FCSTD DOCUMENT  (FreeCAD 0.21R33668 +26 (Git))
Label: CaseV2_Assembly
License: All rights reserved
LicenseURL: https://en.wikipedia.org/wiki/All_rights_reserved
objects: App::Link×9, App::DocumentObjectGroup×3, PartDesign::CoordinateSystem×1, App::FeaturePython×1, App::Part×1
note: 1 computed .brp shape members not serialized (recipe doc carries the construction recipe); baked Part::Feature solids carry a one-line shape summary decoded from their .brp
EXTERNAL_REF file=Parts/Casing2.FCStd obj=LCS_Origin
EXTERNAL_REF file=Parts/Casing2.FCStd obj=Model
EXTERNAL_REF file=Parts/Casing2.FCStd obj=LCS_MLX
EXTERNAL_REF file=Parts/Support_MLX.FCStd obj=LCS_carrier
EXTERNAL_REF file=Parts/Support_MLX.FCStd obj=Model
EXTERNAL_REF file=Parts/MLX90640.FCStd obj=LCS_mlx
EXTERNAL_REF file=Parts/Support_MLX.FCStd obj=LCS_MLX
EXTERNAL_REF file=Parts/MLX90640.FCStd obj=Model
EXTERNAL_REF file=Parts/Casing2.FCStd obj=LCS_interface
EXTERNAL_REF file=Parts/Handgrip.FCStd obj=LCS_screw
EXTERNAL_REF file=Parts/Handgrip.FCStd obj=Model
EXTERNAL_REF file=Parts/Casing2.FCStd obj=LCS_beam
EXTERNAL_REF file=Parts/Casing_Lid_2.FCStd obj=LCS_screw
EXTERNAL_REF file=Parts/Casing_Lid_2.FCStd obj=Model
EXTERNAL_REF file=Parts/Casing2.FCStd obj=LCS_Display
EXTERNAL_REF file=Parts/Support_Display_new.FCStd obj=LCS_side
EXTERNAL_REF file=Parts/Support_Display_new.FCStd obj=Model
EXTERNAL_REF file=Parts/Display_Berrybase.FCStd obj=LCS_Connector
EXTERNAL_REF file=Parts/Support_Display_new.FCStd obj=LCS_display
EXTERNAL_REF file=Parts/Display_Berrybase.FCStd obj=Model
EXTERNAL_REF file=Parts/Casing2.FCStd obj=LCS_Raspi
EXTERNAL_REF file=Parts/Support_Raspi_new.FCStd obj=LCS_side
EXTERNAL_REF file=Parts/Support_Raspi_new.FCStd obj=Model
EXTERNAL_REF file=Parts/Raspberrypi4B.FCStd obj=LCS_Screw
EXTERNAL_REF file=Parts/Support_Raspi_new.FCStd obj=LCS_raspi
EXTERNAL_REF file=Parts/Raspberrypi4B.FCStd obj=Model

FEATURE [App::DocumentObjectGroup] Parts
FEATURE [PartDesign::CoordinateSystem] LCS_Origin
  AttacherType = Attacher::AttachEngine3D
  MapMode = 2
  Support = -> [X_Axis]
FEATURE [App::DocumentObjectGroup] Constraints
FEATURE [App::FeaturePython] Variables  # WARN: FeaturePython — macro-defined, semantics opaque (R4)
  Type = App::PropertyContainer
FEATURE [App::DocumentObjectGroup] Configurations
FEATURE [App::Link] Casing2
  AttachedBy = #LCS_Origin
  AttachedTo = Parent Assembly#LCS_Origin
  LinkedObject = -> <external Parts/Casing2.FCStd>#Model
  SolverId = Asm4EE
  expr: Placement = LCS_Origin.Placement * AttachmentOffset * Casing2#LCS_Origin.Placement ^ -1
FEATURE [App::Link] Support_MLX
  AttachedBy = #LCS_carrier
  AttachedTo = Casing2#LCS_MLX
  AttachmentOffset = pos=(0,0,0) rot=(0.707107,0.707107,0;3.14159rad)
  LinkPlacement = pos=(11.7198,36.5796,47.5) rot=(-0.519988,0.677661,-0.519988;4.33274rad)
  LinkedObject = -> <external Parts/Support_MLX.FCStd>#Model
  Placement = pos=(11.7198,36.5796,47.5) rot=(-0.519988,0.677661,-0.519988;4.33274rad)
  SolverId = Asm4EE
  expr: Placement = Casing2.Placement * Casing2#LCS_MLX.Placement * AttachmentOffset * Support_MLX#LCS_carrier.Placement ^ -1
FEATURE [App::Link] MLX90640
  AttachedBy = #LCS_mlx
  AttachedTo = Support_MLX#LCS_MLX
  AttachmentOffset = pos=(0,0,0) rot=(0,1,0;3.14159rad)
  LinkPlacement = pos=(13.0139,41.4093,47.5) rot=(0.621515,0.476905,0.621515;4.0316rad)
  LinkedObject = -> <external Parts/MLX90640.FCStd>#Model
  Placement = pos=(13.0139,41.4093,47.5) rot=(0.621515,0.476905,0.621515;4.0316rad)
  SolverId = Asm4EE
  expr: Placement = Support_MLX.Placement * Support_MLX#LCS_MLX.Placement * AttachmentOffset * MLX90640#LCS_mlx.Placement ^ -1
FEATURE [App::Link] Handgrip
  AttachedBy = #LCS_screw
  AttachedTo = Casing2#LCS_interface
  AttachmentOffset = pos=(0,0,0) rot=(1,0,0;3.14159rad)
  LinkPlacement = pos=(-46.3076,-21.9376,46.5) rot=(-0.704063,0.092692,0.704063;2.95674rad)
  LinkedObject = -> <external Parts/Handgrip.FCStd>#Model
  Placement = pos=(-46.3076,-21.9376,46.5) rot=(-0.704063,0.092692,0.704063;2.95674rad)
  SolverId = Asm4EE
  expr: Placement = Casing2.Placement * Casing2#LCS_interface.Placement * AttachmentOffset * Handgrip#LCS_screw.Placement ^ -1
FEATURE [App::Link] Casing_Lid_2
  AttachedBy = #LCS_screw
  AttachedTo = Casing2#LCS_beam
  AttachmentOffset = pos=(0,0,0) rot=(1,0,0;3.14159rad)
  LinkPlacement = pos=(-0.401924,-1.5,95) rot=(0,1,0;3.14159rad)
  LinkedObject = -> <external Parts/Casing_Lid_2.FCStd>#Model
  Placement = pos=(-0.401924,-1.5,95) rot=(0,1,0;3.14159rad)
  SolverId = Asm4EE
  expr: Placement = Casing2.Placement * Casing2#LCS_beam.Placement * AttachmentOffset * Casing_Lid_2#LCS_screw.Placement ^ -1
FEATURE [App::Link] Support_Display_new
  AttachedBy = #LCS_side
  AttachedTo = Casing2#LCS_Display
  AttachmentOffset = pos=(0,0,0) rot=(0.707107,-0.707107,0;3.14159rad)
  LinkPlacement = pos=(-12.8616,-41,47.5) rot=(0.57735,-0.57735,-0.57735;4.18879rad)
  LinkedObject = -> <external Parts/Support_Display_new.FCStd>#Model
  Placement = pos=(-12.8616,-41,47.5) rot=(0.57735,-0.57735,-0.57735;4.18879rad)
  SolverId = Asm4EE
  expr: Placement = Casing2.Placement * Casing2#LCS_Display.Placement * AttachmentOffset * Support_Display_new#LCS_side.Placement ^ -1
FEATURE [App::Link] Display_Berrybase
  AttachedBy = #LCS_Connector
  AttachedTo = Support_Display_new#LCS_display
  AttachmentOffset = pos=(0,0,0) rot=(0,0,1;3.14159rad)
  LinkPlacement = pos=(-11.8616,-41,48.5) rot=(-0.57735,-0.57735,-0.57735;2.0944rad)
  LinkedObject = -> <external Parts/Display_Berrybase.FCStd>#Model
  Placement = pos=(-11.8616,-41,48.5) rot=(-0.57735,-0.57735,-0.57735;2.0944rad)
  SolverId = Asm4EE
  expr: Placement = Support_Display_new.Placement * Support_Display_new#LCS_display.Placement * AttachmentOffset * Display_Berrybase#LCS_Connector.Placement ^ -1
FEATURE [App::Link] Support_Raspi_new
  AttachedBy = #LCS_side
  AttachedTo = Casing2#LCS_Raspi
  AttachmentOffset = pos=(0,0,0) rot=(0.707107,-0.707107,0;3.14159rad)
  LinkPlacement = pos=(-5.04252,6.75875,47.5) rot=(0.519988,-0.677661,-0.519988;4.33274rad)
  LinkedObject = -> <external Parts/Support_Raspi_new.FCStd>#Model
  Placement = pos=(-5.04252,6.75875,47.5) rot=(0.519988,-0.677661,-0.519988;4.33274rad)
  SolverId = Asm4EE
  expr: Placement = Casing2.Placement * Casing2#LCS_Raspi.Placement * AttachmentOffset * Support_Raspi_new#LCS_side.Placement ^ -1
FEATURE [App::Link] Raspberrypi4B
  AttachedBy = #LCS_Screw
  AttachedTo = Support_Raspi_new#LCS_raspi
  AttachmentOffset = pos=(0,0,0) rot=(0,0,1;3.14159rad)
  LinkPlacement = pos=(-6.0778,2.89505,45.5) rot=(-0.621515,-0.476905,0.621515;4.0316rad)
  LinkedObject = -> <external Parts/Raspberrypi4B.FCStd>#Model
  Placement = pos=(-6.0778,2.89505,45.5) rot=(-0.621515,-0.476905,0.621515;4.0316rad)
  SolverId = Asm4EE
  expr: Placement = Support_Raspi_new.Placement * Support_Raspi_new#LCS_raspi.Placement * AttachmentOffset * Raspberrypi4B#LCS_Screw.Placement ^ -1
FEATURE [App::Part] Model
  AssemblyType = Part::Link
  Group = -> [LCS_Origin,Constraints,Variables,Configurations,Casing2,Support_MLX,MLX90640,Handgrip,Casing_Lid_2,Support_Display_new,Display_Berrybase,Support_Raspi_new,Raspberrypi4B]
  Origin = -> Origin
  Type = Assembly

RESOLVED EXTERNAL PARTS (link-assembly join: the EXTERNAL_REF files above that resolve inside this repo's crawl, each included once):
---- part Parts/Casing2.FCStd = doc fcstd_00092494c22c ----
FCSTD DOCUMENT  (FreeCAD 0.21R33668 +26 (Git))
Label: Casing2
License: All rights reserved
LicenseURL: https://en.wikipedia.org/wiki/All_rights_reserved
objects: Sketcher::SketchObject×19, PartDesign::Pocket×14, PartDesign::CoordinateSystem×6, PartDesign::Hole×3, App::DocumentObjectGroup×3, PartDesign::Pad×2, Spreadsheet::Sheet×1, PartDesign::Fillet×1, App::FeaturePython×1, PartDesign::Body×1, App::Part×1, Mesh::Feature×1
note: 66 computed .brp shape members not serialized (recipe doc carries the construction recipe); baked Part::Feature solids carry a one-line shape summary decoded from their .brp
EXTERNAL_REF file=Display_Berrybase.FCStd obj=Spreadsheet
EXTERNAL_REF file=MLX90640.FCStd obj=Spreadsheet
EXTERNAL_REF file=Raspberrypi4B.FCStd obj=Spreadsheet
EXTERNAL_REF file=Support_Display_new.FCStd obj=Spreadsheet
EXTERNAL_REF file=Support_MLX.FCStd obj=Spreadsheet
EXTERNAL_REF file=Support_Raspi_new.FCStd obj=Spreadsheet

FEATURE [Spreadsheet::Sheet] Spreadsheet
  cells = B2='slant; C2(slant)==15 °; E2='main_case_width; F2(main_case_width)==95 mm; H2='display_width; I2(display_width)==<<Display_Berrybase>>#Spreadsheet.width; B3='walls_thickness; C3(walls_thickness)==2 mm; E3='main_case_height; F3(main_case_height)==85 mm; H3='display_height; I3(display_height)==<<Display_Berrybase>>#Spreadsheet.height; B4='screw_radius; C4(screw_radius)==1.5 mm; E4='main_case_length; F4(main_case_length)==100 mm; B5='front_thickness; C5(front_thickness)==5 mm; H5='mlx_cam_height; I5(mlx_cam_height)==<<MLX90640>>#Spreadsheet.cam_height; H6='mlx_extra_space; I6(mlx_extra_space)==2 mm; H7='mlx_radius; I7(mlx_radius)==<<MLX90640>>#Spreadsheet.cam_rad; B9='display_guard_depth; C9(display_guard_depth)==1 mm; E9='mlx_carrier_height; F9(mlx_carrier_height)==<<Support_MLX>>#Spreadsheet.carrier_height; H9='raspi_carrier_hole_dist; I9(raspi_carrier_hole_dist)==<<Support_Raspi_new>>#<<Spreadsheet>>.carrier_holes_space; B10='display_guard_size; C10(display_guard_size)==3 mm; E10='mlx_carrier_width; F10(mlx_carrier_width)==<<Support_MLX>>#Spreadsheet.carrier_width; H10='raspi_carrier_height; I10(raspi_carrier_height)==<<Support_Raspi_new>>#Spreadsheet.height; B11='display_clearance; C11(display_clearance)==1 mm; H11='raspi_carrier_depth; I11(raspi_carrier_depth)==<<Support_Raspi_new>>#Spreadsheet.depth; B12='display_hole_depth; C12(display_hole_depth)==display_width + display_clearance - display_guard_size - display_right_guard_extra; E12='beams_width; F12(beams_width)==10 mm; B13='display_right_guard_extra; C13(display_right_guard_extra)==5 mm; E13='beams_height; F13(beams_height)==10 mm; H13='raspi_height; I13(raspi_height)==<<Raspberrypi4B>>#Spreadsheet.height; H14='raspi_thickness; I14(raspi_thickness)==<<Raspberrypi4B>>#Spreadsheet.thickness; B15='display_thickness; C15(display_thickness)==<<Display_Berrybase>>#Spreadsheet.thickness; E15='beam_LB_offset; F15(beam_LB_offset)==80 mm; B16='display_carrier_height; C16(display_carrier_height)==<<Support_Display_new>>#Spreadsheet.height; E16='beam_LF_offset; F16(beam_LF_offset)==15 mm; H16='raspi_usb_width; I16(raspi_usb_width)==14 mm; E17='beam_UB_offset; F17(beam_UB_offset)==60 mm; H17='raspi_usb_height; I17(raspi_usb_height)==<<Raspberrypi4B>>#Spreadsheet.usb_height + 0 mm; B18='display_carrier_hole_dist; C18(display_carrier_hole_dist)==<<Support_Display_new>>#<<Spreadsheet>>.beams_seperation + <<Support_Display_new>>#<<Spreadsheet>>.beams_width; E18='beam_UF_offset; F18(beam_UF_offset)==15 mm; H18='raspi_eth_width; I18(raspi_eth_width)==<<Raspberrypi4B>>#Spreadsheet.ethernet_width; B19='display_carrier_offset; C19(display_carrier_offset)==display_thickness + display_carrier_height / 2 + 1 mm; H19='raspi_eth_height; I19(raspi_eth_height)==<<Raspberrypi4B>>#Spreadsheet.ethernet_height; E20='interface_width; F20(interface_width)==65 mm; H20='raspi_usb_lower_offset; I20(raspi_usb_lower_offset)==<<Raspberrypi4B>>#Spreadsheet.usb_lower_offset; B21='ports_clearance; C21(ports_clearance)==2 mm; E21='interface_height; F21(interface_height)==20 mm; H21='raspi_usb_middle_offset; I21(raspi_usb_middle_offset)==<<Raspberrypi4B>>#Spreadsheet.usb_middle_offset; E22='interface_screws_width; F22(interface_screws_width)==interface_width - beams_width; H22='raspi_eth_offset; I22(raspi_eth_offset)==<<Raspberrypi4B>>#Spreadsheet.ethernet_offset; B23='pen_radius; C23(pen_radius)==2.5 mm; E23='interface_screws_height; F23(interface_screws_height)==interface_height - beams_width; B24='pen_length; C24(pen_length)==90 mm; E24='interface_offset; F24(interface_offset)==2 mm; H24='sq_nut_width; I24(sq_nut_width)==5.8 mm; B25='pen_grip_width; C25(pen_grip_width)==7.5 mm; E25='interface_clearance; F25(interface_clearance)==0.5 mm; H25='sq_nut_height; I25(sq_nut_height)==2.1 mm; B26='pen_grip_height; C26(pen_grip_height)==11.5 mm; H26='sq_nut_hole_depth; I26(sq_nut_hole_depth)==(beams_height + sq_nut_width) / 2; B27='pen_radius_tolerance; C27(pen_radius_tolerance)==0.2 mm; H27='sq_nut_hole_offset; I27(sq_nut_hole_offset)==5 mm; B28='pen_hole_offset; C28(pen_hole_offset)==pen_grip_width - pen_radius - 1 mm
FEATURE [Sketcher::SketchObject] Sketch
  FullyConstrained = true
  MapMode = 5
  Support = -> [XY_Plane]
  expr: Constraints[7] = 90 ° + Spreadsheet.slant
  expr: Constraints[8] = Spreadsheet.main_case_height
  expr: Constraints[9] = Spreadsheet.main_case_length
  sketch-geometry (4):
    g0: LineSegment StartX=-29.1025 StartY=50 StartZ=0 EndX=55.8975 EndY=50 EndZ=0
    g1: LineSegment StartX=55.8975 StartY=50 StartZ=0 EndX=29.1025 EndY=-50 EndZ=0
    g2: LineSegment StartX=29.1025 StartY=-50 StartZ=0 EndX=-55.8975 EndY=-50 EndZ=0
    g3: LineSegment StartX=-55.8975 StartY=-50 StartZ=0 EndX=-29.1025 EndY=50 EndZ=0
  constraints (10):
    c: Coincident(g0,g1)
    c: Coincident(g1,g2)
    c: Coincident(g2,g3)
    c: Coincident(g3,g0)
    c: Horizontal(g0)
    c: Symmetric(g0,g2,g-1)
    c: Symmetric(g0,g1,g-1)
    c: Angle(g1,g2) = 1.8326
    c: DistanceX(g2,g2) = 85
    c: DistanceY(g1,g1) = 100
FEATURE [PartDesign::Pad] Pad
  Direction = (0,0,1)
  Length = 95
  Length2 = 10
  Profile = -> Sketch
  ReferenceAxis = -> Sketch [N_Axis]
  Type = 0
  expr: Length = Spreadsheet.main_case_width
FEATURE [Sketcher::SketchObject] Sketch001
  ExternalGeometry = -> [Pad]
  FullyConstrained = true
  MapMode = 5
  Placement = pos=(0,0,95) rot=(0,0,1;0rad)
  Support = -> [Pad]
  expr: Constraints[4] = Spreadsheet.walls_thickness
  expr: Constraints[5] = Spreadsheet.walls_thickness * (1 - tan(Spreadsheet.slant))
  expr: Constraints[7] = Spreadsheet.main_case_height - Spreadsheet.walls_thickness * 2
  expr: Constraints[8] = Spreadsheet.front_thickness
  sketch-geometry (4):
    g0: LineSegment StartX=-28.4423 StartY=45 StartZ=0 EndX=52.5577 EndY=45 EndZ=0
    g1: LineSegment StartX=52.5577 StartY=45 StartZ=0 EndX=27.6384 EndY=-48 EndZ=0
    g2: LineSegment StartX=27.6384 StartY=-48 StartZ=0 EndX=-53.3616 EndY=-48 EndZ=0
    g3: LineSegment StartX=-53.3616 StartY=-48 StartZ=0 EndX=-28.4423 EndY=45 EndZ=0
  constraints (12):
    c: Coincident(g0,g1)
    c: Coincident(g1,g2)
    c: Coincident(g2,g3)
    c: Coincident(g3,g0)
    c: DistanceY(g-5,g2) = 2
    c: DistanceX(g1,g-6) = 1.4641
    c: Horizontal(g2)
    c: DistanceX(g2,g2) = 81
    c: DistanceY(g0,g-4) = 5
    c: Horizontal(g0)
    c: Parallel(g3,g-4)
    c: Parallel(g1,g-6)
FEATURE [PartDesign::Pocket] Pocket
  BaseFeature = -> Pad
  Direction = (0,0,-1)
  Length = 93
  Length2 = 5
  Profile = -> Sketch001
  ReferenceAxis = -> Sketch001 [N_Axis]
  Type = 0
  expr: Length = Spreadsheet.main_case_width - Spreadsheet.walls_thickness
FEATURE [Sketcher::SketchObject] Sketch002
  ExternalGeometry = -> [Pocket]
  FullyConstrained = true
  MapMode = 5
  Placement = pos=(0,-48,0) rot=(0,0.707107,0.707107;3.14159rad)
  Support = -> [Pocket]
  expr: Constraints[11] = (Spreadsheet.main_case_width - Spreadsheet.walls_thickness * 2) / 2
  expr: Constraints[13] = Spreadsheet.display_width + Spreadsheet.display_clearance
  expr: Constraints[14] = Spreadsheet.display_height + Spreadsheet.display_clearance
  sketch-geometry (6):
    g0: LineSegment StartX=40.9916 StartY=4.74 StartZ=0 EndX=-15.2684 EndY=4.74 EndZ=0
    g1: LineSegment StartX=-15.2684 StartY=4.74 StartZ=0 EndX=-15.2684 EndY=90.26 EndZ=0
    g2: LineSegment StartX=-15.2684 StartY=90.26 StartZ=0 EndX=40.9916 EndY=90.26 EndZ=0
    g3: LineSegment StartX=40.9916 StartY=90.26 StartZ=0 EndX=40.9916 EndY=4.74 EndZ=0
    g4: LineSegment StartX=12.8616 StartY=95 StartZ=0 EndX=12.8616 EndY=2 EndZ=0
    g5: GeomPoint X=12.8616 Y=47.5 Z=0
  constraints (15):
    c: Coincident(g0,g1)
    c: Coincident(g1,g2)
    c: Coincident(g2,g3)
    c: Coincident(g3,g0)
    c: Horizontal(g0)
    c: Horizontal(g2)
    c: Vertical(g1)
    c: Vertical(g3)
    c: Symmetric(g-6,g-6,g4)
    c: Symmetric(g-5,g-4,g4)
    c: PointOnObject(g5,g4)
    c: DistanceY(g4,g5) = 45.5
    c: Symmetric(g1,g0,g5)
    c: DistanceY(g1,g1) = 85.52
    c: DistanceX(g2,g2) = 56.26
FEATURE [PartDesign::Pocket] Pocket001
  BaseFeature = -> Pocket
  Direction = (0,-1,2e-16)
  Length = 1
  Length2 = 5
  Profile = -> Sketch002
  ReferenceAxis = -> Sketch002 [N_Axis]
  Type = 0
  expr: Length = Spreadsheet.walls_thickness - Spreadsheet.display_guard_depth
FEATURE [Sketcher::SketchObject] Sketch003
  ExternalGeometry = -> [Pocket001]
  FullyConstrained = true
  MapMode = 5
  Placement = pos=(0,-49,1.23e-14) rot=(0,0.707107,0.707107;3.14159rad)
  Support = -> [Pocket001]
  expr: Constraints[10] = Spreadsheet.display_guard_size
  expr: Constraints[11] = Spreadsheet.display_guard_size
  expr: Constraints[8] = Spreadsheet.display_right_guard_extra
  expr: Constraints[9] = Spreadsheet.display_guard_size
  sketch-geometry (4):
    g0: LineSegment StartX=-12.2684 StartY=87.26 StartZ=0 EndX=37.9916 EndY=87.26 EndZ=0
    g1: LineSegment StartX=37.9916 StartY=87.26 StartZ=0 EndX=37.9916 EndY=9.74 EndZ=0
    g2: LineSegment StartX=37.9916 StartY=9.74 StartZ=0 EndX=-12.2684 EndY=9.74 EndZ=0
    g3: LineSegment StartX=-12.2684 StartY=9.74 StartZ=0 EndX=-12.2684 EndY=87.26 EndZ=0
  constraints (12):
    c: Coincident(g0,g1)
    c: Coincident(g1,g2)
    c: Coincident(g2,g3)
    c: Coincident(g3,g0)
    c: Horizontal(g0)
    c: Horizontal(g2)
    c: Vertical(g1)
    c: Vertical(g3)
    c: DistanceY(g-5,g2) = 5
    c: DistanceY(g0,g-5) = 3
    c: DistanceX(g-5,g0) = 3
    c: DistanceX(g0,g-4) = 3
FEATURE [PartDesign::Pocket] Pocket002
  BaseFeature = -> Pocket001
  Direction = (0,-1,2e-16)
  Length = 1
  Length2 = 5
  Profile = -> Sketch003
  ReferenceAxis = -> Sketch003 [N_Axis]
  Type = 0
  expr: Length = Spreadsheet.display_guard_depth
FEATURE [PartDesign::Fillet] Fillet
  Base = -> Pocket002 [Edge1]
  BaseFeature = -> Pocket002
  Radius = 5
  SupportTransform = false
  UseAllEdges = false
FEATURE [Sketcher::SketchObject] Sketch004
  ExternalGeometry = -> [Fillet]
  FullyConstrained = true
  MapMode = 5
  Placement = pos=(0,0,2) rot=(0,0,1;0rad)
  Support = -> [Fillet]
  expr: Constraints[10] = Spreadsheet.display_carrier_offset
  expr: Constraints[11] = Spreadsheet.display_carrier_hole_dist
  expr: Constraints[12] = Spreadsheet.screw_radius
  expr: Constraints[13] = Spreadsheet.screw_radius
  expr: Constraints[14] = Spreadsheet.screw_radius
  expr: Constraints[15] = Spreadsheet.screw_radius
  expr: Constraints[21] = Spreadsheet.raspi_carrier_height
  expr: Constraints[22] = Spreadsheet.walls_thickness
  expr: Constraints[25] = Spreadsheet.raspi_carrier_hole_dist
  expr: Constraints[26] = Spreadsheet.screw_radius
  expr: Constraints[27] = Spreadsheet.screw_radius
  expr: Constraints[30] = Spreadsheet.mlx_carrier_height - Spreadsheet.mlx_carrier_width
  expr: Constraints[33] = 90 ° + Spreadsheet.slant
  expr: Constraints[9] = Spreadsheet.mlx_cam_height + Spreadsheet.mlx_extra_space + Spreadsheet.front_thickness
  sketch-geometry (14):
    g0: Circle CenterX=3.02671 CenterY=33.7326 CenterZ=0 NormalX=0 NormalY=0 NormalZ=1 AngleXU=0 Radius=1.5
    g1: Circle CenterX=17.8247 CenterY=29.7674 CenterZ=0 NormalX=0 NormalY=0 NormalZ=1 AngleXU=0 Radius=1.5
    g2: Circle CenterX=-15.8225 CenterY=14.8236 CenterZ=0 NormalX=0 NormalY=0 NormalZ=1 AngleXU=0 Radius=1.5
    g3: Circle CenterX=8.32565 CenterY=8.35314 CenterZ=0 NormalX=0 NormalY=0 NormalZ=1 AngleXU=0 Radius=1.5
    g4: Circle CenterX=-25.3616 CenterY=-36 CenterZ=0 NormalX=0 NormalY=0 NormalZ=1 AngleXU=0 Radius=1.5
    g5: Circle CenterX=-0.361561 CenterY=-36 CenterZ=0 NormalX=0 NormalY=0 NormalZ=1 AngleXU=0 Radius=1.5
    g6: LineSegment StartX=15.3158 StartY=50 StartZ=0 EndX=10.4257 EndY=31.75 EndZ=0
    g7: LineSegment StartX=3.02671 StartY=33.7326 StartZ=0 EndX=17.8247 EndY=29.7674 EndZ=0
    g8: LineSegment StartX=-12.8616 StartY=-48 StartZ=0 EndX=-12.8616 EndY=-36 EndZ=0
    g9: LineSegment StartX=-25.3616 StartY=-36 StartZ=0 EndX=-0.361561 EndY=-36 EndZ=0
    g10: LineSegment StartX=-35.141 StartY=20 StartZ=0 EndX=25.7123 EndY=3.6944 EndZ=0
    g11: GeomPoint X=-33.2092 Y=19.4824 Z=0
    g12: GeomPoint X=-3.74843 Y=11.5884 Z=0
    g13: LineSegment StartX=-25.2659 StartY=50 StartZ=0 EndX=55.8975 EndY=50 EndZ=0
  constraints (34):
    c: Symmetric(g7,g7,g6)
    c: Coincident(g0,g7)
    c: Coincident(g1,g7)
    c: Symmetric(g-5,g-6,g8)
    c: Symmetric(g9,g9,g8)
    c: Coincident(g4,g9)
    c: Coincident(g5,g9)
    c: Vertical(g8)
    c: Horizontal(g9)
    c: DistanceY(g6,g6) = 18.25
    c: DistanceY(g8,g8) = 12
    c: DistanceX(g9,g9) = 25
    c: Radius(g0) = 1.5
    c: Radius(g1) = 1.5
    c: Radius(g4) = 1.5
    c: Radius(g5) = 1.5
    c: PointOnObject(g10,g-4)
    c: PointOnObject(g11,g10)
    c: Symmetric(g11,g10,g12)
    c: Perpendicular(g10,g-4)
    c: DistanceY(g10,g-4) = 25
    c: Distance(g11,g10) = 61
    c: Distance(g11,g10) = 2
    c: Symmetric(g2,g3,g12)
    c: PointOnObject(g2,g10)
    c: Distance(g3,g2) = 25
    c: Radius(g2) = 1.5
    c: Radius(g3) = 1.5
    c: Symmetric(g-7,g-8,g6)
    c: Perpendicular(g7,g6)
    c: Distance(g7) = 15.32
    c: Coincident(g13,g-7)
    c: Coincident(g13,g-8)
    c: Angle(g6,g13) = 1.8326
FEATURE [PartDesign::Hole] Hole
  BaseFeature = -> Fillet
  CustomThreadClearance = 0
  Depth = 358.646
  DepthType = 1
  Diameter = 3.4
  DrillForDepth = false
  DrillPoint = 1
  DrillPointAngle = 118
  HoleCutCountersinkAngle = 90
  HoleCutCustomValues = false
  HoleCutDepth = 0
  HoleCutDiameter = 6.1
  HoleCutType = 0
  ModelThread = false
  Profile = -> Sketch004
  Tapered = false
  TaperedAngle = 90
  ThreadClass = 0
  ThreadDepth = 358.646
  ThreadDepthType = 0
  ThreadDirection = 0
  ThreadFit = 0
  ThreadSize = 9
  ThreadType = 1
  Threaded = false
  UseCustomThreadClearance = false
FEATURE [Sketcher::SketchObject] Sketch005
  ExternalGeometry = -> [Hole]
  FullyConstrained = true
  MapMode = 5
  Placement = pos=(0,50,0) rot=(0,0.707107,0.707107;3.14159rad)
  Support = -> [Hole]
  expr: Constraints[2] = (Spreadsheet.mlx_radius + 0.15 mm) / cos(Spreadsheet.slant)
  sketch-geometry (3):
    g0: LineSegment StartX=-55.8975 StartY=95 StartZ=0 EndX=25.2659 EndY=0 EndZ=0
    g1: LineSegment StartX=-55.8975 StartY=0 StartZ=0 EndX=25.2659 EndY=95 EndZ=0
    g2: Circle CenterX=-15.3158 CenterY=47.5 CenterZ=0 NormalX=0 NormalY=0 NormalZ=1 AngleXU=0 Radius=4.96933
  constraints (7):
    c: PointOnObject(g2,g0)
    c: PointOnObject(g2,g1)
    c: Radius(g2) = 4.96933
    c: Coincident(g0,g-3)
    c: Coincident(g1,g-4)
    c: Coincident(g0,g-4)
    c: Coincident(g1,g-3)
FEATURE [PartDesign::Pocket] Pocket003
  BaseFeature = -> Hole
  Direction = (-0.267949,-1,0)
  Length = 5
  Length2 = 5
  Profile = -> Sketch005
  ReferenceAxis = -> Sketch005 [N_Axis]
  Type = 0
  UseCustomVector = true
  expr: .Direction.x = tan(Spreadsheet.slant) * -1
  expr: Length = Spreadsheet.front_thickness
FEATURE [Sketcher::SketchObject] Sketch006
  ExternalGeometry = -> [Pocket003]
  FullyConstrained = true
  MapMode = 5
  Placement = pos=(0,0,2) rot=(0,0,1;0rad)
  Support = -> [Pocket003]
  expr: Constraints[14] = Spreadsheet.raspi_height
  expr: Constraints[15] = Spreadsheet.raspi_thickness
  expr: Constraints[19] = Spreadsheet.raspi_eth_offset
  expr: Constraints[20] = Spreadsheet.raspi_usb_middle_offset
  expr: Constraints[21] = Spreadsheet.raspi_usb_lower_offset
  expr: Constraints[49] = Spreadsheet.raspi_eth_width + Spreadsheet.ports_clearance
  expr: Constraints[4] = (Spreadsheet.raspi_carrier_depth - Spreadsheet.ports_clearance) / 2
  expr: Constraints[50] = Spreadsheet.raspi_usb_width + Spreadsheet.ports_clearance
  expr: Constraints[51] = Spreadsheet.raspi_usb_width + Spreadsheet.ports_clearance
  expr: Constraints[52] = Spreadsheet.raspi_eth_height + Spreadsheet.ports_clearance
  expr: Constraints[53] = Spreadsheet.raspi_usb_height + Spreadsheet.ports_clearance
  expr: Constraints[54] = Spreadsheet.raspi_usb_height + Spreadsheet.ports_clearance
  sketch-geometry (21):
    g0: LineSegment StartX=-15.8225 StartY=14.8236 StartZ=0 EndX=8.32565 EndY=8.35314 EndZ=0
    g1: LineSegment StartX=-3.74843 StartY=11.5884 StartZ=0 EndX=-4.7837 EndY=7.72468 EndZ=0
    g2: LineSegment StartX=22.2622 StartY=0.477744 StartZ=0 EndX=-31.8296 EndY=14.9716 EndZ=0
    g3: LineSegment StartX=-31.8296 StartY=14.9716 StartZ=0 EndX=-32.8649 EndY=11.1079 EndZ=0
    g4: LineSegment StartX=-32.8649 StartY=11.1079 StartZ=0 EndX=21.2269 EndY=-3.38596 EndZ=0
    g5: LineSegment StartX=21.2269 StartY=-3.38596 StartZ=0 EndX=22.2622 EndY=0.477744 EndZ=0
    g6: GeomPoint X=-22.9642 Y=8.45501 Z=0
    g7: GeomPoint X=-4.85305 Y=3.60216 Z=0
    g8: GeomPoint X=12.5336 Y=-1.05659 Z=0
    g9: LineSegment StartX=-31.6575 StartY=10.7844 StartZ=0 EndX=-14.2708 EndY=6.12564 EndZ=0
    g10: LineSegment StartX=-14.2708 StartY=6.12564 StartZ=0 EndX=-18.2825 EndY=-8.84621 EndZ=0
    g11: LineSegment StartX=-18.2825 StartY=-8.84621 StartZ=0 EndX=-35.6692 EndY=-4.18747 EndZ=0
    g12: LineSegment StartX=-35.6692 StartY=-4.18747 StartZ=0 EndX=-31.6575 EndY=10.7844 EndZ=0
    g13: LineSegment StartX=-12.5805 StartY=5.67271 StartZ=0 EndX=2.87435 EndY=1.5316 EndZ=0
    g14: LineSegment StartX=2.87435 StartY=1.5316 StartZ=0 EndX=-1.78439 EndY=-15.8551 EndZ=0
    g15: LineSegment StartX=-1.78439 StartY=-15.8551 StartZ=0 EndX=-17.2392 EndY=-11.714 EndZ=0
    g16: LineSegment StartX=-17.2392 StartY=-11.714 StartZ=0 EndX=-12.5805 EndY=5.67271 EndZ=0
    g17: LineSegment StartX=4.8062 StartY=1.01396 StartZ=0 EndX=20.261 EndY=-3.12714 EndZ=0
    g18: LineSegment StartX=20.261 StartY=-3.12714 StartZ=0 EndX=15.6023 EndY=-20.5138 EndZ=0
    g19: LineSegment StartX=15.6023 StartY=-20.5138 StartZ=0 EndX=0.147462 EndY=-16.3727 EndZ=0
    g20: LineSegment StartX=0.147462 StartY=-16.3727 StartZ=0 EndX=4.8062 EndY=1.01396 EndZ=0
  constraints (55):
    c: Coincident(g0,g-3)
    c: Coincident(g0,g-4)
    c: Symmetric(g0,g0,g1)
    c: Perpendicular(g1,g0)
    c: Distance(g1) = 4
    c: Coincident(g2,g3)
    c: Coincident(g3,g4)
    c: Coincident(g4,g5)
    c: Coincident(g5,g2)
    c: Symmetric(g2,g2,g1)
    c: Parallel(g0,g2)
    c: Parallel(g2,g4)
    c: Parallel(g1,g5)
    c: Parallel(g1,g3)
    c: Distance(g2) = 56
    c: Distance(g5) = 4
    c: PointOnObject(g6,g4)
    c: PointOnObject(g7,g4)
    c: PointOnObject(g8,g4)
    c: Distance(g6,g3) = 10.25
    c: Distance(g7,g3) = 29
    c: Distance(g8,g3) = 47
    c: Coincident(g9,g10)
    c: Coincident(g10,g11)
    c: Coincident(g11,g12)
    c: Coincident(g12,g9)
    c: Coincident(g13,g14)
    c: Coincident(g14,g15)
    c: Coincident(g15,g16)
    c: Coincident(g16,g13)
    c: Coincident(g17,g18)
    c: Coincident(g18,g19)
    c: Coincident(g19,g20)
    c: Coincident(g20,g17)
    c: PointOnObject(g9,g4)
    c: PointOnObject(g13,g4)
    c: PointOnObject(g17,g4)
    c: Symmetric(g9,g9,g6)
    c: Symmetric(g13,g13,g7)
    c: Symmetric(g17,g17,g8)
    c: Equal(g9,g11)
    c: Equal(g13,g15)
    c: Equal(g17,g19)
    c: Perpendicular(g12,g9)
    c: Perpendicular(g16,g13)
    c: Perpendicular(g20,g17)
    c: Parallel(g9,g11)
    c: Parallel(g13,g15)
    c: Parallel(g17,g19)
    c: Distance(g11) = 18
    c: Distance(g15) = 16
    c: Distance(g19) = 16
    c: Distance(g12) = 15.5
    c: Distance(g16) = 18
    c: Distance(g20) = 18
FEATURE [PartDesign::Pocket] Pocket004
  BaseFeature = -> Pocket003
  Direction = (0,0,-1)
  Length = 5
  Length2 = 5
  Profile = -> Sketch006
  ReferenceAxis = -> Sketch006 [N_Axis]
  Type = 1
FEATURE [Sketcher::SketchObject] Sketch007
  ExternalGeometry = -> [Pocket004]
  FullyConstrained = true
  MapMode = 5
  Placement = pos=(0,0,2) rot=(0,0,1;0rad)
  Support = -> [Pocket004]
  expr: Constraints[36] = Spreadsheet.beams_height
  expr: Constraints[37] = Spreadsheet.beams_height
  expr: Constraints[38] = Spreadsheet.beams_height
  expr: Constraints[39] = Spreadsheet.beams_height
  expr: Constraints[40] = Spreadsheet.beams_width
  expr: Constraints[41] = Spreadsheet.beams_width * 3
  expr: Constraints[42] = Spreadsheet.beams_width
  expr: Constraints[43] = Spreadsheet.beams_width
  expr: Constraints[44] = Spreadsheet.beam_LF_offset
  expr: Constraints[45] = Spreadsheet.beam_LB_offset
  expr: Constraints[46] = Spreadsheet.beam_UF_offset
  expr: Constraints[47] = Spreadsheet.beam_UB_offset
  sketch-geometry (16):
    g0: LineSegment StartX=-30.0678 StartY=38.9333 StartZ=0 EndX=-20.4086 EndY=36.3451 EndZ=0
    g1: LineSegment StartX=-20.4086 StartY=36.3451 StartZ=0 EndX=-22.9968 EndY=26.6859 EndZ=0
    g2: LineSegment StartX=-22.9968 StartY=26.6859 StartZ=0 EndX=-32.656 EndY=29.2741 EndZ=0
    g3: LineSegment StartX=-32.656 StartY=29.2741 StartZ=0 EndX=-30.0678 EndY=38.9333 EndZ=0
    g4: LineSegment StartX=-41.7147 StartY=-4.53334 StartZ=0 EndX=-32.0554 EndY=-7.12153 EndZ=0
    g5: LineSegment StartX=-32.0554 StartY=-7.12153 StartZ=0 EndX=-39.82 EndY=-36.0993 EndZ=0
    g6: LineSegment StartX=-39.82 StartY=-36.0993 StartZ=0 EndX=-49.4793 EndY=-33.5111 EndZ=0
    g7: LineSegment StartX=-49.4793 StartY=-33.5111 StartZ=0 EndX=-41.7147 EndY=-4.53334 EndZ=0
    g8: LineSegment StartX=24.4497 StartY=-21.2637 StartZ=0 EndX=34.1089 EndY=-23.8519 EndZ=0
    g9: LineSegment StartX=34.1089 StartY=-23.8519 StartZ=0 EndX=31.5207 EndY=-33.5111 EndZ=0
    g10: LineSegment StartX=31.5207 StartY=-33.5111 StartZ=0 EndX=21.8615 EndY=-30.9229 EndZ=0
    g11: LineSegment StartX=21.8615 StartY=-30.9229 StartZ=0 EndX=24.4497 EndY=-21.2637 EndZ=0
    g12: LineSegment StartX=36.0965 StartY=22.203 StartZ=0 EndX=45.7558 EndY=19.6148 EndZ=0
    g13: LineSegment StartX=45.7558 StartY=19.6148 StartZ=0 EndX=43.1676 EndY=9.95555 EndZ=0
    g14: LineSegment StartX=43.1676 StartY=9.95555 StartZ=0 EndX=33.5083 EndY=12.5437 EndZ=0
    g15: LineSegment StartX=33.5083 StartY=12.5437 StartZ=0 EndX=36.0965 EndY=22.203 EndZ=0
  constraints (48):
    c: Coincident(g0,g1)
    c: Coincident(g1,g2)
    c: Coincident(g2,g3)
    c: Coincident(g3,g0)
    c: Coincident(g4,g5)
    c: Coincident(g5,g6)
    c: Coincident(g6,g7)
    c: Coincident(g7,g4)
    c: Coincident(g8,g9)
    c: Coincident(g9,g10)
    c: Coincident(g10,g11)
    c: Coincident(g11,g8)
    c: Coincident(g12,g13)
    c: Coincident(g13,g14)
    c: Coincident(g14,g15)
    c: Coincident(g15,g12)
    c: PointOnObject(g0,g-3)
    c: PointOnObject(g2,g-3)
    c: PointOnObject(g4,g-3)
    c: PointOnObject(g6,g-3)
    c: PointOnObject(g12,g-4)
    c: PointOnObject(g13,g-4)
    c: PointOnObject(g8,g-4)
    c: PointOnObject(g9,g-4)
    c: Equal(g3,g1)
    c: Equal(g7,g5)
    c: Equal(g13,g15)
    c: Equal(g9,g11)
    c: Parallel(g3,g1)
    c: Parallel(g7,g5)
    c: Parallel(g9,g11)
    c: Parallel(g13,g15)
    c: Perpendicular(g0,g3)
    c: Perpendicular(g4,g7)
    c: Perpendicular(g12,g13)
    c: Perpendicular(g8,g9)
    c: Distance(g0) = 10
    c: Distance(g4) = 10
    c: Distance(g12) = 10
    c: Distance(g8) = 10
    c: Distance(g1) = 10
    c: Distance(g5) = 30
    c: Distance(g15) = 10
    c: Distance(g11) = 10
    c: Distance(g6,g-6) = 15
    c: Distance(g2,g-6) = 80
    c: Distance(g9,g-6) = 15
    c: Distance(g13,g-6) = 60
FEATURE [PartDesign::Pad] Pad001
  BaseFeature = -> Pocket004
  Direction = (0,0,1)
  Length = 91
  Length2 = 10
  Profile = -> Sketch007
  ReferenceAxis = -> Sketch007 [N_Axis]
  Type = 0
  expr: Length = Spreadsheet.main_case_width - Spreadsheet.walls_thickness * 2
FEATURE [Sketcher::SketchObject] Sketch008
  ExternalGeometry = -> [Pad001]
  FullyConstrained = true
  MapMode = 5
  Placement = pos=(0,0,93) rot=(0,0,1;0rad)
  Support = -> [Pad001]
  expr: Constraints[10] = Spreadsheet.beams_width
  expr: Constraints[3] = Spreadsheet.screw_radius
  expr: Constraints[4] = Spreadsheet.screw_radius
  expr: Constraints[5] = Spreadsheet.screw_radius
  expr: Constraints[6] = Spreadsheet.screw_radius
  sketch-geometry (5):
    g0: Circle CenterX=-26.5323 CenterY=32.8096 CenterZ=0 NormalX=0 NormalY=0 NormalZ=1 AngleXU=0 Radius=1.5
    g1: Circle CenterX=39.632 CenterY=16.0793 CenterZ=0 NormalX=0 NormalY=0 NormalZ=1 AngleXU=0 Radius=1.5
    g2: Circle CenterX=27.9852 CenterY=-27.3874 CenterZ=0 NormalX=0 NormalY=0 NormalZ=1 AngleXU=0 Radius=1.5
    g3: Circle CenterX=-43.3556 CenterY=-29.9756 CenterZ=0 NormalX=0 NormalY=0 NormalZ=1 AngleXU=0 Radius=1.5
    g4: LineSegment StartX=-37.2318 StartY=-26.44 StartZ=0 EndX=-46.8911 EndY=-23.8519 EndZ=0
  constraints (12):
    c: Symmetric(g-3,g-5,g0)
    c: Symmetric(g-7,g-8,g1)
    c: Symmetric(g-10,g-11,g2)
    c: Radius(g0) = 1.5
    c: Radius(g3) = 1.5
    c: Radius(g1) = 1.5
    c: Radius(g2) = 1.5
    c: PointOnObject(g4,g-13)
    c: PointOnObject(g4,g-15)
    c: Parallel(g4,g-14)
    c: Distance(g4,g-14) = 10
    c: Symmetric(g4,g-14,g3)
FEATURE [PartDesign::Hole] Hole001
  BaseFeature = -> Pad001
  CustomThreadClearance = 0
  Depth = 50
  DepthType = 0
  Diameter = 3.4
  DrillForDepth = false
  DrillPoint = 1
  DrillPointAngle = 118
  HoleCutCountersinkAngle = 90
  HoleCutCustomValues = false
  HoleCutDepth = 0
  HoleCutDiameter = 6.1
  HoleCutType = 0
  ModelThread = false
  Profile = -> Sketch008
  Tapered = false
  TaperedAngle = 90
  ThreadClass = 0
  ThreadDepth = 50
  ThreadDepthType = 0
  ThreadDirection = 0
  ThreadFit = 0
  ThreadSize = 9
  ThreadType = 1
  Threaded = false
  UseCustomThreadClearance = false
  expr: Depth = 50
FEATURE [Sketcher::SketchObject] Sketch009
  ExternalGeometry = -> [Hole001]
  FullyConstrained = true
  MapMode = 5
  Placement = pos=(28.1278,-7.53681,0) rot=(-0.476905,0.621515,0.621515;4.0316rad)
  Support = -> [Hole001]
  expr: Constraints[19] = Spreadsheet.sq_nut_hole_offset
  expr: Constraints[20] = Spreadsheet.sq_nut_height
  expr: Constraints[21] = Spreadsheet.sq_nut_width
  expr: Constraints[25] = Spreadsheet.sq_nut_hole_offset
  expr: Constraints[26] = Spreadsheet.sq_nut_height
  expr: Constraints[27] = Spreadsheet.sq_nut_width
  sketch-geometry (10):
    g0: LineSegment StartX=-28.6889 StartY=88 StartZ=0 EndX=-22.8889 EndY=88 EndZ=0
    g1: LineSegment StartX=-22.8889 StartY=88 StartZ=0 EndX=-22.8889 EndY=85.9 EndZ=0
    g2: LineSegment StartX=-22.8889 StartY=85.9 StartZ=0 EndX=-28.6889 EndY=85.9 EndZ=0
    g3: LineSegment StartX=-28.6889 StartY=85.9 StartZ=0 EndX=-28.6889 EndY=88 EndZ=0
    g4: LineSegment StartX=16.3111 StartY=88 StartZ=0 EndX=22.1111 EndY=88 EndZ=0
    g5: LineSegment StartX=22.1111 StartY=88 StartZ=0 EndX=22.1111 EndY=85.9 EndZ=0
    g6: LineSegment StartX=22.1111 StartY=85.9 StartZ=0 EndX=16.3111 EndY=85.9 EndZ=0
    g7: LineSegment StartX=16.3111 StartY=85.9 StartZ=0 EndX=16.3111 EndY=88 EndZ=0
    g8: LineSegment StartX=-25.7889 StartY=93 StartZ=0 EndX=-25.7889 EndY=88 EndZ=0
    g9: LineSegment StartX=19.2111 StartY=93 StartZ=0 EndX=19.2111 EndY=88 EndZ=0
  constraints (28):
    c: Coincident(g0,g1)
    c: Coincident(g1,g2)
    c: Coincident(g2,g3)
    c: Coincident(g3,g0)
    c: Horizontal(g0)
    c: Horizontal(g2)
    c: Vertical(g1)
    c: Vertical(g3)
    c: Coincident(g4,g5)
    c: Coincident(g5,g6)
    c: Coincident(g6,g7)
    c: Coincident(g7,g4)
    c: Horizontal(g4)
    c: Horizontal(g6)
    c: Vertical(g5)
    c: Vertical(g7)
    c: Vertical(g8)
    c: Symmetric(g-4,g-5,g8)
    c: Symmetric(g0,g0,g8)
    c: DistanceY(g8,g8) = 5
    c: DistanceY(g3,g3) = 2.1
    c: DistanceX(g2,g2) = 5.8
    c: Vertical(g9)
    c: Symmetric(g-7,g-8,g9)
    c: Symmetric(g4,g4,g9)
    c: DistanceY(g9,g9) = 5
    c: DistanceY(g7,g7) = 2.1
    c: DistanceX(g6,g6) = 5.8
FEATURE [PartDesign::Pocket] Pocket005
  BaseFeature = -> Hole001
  Direction = (0.965926,-0.258819,-2e-16)
  Length = 7.9
  Length2 = 5
  Profile = -> Sketch009
  ReferenceAxis = -> Sketch009 [N_Axis]
  Type = 0
  expr: Length = Spreadsheet.sq_nut_hole_depth
FEATURE [Sketcher::SketchObject] Sketch010
  ExternalGeometry = -> [Pocket005]
  FullyConstrained = true
  MapMode = 5
  Placement = pos=(-28.1278,7.53681,0) rot=(0.677661,0.519988,0.519988;1.95044rad)
  Support = -> [Pocket005]
  expr: Constraints[19] = Spreadsheet.sq_nut_hole_offset
  expr: Constraints[20] = Spreadsheet.sq_nut_height
  expr: Constraints[21] = Spreadsheet.sq_nut_width
  expr: Constraints[24] = Spreadsheet.sq_nut_hole_offset
  expr: Constraints[25] = Spreadsheet.sq_nut_height
  expr: Constraints[26] = Spreadsheet.sq_nut_width
  expr: Constraints[29] = Spreadsheet.beams_width
  sketch-geometry (11):
    g0: LineSegment StartX=-43.0754 StartY=88 StartZ=0 EndX=-37.2754 EndY=88 EndZ=0
    g1: LineSegment StartX=-37.2754 StartY=88 StartZ=0 EndX=-37.2754 EndY=85.9 EndZ=0
    g2: LineSegment StartX=-37.2754 StartY=85.9 StartZ=0 EndX=-43.0754 EndY=85.9 EndZ=0
    g3: LineSegment StartX=-43.0754 StartY=85.9 StartZ=0 EndX=-43.0754 EndY=88 EndZ=0
    g4: LineSegment StartX=21.9246 StartY=88 StartZ=0 EndX=27.7246 EndY=88 EndZ=0
    g5: LineSegment StartX=27.7246 StartY=88 StartZ=0 EndX=27.7246 EndY=85.9 EndZ=0
    g6: LineSegment StartX=27.7246 StartY=85.9 StartZ=0 EndX=21.9246 EndY=85.9 EndZ=0
    g7: LineSegment StartX=21.9246 StartY=85.9 StartZ=0 EndX=21.9246 EndY=88 EndZ=0
    g8: LineSegment StartX=-40.1754 StartY=93 StartZ=0 EndX=-40.1754 EndY=88 EndZ=0
    g9: LineSegment StartX=24.8246 StartY=93 StartZ=0 EndX=24.8246 EndY=88 EndZ=0
    g10: GeomPoint X=-35.1754 Y=93 Z=0
  constraints (30):
    c: Coincident(g0,g1)
    c: Coincident(g1,g2)
    c: Coincident(g2,g3)
    c: Coincident(g3,g0)
    c: Horizontal(g0)
    c: Horizontal(g2)
    c: Vertical(g1)
    c: Vertical(g3)
    c: Coincident(g4,g5)
    c: Coincident(g5,g6)
    c: Coincident(g6,g7)
    c: Coincident(g7,g4)
    c: Horizontal(g4)
    c: Horizontal(g6)
    c: Vertical(g5)
    c: Vertical(g7)
    c: Vertical(g9)
    c: Symmetric(g0,g0,g8)
    c: Vertical(g8)
    c: DistanceY(g8,g8) = 5
    c: DistanceY(g3,g3) = 2.1
    c: DistanceX(g2,g2) = 5.8
    c: Symmetric(g-7,g-8,g9)
    c: Symmetric(g4,g4,g9)
    c: DistanceY(g9,g9) = 5
    c: DistanceY(g7,g7) = 2.1
    c: DistanceX(g6,g6) = 5.8
    c: PointOnObject(g10,g-4)
    c: Symmetric(g-4,g10,g8)
    c: DistanceX(g-4,g10) = 10
FEATURE [PartDesign::Pocket] Pocket006
  BaseFeature = -> Pocket005
  Direction = (-0.965926,0.258819,1e-16)
  Length = 7.9
  Length2 = 5
  Profile = -> Sketch010
  ReferenceAxis = -> Sketch010 [N_Axis]
  Type = 0
  expr: Length = Spreadsheet.sq_nut_hole_depth
FEATURE [Sketcher::SketchObject] Sketch011
  ExternalGeometry = -> [Pocket006]
  FullyConstrained = true
  MapMode = 5
  Placement = pos=(-37.787,10.125,0) rot=(0.677661,0.519988,0.519988;1.95044rad)
  Support = -> [Pocket006]
  sketch-geometry (10):
    g0: LineSegment StartX=-4.17543 StartY=88 StartZ=0 EndX=5.82457 EndY=88 EndZ=0
    g1: LineSegment StartX=5.82457 StartY=88 StartZ=0 EndX=5.82457 EndY=68 EndZ=0
    g2: LineSegment StartX=5.82457 StartY=68 StartZ=0 EndX=-4.17543 EndY=68 EndZ=0
    g3: LineSegment StartX=-4.17543 StartY=68 StartZ=0 EndX=-4.17543 EndY=88 EndZ=0
    g4: LineSegment StartX=-4.17543 StartY=83 StartZ=0 EndX=-4.17543 EndY=73 EndZ=0
    g5: LineSegment StartX=5.82457 StartY=83 StartZ=0 EndX=5.82457 EndY=73 EndZ=0
    g6: ArcOfCircle CenterX=0.824572 CenterY=83 CenterZ=0 NormalX=0 NormalY=0 NormalZ=1 AngleXU=0 Radius=5 StartAngle=-3.6e-15 EndAngle=3.14159
    g7: ArcOfCircle CenterX=0.824572 CenterY=73 CenterZ=0 NormalX=0 NormalY=0 NormalZ=1 AngleXU=0 Radius=5 StartAngle=3.14159 EndAngle=6.28319
    g8: LineSegment StartX=-4.17543 StartY=83 StartZ=0 EndX=5.82457 EndY=83 EndZ=0
    g9: LineSegment StartX=-4.17543 StartY=73 StartZ=0 EndX=5.82457 EndY=73 EndZ=0
  constraints (30):
    c: Coincident(g0,g1)
    c: Coincident(g1,g2)
    c: Coincident(g2,g3)
    c: Coincident(g3,g0)
    c: Horizontal(g0)
    c: Horizontal(g2)
    c: Vertical(g1)
    c: Vertical(g3)
    c: DistanceX(g0,g0) = 10
    c: DistanceY(g3,g3) = 20
    c: PointOnObject(g4,g3)
    c: PointOnObject(g4,g3)
    c: PointOnObject(g5,g1)
    c: PointOnObject(g5,g1)
    c: Coincident(g6,g4)
    c: Coincident(g6,g5)
    c: Coincident(g7,g4)
    c: Coincident(g7,g5)
    c: Tangent(g6,g0)
    c: Tangent(g7,g2)
    c: Coincident(g8,g4)
    c: Coincident(g8,g5)
    c: Horizontal(g8)
    c: Coincident(g9,g4)
    c: Coincident(g9,g5)
    c: PointOnObject(g6,g8)
    c: PointOnObject(g7,g9)
    c: Horizontal(g9)
    c: DistanceY(g0,g-4) = 5
    c: DistanceX(g0,g-4) = 14
FEATURE [PartDesign::Pocket] Pocket007
  BaseFeature = -> Pocket006
  Direction = (-0.965926,0.258819,2e-16)
  Length = 5
  Length2 = 5
  Profile = -> Sketch011
  ReferenceAxis = -> Sketch011 [N_Axis]
  Type = 1
FEATURE [App::DocumentObjectGroup] Parts
FEATURE [PartDesign::CoordinateSystem] LCS_Origin
  AttacherType = Attacher::AttachEngine3D
  MapMode = 2
  Support = -> [X_Axis001]
FEATURE [App::DocumentObjectGroup] Constraints
FEATURE [App::FeaturePython] Variables  # WARN: FeaturePython — macro-defined, semantics opaque (R4)
  Type = App::PropertyContainer
FEATURE [App::DocumentObjectGroup] Configurations
FEATURE [PartDesign::CoordinateSystem] LCS_MLX
  AttacherType = Attacher::AttachEngine3D
  AttachmentOffset = pos=(0,0,0) rot=(0,0,-1;0.261799rad)
  MapMode = 11
  Placement = pos=(17.8247,29.7674,2) rot=(0,0,1;1.309rad)
  Support = -> [Hole]
  expr: .AttachmentOffset.Rotation.Yaw = Spreadsheet.slant * -1
FEATURE [PartDesign::CoordinateSystem] LCS_Raspi
  AttacherType = Attacher::AttachEngine3D
  AttachmentOffset = pos=(0,0,0) rot=(0,0,-1;0.261799rad)
  MapMode = 11
  Placement = pos=(8.32565,8.35314,2) rot=(0,0,1;1.309rad)
  Support = -> [Hole]
  expr: .AttachmentOffset.Rotation.Yaw = Spreadsheet.slant * -1
FEATURE [PartDesign::CoordinateSystem] LCS_Display
  AttacherType = Attacher::AttachEngine3D
  MapMode = 11
  Placement = pos=(-0.361561,-36,2) rot=(0,0,1;1.5708rad)
  Support = -> [Hole]
FEATURE [PartDesign::CoordinateSystem] LCS_beam
  AttacherType = Attacher::AttachEngine3D
  MapMode = 11
  Placement = pos=(-26.5323,32.8096,93) rot=(0,0,1;1.5708rad)
  Support = -> [Hole001]
FEATURE [Sketcher::SketchObject] Sketch012
  ExternalGeometry = -> [Pocket007]
  FullyConstrained = true
  MapMode = 5
  Placement = pos=(-28.1278,7.53681,0) rot=(0.677661,0.519988,0.519988;1.95044rad)
  Support = -> [Pocket007]
  expr: Constraints[12] = Spreadsheet.interface_screws_width
  expr: Constraints[13] = Spreadsheet.interface_screws_height
  expr: Constraints[18] = Spreadsheet.beams_width + Spreadsheet.interface_offset
  expr: Constraints[20] = Spreadsheet.screw_radius
  expr: Constraints[21] = Spreadsheet.screw_radius
  expr: Constraints[22] = Spreadsheet.screw_radius
  expr: Constraints[23] = Spreadsheet.screw_radius
  sketch-geometry (10):
    g0: Circle CenterX=-38.1754 CenterY=74 CenterZ=0 NormalX=0 NormalY=0 NormalZ=1 AngleXU=0 Radius=1.5
    g1: Circle CenterX=-38.1754 CenterY=19 CenterZ=0 NormalX=0 NormalY=0 NormalZ=1 AngleXU=0 Radius=1.5
    g2: Circle CenterX=-28.1754 CenterY=19 CenterZ=0 NormalX=0 NormalY=0 NormalZ=1 AngleXU=0 Radius=1.5
    g3: Circle CenterX=-28.1754 CenterY=74 CenterZ=0 NormalX=0 NormalY=0 NormalZ=1 AngleXU=0 Radius=1.5
    g4: LineSegment StartX=-38.1754 StartY=74 StartZ=0 EndX=-28.1754 EndY=74 EndZ=0
    g5: LineSegment StartX=-28.1754 StartY=74 StartZ=0 EndX=-28.1754 EndY=19 EndZ=0
    g6: LineSegment StartX=-28.1754 StartY=19 StartZ=0 EndX=-38.1754 EndY=19 EndZ=0
    g7: LineSegment StartX=-38.1754 StartY=19 StartZ=0 EndX=-38.1754 EndY=74 EndZ=0
    g8: LineSegment StartX=-33.1754 StartY=93 StartZ=0 EndX=-33.1754 EndY=0 EndZ=0
    g9: GeomPoint X=-33.1754 Y=46.5 Z=0
  constraints (24):
    c: Coincident(g4,g5)
    c: Coincident(g5,g6)
    c: Coincident(g6,g7)
    c: Coincident(g7,g4)
    c: Horizontal(g4)
    c: Horizontal(g6)
    c: Vertical(g5)
    c: Vertical(g7)
    c: Coincident(g0,g4)
    c: Coincident(g3,g4)
    c: Coincident(g1,g6)
    c: Coincident(g2,g5)
    c: DistanceY(g5,g5) = 55
    c: DistanceX(g4,g4) = 10
    c: PointOnObject(g8,g-3)
    c: PointOnObject(g8,g-1)
    c: Symmetric(g8,g8,g9)
    c: Vertical(g8)
    c: DistanceX(g-4,g8) = 12
    c: Symmetric(g0,g2,g9)
    c: Radius(g0) = 1.5
    c: Radius(g3) = 1.5
    c: Radius(g1) = 1.5
    c: Radius(g2) = 1.5
FEATURE [PartDesign::Hole] Hole002
  BaseFeature = -> Pocket007
  CustomThreadClearance = 0
  Depth = 358.646
  DepthType = 1
  Diameter = 3.4
  DrillForDepth = false
  DrillPoint = 1
  DrillPointAngle = 118
  HoleCutCountersinkAngle = 90
  HoleCutCustomValues = false
  HoleCutDepth = 0
  HoleCutDiameter = 6.1
  HoleCutType = 0
  ModelThread = false
  Profile = -> Sketch012
  Tapered = false
  TaperedAngle = 90
  ThreadClass = 0
  ThreadDepth = 358.646
  ThreadDepthType = 0
  ThreadDirection = 0
  ThreadFit = 0
  ThreadSize = 9
  ThreadType = 1
  Threaded = false
  UseCustomThreadClearance = false
FEATURE [Sketcher::SketchObject] Sketch013
  ExternalGeometry = -> [Hole002]
  FullyConstrained = true
  MapMode = 5
  Placement = pos=(-28.1278,7.53681,0) rot=(0.677661,0.519988,0.519988;1.95044rad)
  Support = -> [Hole002]
  sketch-geometry (28):
    g0: LineSegment StartX=-35.4254 StartY=75.5877 StartZ=0 EndX=-38.1754 EndY=77.1754 EndZ=0
    g1: LineSegment StartX=-38.1754 StartY=77.1754 StartZ=0 EndX=-40.9254 EndY=75.5877 EndZ=0
    g2: LineSegment StartX=-40.9254 StartY=75.5877 StartZ=0 EndX=-40.9254 EndY=72.4123 EndZ=0
    g3: LineSegment StartX=-40.9254 StartY=72.4123 StartZ=0 EndX=-38.1754 EndY=70.8246 EndZ=0
    g4: LineSegment StartX=-38.1754 StartY=70.8246 StartZ=0 EndX=-35.4254 EndY=72.4123 EndZ=0
    g5: LineSegment StartX=-35.4254 StartY=72.4123 StartZ=0 EndX=-35.4254 EndY=75.5877 EndZ=0
    g6: Circle CenterX=-38.1754 CenterY=74 CenterZ=0 NormalX=0 NormalY=0 NormalZ=1 AngleXU=0 Radius=3.17543
    g7: LineSegment StartX=-25.4254 StartY=75.5877 StartZ=0 EndX=-28.1754 EndY=77.1754 EndZ=0
    g8: LineSegment StartX=-28.1754 StartY=77.1754 StartZ=0 EndX=-30.9254 EndY=75.5877 EndZ=0
    g9: LineSegment StartX=-30.9254 StartY=75.5877 StartZ=0 EndX=-30.9254 EndY=72.4123 EndZ=0
    g10: LineSegment StartX=-30.9254 StartY=72.4123 StartZ=0 EndX=-28.1754 EndY=70.8246 EndZ=0
    g11: LineSegment StartX=-28.1754 StartY=70.8246 StartZ=0 EndX=-25.4254 EndY=72.4123 EndZ=0
    g12: LineSegment StartX=-25.4254 StartY=72.4123 StartZ=0 EndX=-25.4254 EndY=75.5877 EndZ=0
    g13: Circle CenterX=-28.1754 CenterY=74 CenterZ=0 NormalX=0 NormalY=0 NormalZ=1 AngleXU=0 Radius=3.17543
    g14: LineSegment StartX=-35.4254 StartY=20.5877 StartZ=0 EndX=-38.1754 EndY=22.1754 EndZ=0
    g15: LineSegment StartX=-38.1754 StartY=22.1754 StartZ=0 EndX=-40.9254 EndY=20.5877 EndZ=0
    g16: LineSegment StartX=-40.9254 StartY=20.5877 StartZ=0 EndX=-40.9254 EndY=17.4123 EndZ=0
    g17: LineSegment StartX=-40.9254 StartY=17.4123 StartZ=0 EndX=-38.1754 EndY=15.8246 EndZ=0
    g18: LineSegment StartX=-38.1754 StartY=15.8246 StartZ=0 EndX=-35.4254 EndY=17.4123 EndZ=0
    g19: LineSegment StartX=-35.4254 StartY=17.4123 StartZ=0 EndX=-35.4254 EndY=20.5877 EndZ=0
    g20: Circle CenterX=-38.1754 CenterY=19 CenterZ=0 NormalX=0 NormalY=0 NormalZ=1 AngleXU=0 Radius=3.17543
    g21: LineSegment StartX=-25.4254 StartY=20.5877 StartZ=0 EndX=-28.1754 EndY=22.1754 EndZ=0
    g22: LineSegment StartX=-28.1754 StartY=22.1754 StartZ=0 EndX=-30.9254 EndY=20.5877 EndZ=0
    g23: LineSegment StartX=-30.9254 StartY=20.5877 StartZ=0 EndX=-30.9254 EndY=17.4123 EndZ=0
    g24: LineSegment StartX=-30.9254 StartY=17.4123 StartZ=0 EndX=-28.1754 EndY=15.8246 EndZ=0
    g25: LineSegment StartX=-28.1754 StartY=15.8246 StartZ=0 EndX=-25.4254 EndY=17.4123 EndZ=0
    g26: LineSegment StartX=-25.4254 StartY=17.4123 StartZ=0 EndX=-25.4254 EndY=20.5877 EndZ=0
    g27: Circle CenterX=-28.1754 CenterY=19 CenterZ=0 NormalX=0 NormalY=0 NormalZ=1 AngleXU=0 Radius=3.17543
  constraints (64):
    c: Coincident(g0,g1)
    c: Coincident(g1,g2)
    c: Coincident(g2,g3)
    c: Coincident(g3,g4)
    c: Coincident(g4,g5)
    c: Coincident(g5,g0)
    c: Equal(g0, g1-g5) x5
    c: PointOnObject(g0,g6)
    c: PointOnObject(g1,g6)
    c: PointOnObject(g2,g6)
    c: PointOnObject(g3,g6)
    c: PointOnObject(g4,g6)
    c: PointOnObject(g5,g6)
    c: Coincident(g6,g-3)
    c: Coincident(g7,g8)
    c: Coincident(g8,g9)
    c: Coincident(g9,g10)
    c: Coincident(g10,g11)
    c: Coincident(g11,g12)
    c: Coincident(g12,g7)
    c: Equal(g7, g8-g12) x5
    c: PointOnObject(g7,g13)
    c: PointOnObject(g8,g13)
    c: PointOnObject(g9,g13)
    c: PointOnObject(g10,g13)
    c: PointOnObject(g11,g13)
    c: PointOnObject(g12,g13)
    c: Coincident(g13,g-4)
    c: Coincident(g14,g15)
    c: Coincident(g15,g16)
    c: Coincident(g16,g17)
    c: Coincident(g17,g18)
    c: Coincident(g18,g19)
    c: Coincident(g19,g14)
    c: Equal(g14, g15-g19) x5
    c: PointOnObject(g14,g20)
    c: PointOnObject(g15,g20)
    c: PointOnObject(g16,g20)
    c: PointOnObject(g17,g20)
    c: PointOnObject(g18,g20)
    c: PointOnObject(g19,g20)
    c: Coincident(g20,g-5)
    c: Coincident(g21,g22)
    c: Coincident(g22,g23)
    c: Coincident(g23,g24)
    c: Coincident(g24,g25)
    c: Coincident(g25,g26)
    c: Coincident(g26,g21)
    c: Equal(g21, g22-g26) x5
    c: PointOnObject(g21,g27)
    c: PointOnObject(g22,g27)
    c: PointOnObject(g23,g27)
    c: PointOnObject(g24,g27)
    c: PointOnObject(g25,g27)
    c: PointOnObject(g26,g27)
    c: Coincident(g27,g-6)
    c: Vertical(g5)
    c: Vertical(g9)
    c: Vertical(g19)
    c: Vertical(g23)
    c: DistanceX(g1,g0) = 5.5
    c: DistanceX(g8,g7) = 5.5
    c: DistanceX(g15,g14) = 5.5
    c: DistanceX(g22,g21) = 5.5
FEATURE [PartDesign::Pocket] Pocket008
  BaseFeature = -> Hole002
  Direction = (-0.965926,0.258819,1e-16)
  Length = 5
  Length2 = 5
  Profile = -> Sketch013
  ReferenceAxis = -> Sketch013 [N_Axis]
  Type = 0
FEATURE [Sketcher::SketchObject] Sketch014
  ExternalGeometry = -> [Pocket008]
  FullyConstrained = true
  MapMode = 5
  Placement = pos=(-39.653,10.625,0) rot=(-0.476905,0.621515,0.621515;4.0316rad)
  Support = -> [Pocket008]
  expr: Constraints[8] = Spreadsheet.interface_height + Spreadsheet.interface_clearance
  expr: Constraints[9] = Spreadsheet.interface_width + Spreadsheet.interface_clearance
  sketch-geometry (7):
    g0: LineSegment StartX=22.9254 StartY=79.25 StartZ=0 EndX=43.4254 EndY=79.25 EndZ=0
    g1: LineSegment StartX=43.4254 StartY=79.25 StartZ=0 EndX=43.4254 EndY=13.75 EndZ=0
    g2: LineSegment StartX=43.4254 StartY=13.75 StartZ=0 EndX=22.9254 EndY=13.75 EndZ=0
    g3: LineSegment StartX=22.9254 StartY=13.75 StartZ=0 EndX=22.9254 EndY=79.25 EndZ=0
    g4: LineSegment StartX=28.1754 StartY=74 StartZ=0 EndX=38.1754 EndY=19 EndZ=0
    g5: LineSegment StartX=38.1754 StartY=74 StartZ=0 EndX=28.1754 EndY=19 EndZ=0
    g6: GeomPoint X=33.1754 Y=46.5 Z=0
  constraints (17):
    c: Coincident(g0,g1)
    c: Coincident(g1,g2)
    c: Coincident(g2,g3)
    c: Coincident(g3,g0)
    c: Horizontal(g0)
    c: Horizontal(g2)
    c: Vertical(g1)
    c: Vertical(g3)
    c: DistanceX(g0,g0) = 20.5
    c: DistanceY(g3,g3) = 65.5
    c: Coincident(g4,g-3)
    c: Coincident(g4,g-6)
    c: Coincident(g5,g-4)
    c: Coincident(g5,g-5)
    c: PointOnObject(g6,g4)
    c: PointOnObject(g6,g5)
    c: Symmetric(g0,g1,g6)
FEATURE [PartDesign::Pocket] Pocket009
  BaseFeature = -> Pocket008
  Direction = (0.965926,-0.258819,-1e-16)
  Length = 2
  Length2 = 5
  Profile = -> Sketch014
  ReferenceAxis = -> Sketch014 [N_Axis]
  Type = 0
  expr: Length = Spreadsheet.walls_thickness
FEATURE [Sketcher::SketchObject] Sketch015
  ExternalGeometry = -> [Pocket009]
  FullyConstrained = true
  MapMode = 5
  Placement = pos=(0,0,0) rot=(1,0,0;3.14159rad)
  Support = -> [Pocket009]
  expr: Constraints[11] = Spreadsheet.pen_radius + Spreadsheet.pen_radius_tolerance
  expr: Constraints[15] = Spreadsheet.pen_hole_offset
  sketch-geometry (6):
    g0: LineSegment StartX=-32.0554 StartY=7.12153 StartZ=0 EndX=-43.5807 EndY=4.03334 EndZ=0
    g1: LineSegment StartX=-43.5807 StartY=4.03334 StartZ=0 EndX=-46.6689 EndY=15.5586 EndZ=0
    g2: LineSegment StartX=-46.6689 StartY=15.5586 StartZ=0 EndX=-35.1436 EndY=18.6468 EndZ=0
    g3: LineSegment StartX=-35.1436 StartY=18.6468 StartZ=0 EndX=-32.0554 EndY=7.12153 EndZ=0
    g4: Circle CenterX=-41.2611 CenterY=10.8313 CenterZ=0 NormalX=0 NormalY=0 NormalZ=1 AngleXU=0 Radius=2.7
    g5: LineSegment StartX=-45.1248 StartY=9.79598 StartZ=0 EndX=-41.2611 EndY=10.8313 EndZ=0
  constraints (16):
    c: Coincident(g0,g1)
    c: Coincident(g1,g2)
    c: Coincident(g2,g3)
    c: Coincident(g3,g0)
    c: Coincident(g0,g-4)
    c: PointOnObject(g2,g-3)
    c: PointOnObject(g0,g-6)
    c: PointOnObject(g0,g-4)
    c: PointOnObject(g1,g-6)
    c: Equal(g0,g3)
    c: Equal(g0,g1)
    c: Radius(g4) = 2.7
    c: Coincident(g5,g4)
    c: Perpendicular(g5,g1)
    c: Symmetric(g1,g0,g5)
    c: Distance(g5) = 4
FEATURE [PartDesign::Pocket] Pocket010
  BaseFeature = -> Pocket009
  Direction = (0,0,1)
  Length = 93
  Length2 = 5
  Profile = -> Sketch015
  ReferenceAxis = -> Sketch015 [N_Axis]
  Type = 0
  expr: Length = Spreadsheet.main_case_width - Spreadsheet.walls_thickness
FEATURE [Sketcher::SketchObject] Sketch016
  ExternalGeometry = -> [Pocket010]
  FullyConstrained = true
  MapMode = 5
  Placement = pos=(0,0,0) rot=(1,0,0;3.14159rad)
  Support = -> [Pocket010]
  sketch-geometry (4):
    g0: LineSegment StartX=-40.5623 StartY=8.22326 StartZ=0 EndX=-44.426 EndY=7.18798 EndZ=0
    g1: LineSegment StartX=-44.426 StartY=7.18798 StartZ=0 EndX=-45.8236 EndY=12.404 EndZ=0
    g2: LineSegment StartX=-45.8236 StartY=12.404 StartZ=0 EndX=-41.9599 EndY=13.4393 EndZ=0
    g3: LineSegment StartX=-41.9599 StartY=13.4393 StartZ=0 EndX=-40.5623 EndY=8.22326 EndZ=0
  constraints (12):
    c: Coincident(g0,g1)
    c: Coincident(g1,g2)
    c: Coincident(g2,g3)
    c: Coincident(g3,g0)
    c: PointOnObject(g0,g-4)
    c: PointOnObject(g1,g-4)
    c: PointOnObject(g2,g-3)
    c: PointOnObject(g0,g-3)
    c: PointOnObject(g-3,g3)
    c: Parallel(g3,g1)
    c: Parallel(g2,g0)
    c: Perpendicular(g2,g1)
FEATURE [PartDesign::Pocket] Pocket011
  BaseFeature = -> Pocket010
  Direction = (0,0,1)
  Length = 11.5
  Length2 = 5
  Profile = -> Sketch016
  ReferenceAxis = -> Sketch016 [N_Axis]
  Type = 0
  expr: Length = Spreadsheet.pen_grip_height
FEATURE [PartDesign::CoordinateSystem] LCS_interface
  AttacherType = Attacher::AttachEngine3D
  MapMode = 11
  Placement = pos=(-45.0135,-17.108,74) rot=(-0.476905,0.621515,0.621515;4.0316rad)
  Support = -> [Pocket011]
FEATURE [Sketcher::SketchObject] Sketch017
  ExternalGeometry = -> [Pocket011]
  FullyConstrained = true
  MapMode = 5
  Placement = pos=(-39.653,10.625,0) rot=(-0.476905,0.621515,0.621515;4.0316rad)
  Support = -> [Pocket011]
  sketch-geometry (2):
    g0: Circle CenterX=-24.8246 CenterY=86.95 CenterZ=0 NormalX=0 NormalY=0 NormalZ=1 AngleXU=0 Radius=1.05
    g1: Circle CenterX=40.1754 CenterY=86.95 CenterZ=0 NormalX=0 NormalY=0 NormalZ=1 AngleXU=0 Radius=1.05
  constraints (4):
    c: Symmetric(g-5,g-6,g0)
    c: Symmetric(g-9,g-10,g1)
    c: Tangent(g0,g-5)
    c: Tangent(g1,g-9)
FEATURE [PartDesign::Pocket] Pocket012
  BaseFeature = -> Pocket011
  Direction = (0.965926,-0.258819,-1e-16)
  Length = 2
  Length2 = 5
  Profile = -> Sketch017
  ReferenceAxis = -> Sketch017 [N_Axis]
  Type = 3
  UpToFace = -> Pocket011 [Face67]
  expr: Length = Spreadsheet.walls_thickness
FEATURE [Sketcher::SketchObject] Sketch018
  ExternalGeometry = -> [Pocket012]
  FullyConstrained = true
  MapMode = 5
  Placement = pos=(39.653,-10.625,0) rot=(0.677661,0.519988,0.519988;1.95044rad)
  Support = -> [Pocket012]
  sketch-geometry (2):
    g0: Circle CenterX=-19.2111 CenterY=86.95 CenterZ=0 NormalX=0 NormalY=0 NormalZ=1 AngleXU=0 Radius=1.05
    g1: Circle CenterX=25.7889 CenterY=86.95 CenterZ=0 NormalX=0 NormalY=0 NormalZ=1 AngleXU=0 Radius=1.05
  constraints (4):
    c: Symmetric(g-4,g-6,g0)
    c: Symmetric(g-8,g-10,g1)
    c: Tangent(g0,g-5)
    c: Tangent(g1,g-9)
FEATURE [PartDesign::Pocket] Pocket013
  BaseFeature = -> Pocket012
  Direction = (-0.965926,0.258819,-2e-16)
  Length = 0
  Length2 = 5
  Profile = -> Sketch018
  ReferenceAxis = -> Sketch018 [N_Axis]
  Type = 3
  UpToFace = -> Pocket012 [Face80]
FEATURE [PartDesign::Body] Body  label="Körper"
  Group = -> [Sketch,Pad,Sketch001,Pocket,Sketch002,Pocket001,Sketch003,Pocket002,Fillet,Sketch004,Hole,Sketch005,Pocket003,Sketch006,Pocket004,Sketch007,Pad001,Sketch008,Hole001,Sketch009,Pocket005,Sketch010,Pocket006,Sketch011,Pocket007,Sketch012,Hole002,Sketch013,Pocket008,Sketch014,Pocket009,Sketch015,Pocket010,Sketch016,Pocket011,Sketch017,Pocket012,Sketch018,Pocket013]
  Origin = -> Origin
  Tip = -> Pocket013
FEATURE [App::Part] Model
  AssemblyType = Part::Link
  Group = -> [LCS_Origin,Constraints,Variables,Configurations,Body,LCS_MLX,LCS_Raspi,LCS_Display,LCS_beam,LCS_interface]
  Origin = -> Origin001
  Type = Assembly
FEATURE [Mesh::Feature] Mesh  label="Körper (Meshed)"
---- part Parts/Casing_Lid_2.FCStd = doc fcstd_2cd67b6474e2 ----
FCSTD DOCUMENT  (FreeCAD 0.21R33668 +26 (Git))
Label: Casing_Lid_2
License: All rights reserved
LicenseURL: https://en.wikipedia.org/wiki/All_rights_reserved
objects: Sketcher::SketchObject×3, App::DocumentObjectGroup×3, PartDesign::Hole×2, PartDesign::CoordinateSystem×2, Spreadsheet::Sheet×1, PartDesign::Pad×1, PartDesign::Body×1, App::FeaturePython×1, App::Part×1, Mesh::Feature×1
note: 12 computed .brp shape members not serialized (recipe doc carries the construction recipe); baked Part::Feature solids carry a one-line shape summary decoded from their .brp
EXTERNAL_REF file=Casing2.FCStd obj=Spreadsheet

FEATURE [Sketcher::SketchObject] Sketch
  FullyConstrained = true
  MapMode = 5
  Support = -> [XY_Plane]
  expr: Constraints[7] = 90 ° - Spreadsheet.slant
  expr: Constraints[8] = Spreadsheet.main_case_length - Spreadsheet.walls_thickness - Spreadsheet.front_thickness - Spreadsheet.clearance
  expr: Constraints[9] = Spreadsheet.main_case_height - Spreadsheet.walls_thickness * 2 - Spreadsheet.clearance
  sketch-geometry (4):
    g0: LineSegment StartX=-52.6427 StartY=46.25 StartZ=0 EndX=27.8573 EndY=46.25 EndZ=0
    g1: LineSegment StartX=27.8573 StartY=46.25 StartZ=0 EndX=52.6427 EndY=-46.25 EndZ=0
    g2: LineSegment StartX=52.6427 StartY=-46.25 StartZ=0 EndX=-27.8573 EndY=-46.25 EndZ=0
    g3: LineSegment StartX=-27.8573 StartY=-46.25 StartZ=0 EndX=-52.6427 EndY=46.25 EndZ=0
  constraints (10):
    c: Coincident(g0,g1)
    c: Coincident(g1,g2)
    c: Coincident(g2,g3)
    c: Coincident(g3,g0)
    c: Horizontal(g0)
    c: Symmetric(g0,g1,g-1)
    c: Symmetric(g0,g2,g-1)
    c: Angle(g1,g2) = 1.309
    c: DistanceY(g3,g3) = 92.5
    c: DistanceX(g0,g0) = 80.5
FEATURE [Spreadsheet::Sheet] Spreadsheet
  cells = B2='slant; C2(slant)==<<Casing2>>#Spreadsheet.slant; E2='main_case_width; F2(main_case_width)==<<Casing2>>#Spreadsheet.main_case_width; H2='display_width; I2(display_width)==<<Casing2>>#Spreadsheet.display_width; B3='walls_thickness; C3(walls_thickness)==<<Casing2>>#Spreadsheet.walls_thickness; E3='main_case_height; F3(main_case_height)==<<Casing2>>#Spreadsheet.main_case_height; H3='display_height; I3(display_height)==<<Casing2>>#Spreadsheet.display_height; B4='screw_radius; C4(screw_radius)==<<Casing2>>#Spreadsheet.screw_radius; E4='main_case_length; F4(main_case_length)==<<Casing2>>#Spreadsheet.main_case_length; B5='front_thickness; C5(front_thickness)==<<Casing2>>#Spreadsheet.front_thickness; H5='mlx_cam_height; I5(mlx_cam_height)==<<Casing2>>#Spreadsheet.mlx_cam_height; B6='clearance; C6(clearance)==0.5 mm; E6='mlx_carrier_height; F6(mlx_carrier_height)==<<Casing2>>#Spreadsheet.mlx_carrier_height; H6='mlx_extra_space; I6(mlx_extra_space)==<<Casing2>>#Spreadsheet.mlx_extra_space; E7='mlx_carrier_width; F7(mlx_carrier_width)==<<Casing2>>#Spreadsheet.mlx_carrier_width; H7='mlx_radius; I7(mlx_radius)==<<Casing2>>#Spreadsheet.mlx_extra_space; B9='display_guard_depth; C9(display_guard_depth)==<<Casing2>>#Spreadsheet.display_guard_depth; E9='beams_width; F9(beams_width)==<<Casing2>>#Spreadsheet.beams_width; H9='raspi_carrier_hole_dist; I9(raspi_carrier_hole_dist)==<<Casing2>>#Spreadsheet.raspi_carrier_hole_dist; B10='display_guard_size; C10(display_guard_size)==<<Casing2>>#Spreadsheet.display_guard_size; E10='beams_height; F10(beams_height)==<<Casing2>>#Spreadsheet.beams_height; H10='raspi_carrier_height; I10(raspi_carrier_height)==<<Casing2>>#Spreadsheet.raspi_carrier_height; B11='display_clearance; C11(display_clearance)==<<Casing2>>#Spreadsheet.display_clearance; H11='raspi_carrier_depth; I11(raspi_carrier_depth)==<<Casing2>>#Spreadsheet.raspi_carrier_depth; B12='display_hole_depth; C12(display_hole_depth)==<<Casing2>>#Spreadsheet.display_hole_depth; E12='beam_LB_offset; F12(beam_LB_offset)==<<Casing2>>#Spreadsheet.beam_LB_offset; E13='beam_LF_offset; F13(beam_LF_offset)==<<Casing2>>#Spreadsheet.beam_LF_offset; B14='display_thickness; C14(display_thickness)==<<Casing2>>#Spreadsheet.display_thickness; E14='beam_UB_offset; F14(beam_UB_offset)==<<Casing2>>#Spreadsheet.beam_UB_offset; B15='display_carrier_height; C15(display_carrier_height)==<<Casing2>>#Spreadsheet.display_carrier_height; E15='beam_UF_offset; F15(beam_UF_offset)==<<Casing2>>#Spreadsheet.beam_UF_offset; B17='display_carrier_hole_dist; C17(display_carrier_hole_dist)==<<Casing2>>#Spreadsheet.display_carrier_hole_dist; B18='display_carrier_offset; C18(display_carrier_offset)==<<Casing2>>#Spreadsheet.display_carrier_offset
FEATURE [PartDesign::Pad] Pad
  Direction = (0,0,1)
  Length = 2
  Length2 = 10
  Profile = -> Sketch
  ReferenceAxis = -> Sketch [N_Axis]
  Type = 0
  expr: Length = Spreadsheet.walls_thickness
FEATURE [Sketcher::SketchObject] Sketch001
  FullyConstrained = true
  MapMode = 5
  Placement = pos=(0,0,2) rot=(0,0,1;0rad)
  Support = -> [Pad]
  expr: Constraints[25] = Spreadsheet.mlx_cam_height + Spreadsheet.front_thickness + Spreadsheet.mlx_extra_space
  expr: Constraints[26] = Spreadsheet.display_carrier_offset
  expr: Constraints[27] = Spreadsheet.display_carrier_hole_dist
  expr: Constraints[28] = Spreadsheet.walls_thickness
  expr: Constraints[29] = Spreadsheet.raspi_carrier_height
  expr: Constraints[30] = Spreadsheet.raspi_carrier_hole_dist
  expr: Constraints[32] = Spreadsheet.screw_radius
  expr: Constraints[33] = Spreadsheet.screw_radius
  expr: Constraints[34] = Spreadsheet.screw_radius
  expr: Constraints[35] = Spreadsheet.screw_radius
  expr: Constraints[36] = Spreadsheet.screw_radius
  expr: Constraints[37] = Spreadsheet.screw_radius
  expr: Constraints[40] = Spreadsheet.front_thickness
  expr: Constraints[43] = Spreadsheet.walls_thickness / cos(Spreadsheet.slant)
  expr: Constraints[47] = Spreadsheet.walls_thickness / cos(Spreadsheet.slant)
  expr: Constraints[59] = Spreadsheet.mlx_carrier_height - Spreadsheet.mlx_carrier_width
  expr: Constraints[5] = 90 ° - Spreadsheet.slant
  expr: Constraints[60] = 90 ° - Spreadsheet.slant
  expr: Constraints[8] = Spreadsheet.main_case_length - Spreadsheet.walls_thickness - Spreadsheet.front_thickness
  expr: Constraints[9] = Spreadsheet.main_case_height - Spreadsheet.walls_thickness * 2
  sketch-geometry (24):
    g0: LineSegment StartX=-52.9596 StartY=46.5 StartZ=0 EndX=28.0404 EndY=46.5 EndZ=0
    g1: LineSegment StartX=28.0404 StartY=46.5 StartZ=0 EndX=52.9596 EndY=-46.5 EndZ=0
    g2: LineSegment StartX=52.9596 StartY=-46.5 StartZ=0 EndX=-28.0404 EndY=-46.5 EndZ=0
    g3: LineSegment StartX=-28.0404 StartY=-46.5 StartZ=0 EndX=-52.9596 EndY=46.5 EndZ=0
    g4: LineSegment StartX=-15.7177 StartY=51.5 StartZ=0 EndX=-10.8276 EndY=33.25 EndZ=0
    g5: LineSegment StartX=-18.2266 StartY=31.2674 StartZ=0 EndX=-3.42864 EndY=35.2326 EndZ=0
    g6: LineSegment StartX=12.4596 StartY=-46.5 StartZ=0 EndX=12.4596 EndY=-34.5 EndZ=0
    g7: LineSegment StartX=-0.0403626 StartY=-34.5 StartZ=0 EndX=24.9596 EndY=-34.5 EndZ=0
    g8: LineSegment StartX=34.7391 StartY=21.5 StartZ=0 EndX=-26.1142 EndY=5.1944 EndZ=0
    g9: GeomPoint X=32.8072 Y=20.9824 Z=0
    g10: GeomPoint X=3.3465 Y=13.0884 Z=0
    g11: Circle CenterX=-3.42864 CenterY=35.2326 CenterZ=0 NormalX=0 NormalY=0 NormalZ=1 AngleXU=0 Radius=1.5
    g12: Circle CenterX=-18.2266 CenterY=31.2674 CenterZ=0 NormalX=0 NormalY=0 NormalZ=1 AngleXU=0 Radius=1.5
    g13: Circle CenterX=15.4206 CenterY=16.3236 CenterZ=0 NormalX=0 NormalY=0 NormalZ=1 AngleXU=0 Radius=1.5
    g14: Circle CenterX=-8.72757 CenterY=9.85314 CenterZ=0 NormalX=0 NormalY=0 NormalZ=1 AngleXU=0 Radius=1.5
    g15: Circle CenterX=24.9596 CenterY=-34.5 CenterZ=0 NormalX=0 NormalY=0 NormalZ=1 AngleXU=0 Radius=1.5
    g16: Circle CenterX=-0.0403626 CenterY=-34.5 CenterZ=0 NormalX=0 NormalY=0 NormalZ=1 AngleXU=0 Radius=1.5
    g17: LineSegment StartX=-52.9596 StartY=46.5 StartZ=0 EndX=-54.2994 EndY=51.5 EndZ=0
    g18: LineSegment StartX=-56.3699 StartY=51.5 StartZ=0 EndX=28.7712 EndY=51.5 EndZ=0
    g19: LineSegment StartX=28.0404 StartY=46.5 StartZ=0 EndX=26.7006 EndY=51.5 EndZ=0
    g20: ArcOfCircle CenterX=24.9345 CenterY=46.5 CenterZ=0 NormalX=0 NormalY=0 NormalZ=1 AngleXU=0 Radius=5 StartAngle=0.261799 EndAngle=1.5708
    g21: LineSegment StartX=28.7712 StartY=51.5 StartZ=0 EndX=29.7642 EndY=47.7941 EndZ=0
    g22: LineSegment StartX=24.9345 StartY=51.5 StartZ=0 EndX=28.7712 EndY=51.5 EndZ=0
    g23: GeomPoint X=-15.7177 Y=51.5 Z=0
  constraints (61):
    c: Coincident(g0,g1)
    c: Coincident(g1,g2)
    c: Coincident(g2,g3)
    c: Coincident(g3,g0)
    c: Horizontal(g0)
    c: Angle(g1,g2) = 1.309
    c: Symmetric(g0,g1,g-1)
    c: Symmetric(g0,g2,g-1)
    c: DistanceY(g3,g3) = 93
    c: DistanceX(g0,g0) = 81
    c: Vertical(g6)
    c: Horizontal(g7)
    c: Symmetric(g5,g5,g4)
    c: Symmetric(g1,g2,g6)
    c: Symmetric(g7,g7,g6)
    c: PointOnObject(g8,g1)
    c: PointOnObject(g9,g8)
    c: Symmetric(g9,g8,g10)
    c: Coincident(g11,g5)
    c: Coincident(g12,g5)
    c: PointOnObject(g14,g8)
    c: Coincident(g15,g7)
    c: Coincident(g16,g7)
    c: Symmetric(g13,g14,g10)
    c: Perpendicular(g8,g1)
    c: DistanceY(g4,g4) = 18.25
    c: DistanceY(g6,g6) = 12
    c: DistanceX(g7,g7) = 25
    c: Distance(g9,g8) = 2
    c: Distance(g9,g8) = 61
    c: Distance(g13,g14) = 25
    c: DistanceY(g8,g0) = 25
    c: Radius(g12) = 1.5
    c: Radius(g11) = 1.5
    c: Radius(g14) = 1.5
    c: Radius(g13) = 1.5
    c: Radius(g16) = 1.5
    c: Radius(g15) = 1.5
    c: Coincident(g17,g0)
    c: Parallel(g3,g17)
    c: DistanceY(g0,g17) = 5
    c: Horizontal(g18)
    c: PointOnObject(g17,g18)
    c: DistanceX(g18,g17) = 2.07055
    c: Coincident(g19,g0)
    c: PointOnObject(g19,g18)
    c: Parallel(g19,g1)
    c: DistanceX(g19,g18) = 2.07055
    c: Radius(g20) = 5
    c: PointOnObject(g20,g18)
    c: Coincident(g21,g18)
    c: Parallel(g21,g19)
    c: Coincident(g22,g20)
    c: Coincident(g22,g18)
    c: Equal(g22,g21)
    c: Tangent(g20,g21) = 1.5708
    c: Symmetric(g18,g20,g23)
    c: Coincident(g4,g23)
    c: Perpendicular(g5,g4)
    c: Distance(g5) = 15.32
    c: Angle(g4,g18) = 1.309
FEATURE [PartDesign::Hole] Hole
  BaseFeature = -> Pad
  CustomThreadClearance = 0
  Depth = 281.498
  DepthType = 1
  Diameter = 3.4
  DrillForDepth = false
  DrillPoint = 1
  DrillPointAngle = 118
  HoleCutCountersinkAngle = 90
  HoleCutCustomValues = false
  HoleCutDepth = 0
  HoleCutDiameter = 6.1
  HoleCutType = 0
  ModelThread = false
  Profile = -> Sketch001
  Tapered = false
  TaperedAngle = 90
  ThreadClass = 0
  ThreadDepth = 281.498
  ThreadDepthType = 0
  ThreadDirection = 0
  ThreadFit = 0
  ThreadSize = 9
  ThreadType = 1
  Threaded = false
  UseCustomThreadClearance = false
FEATURE [Sketcher::SketchObject] Sketch002
  FullyConstrained = true
  MapMode = 5
  Placement = pos=(0,0,2) rot=(0,0,1;0rad)
  Support = -> [Hole]
  expr: Constraints[46] = Spreadsheet.beams_height
  expr: Constraints[47] = Spreadsheet.beams_height
  expr: Constraints[48] = Spreadsheet.beams_height
  expr: Constraints[49] = Spreadsheet.beams_height
  expr: Constraints[50] = Spreadsheet.beams_width
  expr: Constraints[51] = Spreadsheet.beams_width
  expr: Constraints[52] = Spreadsheet.beams_width
  expr: Constraints[53] = Spreadsheet.beams_width
  expr: Constraints[58] = Spreadsheet.screw_radius
  expr: Constraints[59] = Spreadsheet.screw_radius
  expr: Constraints[60] = Spreadsheet.screw_radius
  expr: Constraints[61] = Spreadsheet.screw_radius
  expr: Constraints[62] = Spreadsheet.beam_UF_offset
  expr: Constraints[63] = Spreadsheet.beam_UB_offset
  expr: Constraints[64] = Spreadsheet.beam_LF_offset
  expr: Constraints[65] = Spreadsheet.beam_LB_offset
  expr: Constraints[7] = 90 ° - Spreadsheet.slant
  expr: Constraints[8] = Spreadsheet.main_case_length - Spreadsheet.walls_thickness - Spreadsheet.front_thickness
  expr: Constraints[9] = Spreadsheet.main_case_height - Spreadsheet.walls_thickness * 2
  sketch-geometry (24):
    g0: LineSegment StartX=-52.9596 StartY=46.5 StartZ=0 EndX=28.0404 EndY=46.5 EndZ=0
    g1: LineSegment StartX=28.0404 StartY=46.5 StartZ=0 EndX=52.9596 EndY=-46.5 EndZ=0
    g2: LineSegment StartX=52.9596 StartY=-46.5 StartZ=0 EndX=-28.0404 EndY=-46.5 EndZ=0
    g3: LineSegment StartX=-28.0404 StartY=-46.5 StartZ=0 EndX=-52.9596 EndY=46.5 EndZ=0
    g4: Circle CenterX=-40.034 CenterY=17.5793 CenterZ=0 NormalX=0 NormalY=0 NormalZ=1 AngleXU=0 Radius=1.5
    g5: Circle CenterX=-28.3871 CenterY=-25.8874 CenterZ=0 NormalX=0 NormalY=0 NormalZ=1 AngleXU=0 Radius=1.5
    g6: Circle CenterX=42.9536 CenterY=-28.4756 CenterZ=0 NormalX=0 NormalY=0 NormalZ=1 AngleXU=0 Radius=1.5
    g7: Circle CenterX=26.1304 CenterY=34.3096 CenterZ=0 NormalX=0 NormalY=0 NormalZ=1 AngleXU=0 Radius=1.5
    g8: LineSegment StartX=-46.1577 StartY=21.1148 StartZ=0 EndX=-36.4984 EndY=23.703 EndZ=0
    g9: LineSegment StartX=-36.4984 StartY=23.703 StartZ=0 EndX=-33.9102 EndY=14.0437 EndZ=0
    g10: LineSegment StartX=-33.9102 StartY=14.0437 StartZ=0 EndX=-43.5695 EndY=11.4555 EndZ=0
    g11: LineSegment StartX=-43.5695 StartY=11.4555 StartZ=0 EndX=-46.1577 EndY=21.1148 EndZ=0
    g12: LineSegment StartX=-34.5108 StartY=-22.3519 StartZ=0 EndX=-24.8516 EndY=-19.7637 EndZ=0
    g13: LineSegment StartX=-24.8516 StartY=-19.7637 StartZ=0 EndX=-22.2634 EndY=-29.4229 EndZ=0
    g14: LineSegment StartX=-22.2634 StartY=-29.4229 StartZ=0 EndX=-31.9226 EndY=-32.0111 EndZ=0
    g15: LineSegment StartX=-31.9226 StartY=-32.0111 StartZ=0 EndX=-34.5108 EndY=-22.3519 EndZ=0
    g16: LineSegment StartX=36.8299 StartY=-24.94 StartZ=0 EndX=46.4892 EndY=-22.3519 EndZ=0
    g17: LineSegment StartX=46.4892 StartY=-22.3519 StartZ=0 EndX=49.0774 EndY=-32.0111 EndZ=0
    g18: LineSegment StartX=49.0774 StartY=-32.0111 StartZ=0 EndX=39.4181 EndY=-34.5993 EndZ=0
    g19: LineSegment StartX=39.4181 StartY=-34.5993 StartZ=0 EndX=36.8299 EndY=-24.94 EndZ=0
    g20: LineSegment StartX=20.0067 StartY=37.8451 StartZ=0 EndX=29.6659 EndY=40.4333 EndZ=0
    g21: LineSegment StartX=29.6659 StartY=40.4333 StartZ=0 EndX=32.2541 EndY=30.7741 EndZ=0
    g22: LineSegment StartX=32.2541 StartY=30.7741 StartZ=0 EndX=22.5949 EndY=28.1859 EndZ=0
    g23: LineSegment StartX=22.5949 StartY=28.1859 StartZ=0 EndX=20.0067 EndY=37.8451 EndZ=0
  constraints (66):
    c: Coincident(g0,g1)
    c: Coincident(g1,g2)
    c: Coincident(g2,g3)
    c: Coincident(g3,g0)
    c: Horizontal(g0)
    c: Symmetric(g0,g2,g-1)
    c: Symmetric(g0,g1,g-1)
    c: Angle(g1,g2) = 1.309
    c: DistanceY(g3,g3) = 93
    c: DistanceX(g0,g0) = 81
    c: Coincident(g8,g9)
    c: Coincident(g9,g10)
    c: Coincident(g10,g11)
    c: Coincident(g11,g8)
    c: Coincident(g12,g13)
    c: Coincident(g13,g14)
    c: Coincident(g14,g15)
    c: Coincident(g15,g12)
    c: Coincident(g16,g17)
    c: Coincident(g17,g18)
    c: Coincident(g18,g19)
    c: Coincident(g19,g16)
    c: Coincident(g20,g21)
    c: Coincident(g21,g22)
    c: Coincident(g22,g23)
    c: Coincident(g23,g20)
    c: PointOnObject(g8,g3)
    c: PointOnObject(g10,g3)
    c: PointOnObject(g12,g3)
    c: PointOnObject(g14,g3)
    c: PointOnObject(g16,g1)
    c: PointOnObject(g17,g1)
    c: PointOnObject(g20,g1)
    c: PointOnObject(g21,g1)
    c: Equal(g11,g9)
    c: Equal(g15,g13)
    c: Equal(g17,g19)
    c: Equal(g21,g23)
    c: Parallel(g3,g9)
    c: Parallel(g3,g13)
    c: Parallel(g1,g19)
    c: Parallel(g1,g23)
    c: Perpendicular(g8,g3)
    c: Perpendicular(g12,g3)
    c: Perpendicular(g20,g1)
    c: Perpendicular(g16,g1)
    c: Distance(g8) = 10
    c: Distance(g12) = 10
    c: Distance(g16) = 10
    c: Distance(g20) = 10
    c: Distance(g9) = 10
    c: Distance(g13) = 10
    c: Distance(g23) = 10
    c: Distance(g19) = 10
    c: Symmetric(g8,g9,g4)
    c: Symmetric(g12,g13,g5)
    c: Symmetric(g20,g21,g7)
    c: Symmetric(g16,g17,g6)
    c: Radius(g4) = 1.5
    c: Radius(g5) = 1.5
    c: Radius(g7) = 1.5
    c: Radius(g6) = 1.5
    c: Distance(g14,g2) = 15
    c: Distance(g10,g2) = 60
    c: Distance(g1,g17) = 15
    c: Distance(g21,g1) = 80
FEATURE [PartDesign::Hole] Hole001
  BaseFeature = -> Hole
  CustomThreadClearance = 0
  Depth = 25
  DepthType = 0
  Diameter = 3.4
  DrillForDepth = false
  DrillPoint = 1
  DrillPointAngle = 118
  HoleCutCountersinkAngle = 90
  HoleCutCustomValues = false
  HoleCutDepth = 0
  HoleCutDiameter = 6.1
  HoleCutType = 0
  ModelThread = false
  Profile = -> Sketch002
  Tapered = false
  TaperedAngle = 90
  ThreadClass = 0
  ThreadDepth = 25
  ThreadDepthType = 0
  ThreadDirection = 0
  ThreadFit = 0
  ThreadSize = 9
  ThreadType = 1
  Threaded = false
  UseCustomThreadClearance = false
FEATURE [PartDesign::Body] Body  label="Körper"
  Group = -> [Sketch,Pad,Sketch001,Hole,Sketch002,Hole001]
  Origin = -> Origin
  Tip = -> Hole001
FEATURE [App::DocumentObjectGroup] Parts
FEATURE [PartDesign::CoordinateSystem] LCS_Origin
  AttacherType = Attacher::AttachEngine3D
  MapMode = 2
  Support = -> [X_Axis001]
FEATURE [App::DocumentObjectGroup] Constraints
FEATURE [App::FeaturePython] Variables  # WARN: FeaturePython — macro-defined, semantics opaque (R4)
  Type = App::PropertyContainer
FEATURE [App::DocumentObjectGroup] Configurations
FEATURE [PartDesign::CoordinateSystem] LCS_screw
  AttacherType = Attacher::AttachEngine3D
  MapMode = 11
  Placement = pos=(26.1304,34.3096,2) rot=(0,0,1;1.5708rad)
  Support = -> [Hole001]
FEATURE [App::Part] Model
  AssemblyType = Part::Link
  Group = -> [LCS_Origin,Constraints,Variables,Configurations,Body,LCS_screw]
  Origin = -> Origin001
  Type = Assembly
FEATURE [Mesh::Feature] Mesh  label="Körper (Meshed)"
---- part Parts/Display_Berrybase.FCStd = doc fcstd_15dcf9297b93 ----
FCSTD DOCUMENT  (FreeCAD 0.21R33668 +26 (Git))
Label: Display_Berrybase
License: All rights reserved
LicenseURL: http://en.wikipedia.org/wiki/All_rights_reserved
objects: App::DocumentObjectGroup×3, Sketcher::SketchObject×2, PartDesign::Pad×2, PartDesign::CoordinateSystem×2, Spreadsheet::Sheet×1, App::FeaturePython×1, PartDesign::Body×1, App::Part×1
note: 9 computed .brp shape members not serialized (recipe doc carries the construction recipe); baked Part::Feature solids carry a one-line shape summary decoded from their .brp

FEATURE [Sketcher::SketchObject] Sketch
  FullyConstrained = true
  MapMode = 5
  Support = -> [XY_Plane]
  expr: Constraints[7] = <<Spreadsheet>>.width
  expr: Constraints[8] = <<Spreadsheet>>.height
  sketch-geometry (4):
    g0: LineSegment StartX=-42.26 StartY=27.63 StartZ=0 EndX=42.26 EndY=27.63 EndZ=0
    g1: LineSegment StartX=42.26 StartY=27.63 StartZ=0 EndX=42.26 EndY=-27.63 EndZ=0
    g2: LineSegment StartX=42.26 StartY=-27.63 StartZ=0 EndX=-42.26 EndY=-27.63 EndZ=0
    g3: LineSegment StartX=-42.26 StartY=-27.63 StartZ=0 EndX=-42.26 EndY=27.63 EndZ=0
  constraints (9):
    c: Coincident(g0,g1)
    c: Coincident(g1,g2)
    c: Coincident(g2,g3)
    c: Coincident(g3,g0)
    c: Symmetric(g0,g0,g-2)
    c: Symmetric(g0,g2,g-1)
    c: Symmetric(g0,g1,g-1)
    c: DistanceX(g0,g0) = 84.52
    c: DistanceY(g3,g3) = 55.26
FEATURE [PartDesign::Pad] Pad
  Direction = (0,0,1)
  Length = 6
  Length2 = 10
  Profile = -> Sketch
  ReferenceAxis = -> Sketch [N_Axis]
  Reversed = true
  Type = 0
  expr: Length = <<Spreadsheet>>.thickness
FEATURE [Spreadsheet::Sheet] Spreadsheet
  cells = B2='width; C2(width)==84.52 mm; B3='height; C3(height)==55.26 mm; B4='thickness; C4(thickness)==6 mm; B5='connector_width; C5(connector_width)==34 mm; B6='connector_height; C6(connector_height)==4 mm; B7='connector_length; C7(connector_length)==14 mm; B8='connector_offset_x; C8(connector_offset_x)==7 mm; B9='connector_offset_y; C9(connector_offset_y)==1 mm
FEATURE [App::DocumentObjectGroup] Parts
FEATURE [PartDesign::CoordinateSystem] LCS_Origin
  AttacherType = Attacher::AttachEngine3D
  MapMode = 2
  Support = -> [X_Axis001]
FEATURE [App::DocumentObjectGroup] Constraints
FEATURE [App::FeaturePython] Variables  # WARN: FeaturePython — macro-defined, semantics opaque (R4)
  Type = App::PropertyContainer
FEATURE [App::DocumentObjectGroup] Configurations
FEATURE [Sketcher::SketchObject] Sketch001
  ExternalGeometry = -> [Pad]
  FullyConstrained = true
  MapMode = 5
  Support = -> [Pad]
  expr: Constraints[10] = <<Spreadsheet>>.connector_width
  expr: Constraints[11] = <<Spreadsheet>>.connector_height
  expr: Constraints[8] = <<Spreadsheet>>.connector_offset_x
  expr: Constraints[9] = <<Spreadsheet>>.connector_offset_y
  sketch-geometry (4):
    g0: LineSegment StartX=1.26 StartY=26.63 StartZ=0 EndX=35.26 EndY=26.63 EndZ=0
    g1: LineSegment StartX=35.26 StartY=26.63 StartZ=0 EndX=35.26 EndY=22.63 EndZ=0
    g2: LineSegment StartX=35.26 StartY=22.63 StartZ=0 EndX=1.26 EndY=22.63 EndZ=0
    g3: LineSegment StartX=1.26 StartY=22.63 StartZ=0 EndX=1.26 EndY=26.63 EndZ=0
  constraints (12):
    c: Coincident(g0,g1)
    c: Coincident(g1,g2)
    c: Coincident(g2,g3)
    c: Coincident(g3,g0)
    c: Horizontal(g0)
    c: Horizontal(g2)
    c: Vertical(g1)
    c: Vertical(g3)
    c: DistanceX(g0,g-4) = 7
    c: DistanceY(g0,g-4) = 1
    c: DistanceX(g0,g0) = 34
    c: DistanceY(g3,g3) = 4
FEATURE [PartDesign::Pad] Pad001
  BaseFeature = -> Pad
  Direction = (0,0,1)
  Length = 14
  Length2 = 10
  Profile = -> Sketch001
  ReferenceAxis = -> Sketch001 [N_Axis]
  Type = 0
  expr: Length = <<Spreadsheet>>.connector_length
FEATURE [PartDesign::Body] Body
  Group = -> [Sketch,Pad,Sketch001,Pad001]
  Origin = -> Origin
  Tip = -> Pad001
FEATURE [PartDesign::CoordinateSystem] LCS_Connector
  AttacherType = Attacher::AttachEngine3D
  MapMode = 1
  Placement = pos=(35.26,26.63,0) rot=(0,0,1;0rad)
  Support = -> [Pad001]
FEATURE [App::Part] Model
  AssemblyType = Part::Link
  Group = -> [LCS_Origin,Constraints,Variables,Configurations,Body,LCS_Connector]
  Origin = -> Origin001
  Type = Assembly
---- part Parts/Handgrip.FCStd = doc fcstd_73576bd97c64 ----
FCSTD DOCUMENT  (FreeCAD 0.21R33668 +26 (Git))
Label: Handgrip
License: All rights reserved
LicenseURL: https://en.wikipedia.org/wiki/All_rights_reserved
objects: Sketcher::SketchObject×4, PartDesign::Fillet×4, App::DocumentObjectGroup×3, PartDesign::Pad×2, PartDesign::CoordinateSystem×2, Spreadsheet::Sheet×1, PartDesign::Hole×1, PartDesign::Pocket×1, App::FeaturePython×1, PartDesign::Chamfer×1, PartDesign::Body×1, App::Part×1, Mesh::Feature×1
note: 25 computed .brp shape members not serialized (recipe doc carries the construction recipe); baked Part::Feature solids carry a one-line shape summary decoded from their .brp
EXTERNAL_REF file=Casing2.FCStd obj=Spreadsheet

FEATURE [Spreadsheet::Sheet] Spreadsheet
  cells = B2='interface_width; C2(interface_width)==<<Casing2>>#Spreadsheet.interface_width; E2='handgrip_width; F2(handgrip_width)==40 mm; B3='interface_height; C3(interface_height)==<<Casing2>>#Spreadsheet.beams_width * 2; E3='handgrip_depth; F3(handgrip_depth)==40 mm; B4='interface_thickness; C4(interface_thickness)==<<Casing2>>#Spreadsheet.walls_thickness; E4='handgrip_length; F4(handgrip_length)==100 mm; B5='screw_radius; C5(screw_radius)==<<Casing2>>#Spreadsheet.screw_radius; B6='slant; C6(slant)==<<Casing2>>#Spreadsheet.slant
FEATURE [Sketcher::SketchObject] Sketch
  FullyConstrained = true
  MapMode = 5
  Support = -> [XY_Plane]
  expr: Constraints[10] = Spreadsheet.interface_height
  expr: Constraints[9] = Spreadsheet.interface_width
  sketch-geometry (4):
    g0: LineSegment StartX=-32.5 StartY=10 StartZ=0 EndX=32.5 EndY=10 EndZ=0
    g1: LineSegment StartX=32.5 StartY=10 StartZ=0 EndX=32.5 EndY=-10 EndZ=0
    g2: LineSegment StartX=32.5 StartY=-10 StartZ=0 EndX=-32.5 EndY=-10 EndZ=0
    g3: LineSegment StartX=-32.5 StartY=-10 StartZ=0 EndX=-32.5 EndY=10 EndZ=0
  constraints (11):
    c: Coincident(g0,g1)
    c: Coincident(g1,g2)
    c: Coincident(g2,g3)
    c: Coincident(g3,g0)
    c: Horizontal(g0)
    c: Horizontal(g2)
    c: Vertical(g1)
    c: Vertical(g3)
    c: Symmetric(g2,g0,g-1)
    c: DistanceX(g0,g0) = 65
    c: DistanceY(g3,g3) = 20
FEATURE [PartDesign::Pad] Pad
  Direction = (0,0,1)
  Length = 2
  Length2 = 10
  Profile = -> Sketch
  ReferenceAxis = -> Sketch [N_Axis]
  Type = 0
  expr: Length = Spreadsheet.interface_thickness
FEATURE [Sketcher::SketchObject] Sketch001
  FullyConstrained = true
  MapMode = 5
  Placement = pos=(0,0,0) rot=(1,0,0;3.14159rad)
  Support = -> [Pad]
  expr: Constraints[0] = Spreadsheet.screw_radius
  expr: Constraints[13] = Spreadsheet.interface_width
  expr: Constraints[14] = Spreadsheet.interface_height
  expr: Constraints[15] = Spreadsheet.interface_height / 4
  expr: Constraints[16] = Spreadsheet.interface_height / 4
  expr: Constraints[17] = Spreadsheet.interface_height / 4
  expr: Constraints[18] = Spreadsheet.interface_height / 4
  expr: Constraints[19] = Spreadsheet.interface_height / 4
  expr: Constraints[1] = Spreadsheet.screw_radius
  expr: Constraints[20] = Spreadsheet.interface_height / 4
  expr: Constraints[21] = Spreadsheet.interface_height / 4
  expr: Constraints[22] = Spreadsheet.interface_height / 4
  expr: Constraints[2] = Spreadsheet.screw_radius
  expr: Constraints[3] = Spreadsheet.screw_radius
  sketch-geometry (8):
    g0: Circle CenterX=-27.5 CenterY=5 CenterZ=0 NormalX=0 NormalY=0 NormalZ=1 AngleXU=0 Radius=1.5
    g1: Circle CenterX=-27.5 CenterY=-5 CenterZ=0 NormalX=0 NormalY=0 NormalZ=1 AngleXU=0 Radius=1.5
    g2: Circle CenterX=27.5 CenterY=5 CenterZ=0 NormalX=0 NormalY=0 NormalZ=1 AngleXU=0 Radius=1.5
    g3: Circle CenterX=27.5 CenterY=-5 CenterZ=0 NormalX=0 NormalY=0 NormalZ=1 AngleXU=0 Radius=1.5
    g4: LineSegment StartX=-32.5 StartY=10 StartZ=0 EndX=32.5 EndY=10 EndZ=0
    g5: LineSegment StartX=32.5 StartY=10 StartZ=0 EndX=32.5 EndY=-10 EndZ=0
    g6: LineSegment StartX=32.5 StartY=-10 StartZ=0 EndX=-32.5 EndY=-10 EndZ=0
    g7: LineSegment StartX=-32.5 StartY=-10 StartZ=0 EndX=-32.5 EndY=10 EndZ=0
  constraints (23):
    c: Radius(g0) = 1.5
    c: Radius(g1) = 1.5
    c: Radius(g2) = 1.5
    c: Radius(g3) = 1.5
    c: Coincident(g4,g5)
    c: Coincident(g5,g6)
    c: Coincident(g6,g7)
    c: Coincident(g7,g4)
    c: Horizontal(g4)
    c: Horizontal(g6)
    c: Vertical(g5)
    c: Vertical(g7)
    c: Symmetric(g4,g6,g-1)
    c: DistanceX(g4,g4) = 65
    c: DistanceY(g7,g7) = 20
    c: DistanceX(g4,g0) = 5
    c: DistanceX(g2,g4) = 5
    c: DistanceX(g3,g5) = 5
    c: DistanceX(g6,g1) = 5
    c: DistanceY(g0,g4) = 5
    c: DistanceY(g6,g1) = 5
    c: DistanceY(g2,g4) = 5
    c: DistanceY(g5,g3) = 5
FEATURE [PartDesign::Hole] Hole
  BaseFeature = -> Pad
  CustomThreadClearance = 0
  Depth = 113.066
  DepthType = 1
  Diameter = 3.4
  DrillForDepth = false
  DrillPoint = 1
  DrillPointAngle = 118
  HoleCutCountersinkAngle = 90
  HoleCutCustomValues = false
  HoleCutDepth = 0
  HoleCutDiameter = 6.1
  HoleCutType = 0
  ModelThread = false
  Profile = -> Sketch001
  Tapered = false
  TaperedAngle = 90
  ThreadClass = 0
  ThreadDepth = 113.066
  ThreadDepthType = 0
  ThreadDirection = 0
  ThreadFit = 0
  ThreadSize = 9
  ThreadType = 1
  Threaded = false
  UseCustomThreadClearance = false
FEATURE [Sketcher::SketchObject] Sketch002
  FullyConstrained = true
  MapMode = 5
  Placement = pos=(0,0,2) rot=(0,0,1;0rad)
  Support = -> [Hole]
  expr: Constraints[10] = Spreadsheet.handgrip_depth
  expr: Constraints[9] = Spreadsheet.handgrip_width
  sketch-geometry (4):
    g0: LineSegment StartX=-20 StartY=20 StartZ=0 EndX=20 EndY=20 EndZ=0
    g1: LineSegment StartX=20 StartY=20 StartZ=0 EndX=20 EndY=-20 EndZ=0
    g2: LineSegment StartX=20 StartY=-20 StartZ=0 EndX=-20 EndY=-20 EndZ=0
    g3: LineSegment StartX=-20 StartY=-20 StartZ=0 EndX=-20 EndY=20 EndZ=0
  constraints (11):
    c: Coincident(g0,g1)
    c: Coincident(g1,g2)
    c: Coincident(g2,g3)
    c: Coincident(g3,g0)
    c: Horizontal(g0)
    c: Horizontal(g2)
    c: Vertical(g1)
    c: Vertical(g3)
    c: Symmetric(g0,g2,g-1)
    c: DistanceX(g0,g0) = 40
    c: DistanceY(g3,g3) = 40
FEATURE [PartDesign::Pad] Pad001
  BaseFeature = -> Hole
  Direction = (0,0.267949,1)
  Length = 100
  Length2 = 10
  Profile = -> Sketch002
  ReferenceAxis = -> Sketch002 [N_Axis]
  Type = 0
  UseCustomVector = true
  expr: .Direction.y = tan(Spreadsheet.slant)
  expr: Length = Spreadsheet.handgrip_length
FEATURE [Sketcher::SketchObject] Sketch003
  ExternalGeometry = -> [Pad001]
  FullyConstrained = true
  MapMode = 5
  Placement = pos=(-20,0,0) rot=(0.57735,-0.57735,-0.57735;2.0944rad)
  Support = -> [Pad001]
  sketch-geometry (14):
    g0: Circle CenterX=20 CenterY=2 CenterZ=0 NormalX=0 NormalY=0 NormalZ=1 AngleXU=0 Radius=1
    g1: Circle CenterX=4.64102 CenterY=12 CenterZ=0 NormalX=0 NormalY=0 NormalZ=1 AngleXU=0 Radius=1
    g2: Circle CenterX=14.641 CenterY=22 CenterZ=0 NormalX=0 NormalY=0 NormalZ=1 AngleXU=0 Radius=1
    g3: BSplineCurve PolesCount=3 KnotsCount=2 Degree=2 IsPeriodic=0
    g4: GeomPoint X=20 Y=2 Z=0
    g5: GeomPoint X=14.641 Y=22 Z=0
    g6-g9: Circle x4 (B-spline internal-alignment scaffolding for g10; pole/knot coordinates omitted)
    g10: BSplineCurve PolesCount=4 KnotsCount=2 Degree=3 IsPeriodic=0
    g11: GeomPoint X=14.641 Y=22 Z=0
    g12: GeomPoint X=-6.79492 Y=102 Z=0
    g13: LineSegment StartX=-6.79492 StartY=102 StartZ=0 EndX=20 EndY=2 EndZ=0
  constraints (28):
    c: Weight(g0) = 1
    c: Equal(g0,g1)
    c: Equal(g0,g2)
    c: InternalAlignment(g0,g3)
    c: InternalAlignment(g1,g3)
    c: InternalAlignment(g2,g3)
    c: InternalAlignment(g4,g3)
    c: InternalAlignment(g5,g3)
    c: Weight(g6) = 1
    c: Coincident(g10,g3)
    c: Equal(g6,g7)
    c: Equal(g6,g8)
    c: Equal(g6,g9)
    c: InternalAlignment(g6-g9 -> g10) x4
    c: InternalAlignment(g11,g10)
    c: InternalAlignment(g12,g10)
    c: DistanceY(g-7,g3) = 20
    c: DistanceX(g1,g3) = 10
    c: DistanceY(g1,g3) = 10
    c: DistanceX(g7,g3) = 15
    c: DistanceY(g3,g7) = 3
    c: DistanceY(g8,g-6) = 3
    c: DistanceX(g8,g-6) = 10
    c: PointOnObject(g3,g-6)
    c: Coincident(g10,g-6)
    c: Coincident(g3,g-7)
    c: Coincident(g13,g10)
    c: Coincident(g13,g3)
FEATURE [PartDesign::Pocket] Pocket
  BaseFeature = -> Pad001
  Direction = (1,0,0)
  Length = 5
  Length2 = 5
  Profile = -> Sketch003
  ReferenceAxis = -> Sketch003 [N_Axis]
  Type = 1
FEATURE [PartDesign::Fillet] Fillet
  Base = -> Pocket [Edge46]
  BaseFeature = -> Pocket
  Radius = 5
  SupportTransform = false
  UseAllEdges = false
FEATURE [PartDesign::Fillet] Fillet001
  Base = -> Fillet [Edge4,Edge17]
  BaseFeature = -> Fillet
  Radius = 11
  SupportTransform = false
  UseAllEdges = false
FEATURE [PartDesign::Fillet] Fillet002
  Base = -> Fillet001 [Edge17,Edge28]
  BaseFeature = -> Fillet001
  Radius = 5
  SupportTransform = false
  UseAllEdges = false
FEATURE [PartDesign::Fillet] Fillet003
  Base = -> Fillet002 [Edge5,Edge23]
  BaseFeature = -> Fillet002
  Radius = 9
  SupportTransform = false
  UseAllEdges = false
FEATURE [App::DocumentObjectGroup] Parts
FEATURE [PartDesign::CoordinateSystem] LCS_Origin
  AttacherType = Attacher::AttachEngine3D
  MapMode = 2
  Support = -> [X_Axis001]
FEATURE [App::DocumentObjectGroup] Constraints
FEATURE [App::FeaturePython] Variables  # WARN: FeaturePython — macro-defined, semantics opaque (R4)
  Type = App::PropertyContainer
FEATURE [App::DocumentObjectGroup] Configurations
FEATURE [PartDesign::CoordinateSystem] LCS_screw
  AttacherType = Attacher::AttachEngine3D
  MapMode = 11
  Placement = pos=(-27.5,-5,0) rot=(0.707107,0.707107,0;3.14159rad)
  Support = -> [Fillet003]
FEATURE [PartDesign::Chamfer] Chamfer
  Angle = 45
  Base = -> Fillet003 [Edge6,Edge53]
  BaseFeature = -> Fillet003
  ChamferType = 1
  FlipDirection = false
  Size = 1.5
  Size2 = 5
  SupportTransform = false
  UseAllEdges = false
FEATURE [PartDesign::Body] Body  label="Körper"
  Group = -> [Sketch,Pad,Sketch001,Hole,Sketch002,Pad001,Sketch003,Pocket,Fillet,Fillet001,Fillet002,Fillet003,Chamfer]
  Origin = -> Origin
  Tip = -> Chamfer
FEATURE [App::Part] Model
  AssemblyType = Part::Link
  Group = -> [LCS_Origin,Constraints,Variables,Configurations,Body,LCS_screw]
  Origin = -> Origin001
  Type = Assembly
FEATURE [Mesh::Feature] Mesh  label="Körper (Meshed)"
---- part Parts/MLX90640.FCStd = doc fcstd_dff2929a259e ----
FCSTD DOCUMENT  (FreeCAD 0.21R33668 +26 (Git))
Label: MLX90640
License: All rights reserved
LicenseURL: http://en.wikipedia.org/wiki/All_rights_reserved
objects: App::DocumentObjectGroup×3, Sketcher::SketchObject×2, PartDesign::Pad×2, PartDesign::CoordinateSystem×2, PartDesign::Body×1, Spreadsheet::Sheet×1, App::FeaturePython×1, App::Part×1
note: 9 computed .brp shape members not serialized (recipe doc carries the construction recipe); baked Part::Feature solids carry a one-line shape summary decoded from their .brp

FEATURE [Sketcher::SketchObject] Sketch
  FullyConstrained = true
  MapMode = 5
  Support = -> [XY_Plane]
  expr: Constraints[12] = <<Spreadsheet>>.holes_Vdist
  expr: Constraints[13] = <<Spreadsheet>>.holes_Hdist
  expr: Constraints[14] = <<Spreadsheet>>.holes_rad
  expr: Constraints[15] = <<Spreadsheet>>.holes_rad
  expr: Constraints[16] = <<Spreadsheet>>.holes_rad
  expr: Constraints[17] = <<Spreadsheet>>.holes_rad
  expr: Constraints[7] = <<Spreadsheet>>.board_width
  expr: Constraints[8] = <<Spreadsheet>>.board_height
  sketch-geometry (8):
    g0: LineSegment StartX=-12.7 StartY=8.89 StartZ=0 EndX=12.7 EndY=8.89 EndZ=0
    g1: LineSegment StartX=12.7 StartY=8.89 StartZ=0 EndX=12.7 EndY=-8.89 EndZ=0
    g2: LineSegment StartX=12.7 StartY=-8.89 StartZ=0 EndX=-12.7 EndY=-8.89 EndZ=0
    g3: LineSegment StartX=-12.7 StartY=-8.89 StartZ=0 EndX=-12.7 EndY=8.89 EndZ=0
    g4: Circle CenterX=-10.16 CenterY=6.35 CenterZ=0 NormalX=0 NormalY=0 NormalZ=1 AngleXU=0 Radius=1.27
    g5: Circle CenterX=10.16 CenterY=6.35 CenterZ=0 NormalX=0 NormalY=0 NormalZ=1 AngleXU=0 Radius=1.27
    g6: Circle CenterX=10.16 CenterY=-6.35 CenterZ=0 NormalX=0 NormalY=0 NormalZ=1 AngleXU=0 Radius=1.27
    g7: Circle CenterX=-10.16 CenterY=-6.35 CenterZ=0 NormalX=0 NormalY=0 NormalZ=1 AngleXU=0 Radius=1.27
  constraints (18):
    c: Coincident(g0,g1)
    c: Coincident(g1,g2)
    c: Coincident(g2,g3)
    c: Coincident(g3,g0)
    c: Symmetric(g0,g2,g-1)
    c: Symmetric(g0,g0,g-2)
    c: Symmetric(g0,g1,g-1)
    c: DistanceX(g0,g0) = 25.4
    c: DistanceY(g3,g3) = 17.78
    c: Symmetric(g4,g5,g-2)
    c: Symmetric(g4,g7,g-1)
    c: Symmetric(g4,g6,g-1)
    c: DistanceY(g7,g4) = 12.7
    c: DistanceX(g4,g5) = 20.32
    c: Radius(g4) = 1.27
    c: Radius(g5) = 1.27
    c: Radius(g7) = 1.27
    c: Radius(g6) = 1.27
FEATURE [PartDesign::Pad] Pad
  Direction = (0,0,1)
  Length = 5
  Length2 = 10
  Profile = -> Sketch
  ReferenceAxis = -> Sketch [N_Axis]
  Reversed = true
  Type = 0
  expr: Length = 5
FEATURE [Sketcher::SketchObject] Sketch001
  FullyConstrained = true
  MapMode = 5
  Support = -> [XY_Plane]
  expr: Constraints[1] = <<Spreadsheet>>.cam_rad
  sketch-geometry (1):
    g0: Circle CenterX=0 CenterY=0 CenterZ=0 NormalX=0 NormalY=0 NormalZ=1 AngleXU=0 Radius=4.65
  constraints (2):
    c: Coincident(g0,g-1)
    c: Radius(g0) = 4.65
FEATURE [PartDesign::Pad] Pad001
  BaseFeature = -> Pad
  Direction = (0,0,1)
  Length = 11.25
  Length2 = 10
  Profile = -> Sketch001
  ReferenceAxis = -> Sketch001 [N_Axis]
  Type = 0
  expr: Length = <<Spreadsheet>>.cam_height
FEATURE [PartDesign::Body] Body
  Group = -> [Sketch,Pad,Sketch001,Pad001]
  Origin = -> Origin
  Tip = -> Pad001
FEATURE [Spreadsheet::Sheet] Spreadsheet
  cells = B2='MLX; B3='board_factor; C3(board_factor)=25.4; B4='board_width; C4(board_width)==board_factor * 1 mm; B5='board_height; C5(board_height)==board_factor * 0.7 mm; B6='holes_rad; C6(holes_rad)==board_factor * 0.1 mm / 2; B7='holes_Hdist; C7(holes_Hdist)==board_factor * 0.8 mm; B8='holes_Vdist; C8(holes_Vdist)==board_factor * 0.5 mm; B9='cam_rad; C9(cam_rad)==9.3 mm / 2; B10='cam_height; C10(cam_height)==11.25 mm
FEATURE [App::DocumentObjectGroup] Parts
FEATURE [PartDesign::CoordinateSystem] LCS_Origin
  AttacherType = Attacher::AttachEngine3D
  MapMode = 2
  Support = -> [X_Axis001]
FEATURE [App::DocumentObjectGroup] Constraints
FEATURE [App::FeaturePython] Variables  # WARN: FeaturePython — macro-defined, semantics opaque (R4)
  Type = App::PropertyContainer
FEATURE [App::DocumentObjectGroup] Configurations
FEATURE [PartDesign::CoordinateSystem] LCS_mlx
  AttacherType = Attacher::AttachEngine3D
  MapMode = 11
  Placement = pos=(-10.16,6.35,-5) rot=(0,0,1;1.5708rad)
  Support = -> [Pad001]
FEATURE [App::Part] Model
  AssemblyType = Part::Link
  Group = -> [LCS_Origin,Constraints,Variables,Configurations,Body,LCS_mlx]
  Origin = -> Origin001
  Type = Assembly
---- part Parts/Raspberrypi4B.FCStd = doc fcstd_3ed2aa2c7b7e ----
FCSTD DOCUMENT  (FreeCAD 0.21R33668 +26 (Git))
Label: Raspberrypi4B
License: All rights reserved
LicenseURL: http://en.wikipedia.org/wiki/All_rights_reserved
objects: Sketcher::SketchObject×8, PartDesign::Pad×7, App::DocumentObjectGroup×3, PartDesign::CoordinateSystem×3, Spreadsheet::Sheet×1, PartDesign::Pocket×1, PartDesign::Body×1, App::FeaturePython×1, App::Part×1
note: 28 computed .brp shape members not serialized (recipe doc carries the construction recipe); baked Part::Feature solids carry a one-line shape summary decoded from their .brp

FEATURE [Sketcher::SketchObject] Sketch
  FullyConstrained = true
  MapMode = 5
  Support = -> [XY_Plane]
  expr: Constraints[12] = <<Spreadsheet>>.holes_distV
  expr: Constraints[13] = <<Spreadsheet>>.holes_distV
  expr: Constraints[14] = <<Spreadsheet>>.holes_offset_x
  expr: Constraints[15] = Spreadsheet.holes_radius
  expr: Constraints[16] = Spreadsheet.holes_radius
  expr: Constraints[17] = Spreadsheet.holes_radius
  expr: Constraints[18] = Spreadsheet.holes_radius
  expr: Constraints[7] = Spreadsheet.width
  expr: Constraints[8] = Spreadsheet.height
  expr: Constraints[9] = <<Spreadsheet>>.holes_distH
  sketch-geometry (8):
    g0: LineSegment StartX=-42.5 StartY=28 StartZ=0 EndX=42.5 EndY=28 EndZ=0
    g1: LineSegment StartX=42.5 StartY=28 StartZ=0 EndX=42.5 EndY=-28 EndZ=0
    g2: LineSegment StartX=42.5 StartY=-28 StartZ=0 EndX=-42.5 EndY=-28 EndZ=0
    g3: LineSegment StartX=-42.5 StartY=-28 StartZ=0 EndX=-42.5 EndY=28 EndZ=0
    g4: Circle CenterX=-39 CenterY=24.5 CenterZ=0 NormalX=0 NormalY=0 NormalZ=1 AngleXU=0 Radius=1.35
    g5: Circle CenterX=19 CenterY=24.5 CenterZ=0 NormalX=0 NormalY=0 NormalZ=1 AngleXU=0 Radius=1.35
    g6: Circle CenterX=-39 CenterY=-24.5 CenterZ=0 NormalX=0 NormalY=0 NormalZ=1 AngleXU=0 Radius=1.35
    g7: Circle CenterX=19 CenterY=-24.5 CenterZ=0 NormalX=0 NormalY=0 NormalZ=1 AngleXU=0 Radius=1.35
  constraints (19):
    c: Coincident(g0,g1)
    c: Coincident(g1,g2)
    c: Coincident(g2,g3)
    c: Coincident(g3,g0)
    c: Symmetric(g0,g0,g-2)
    c: Symmetric(g2,g0,g-1)
    c: Symmetric(g0,g1,g-1)
    c: DistanceX(g0,g0) = 85
    c: DistanceY(g1,g1) = 56
    c: DistanceX(g4,g5) = 58
    c: Symmetric(g4,g6,g-1)
    c: Symmetric(g5,g7,g-1)
    c: DistanceY(g6,g4) = 49
    c: DistanceY(g7,g5) = 49
    c: DistanceX(g0,g4) = 3.5
    c: Radius(g4) = 1.35
    c: Radius(g5) = 1.35
    c: Radius(g7) = 1.35
    c: Radius(g6) = 1.35
FEATURE [PartDesign::Pad] Pad
  Direction = (0,0,1)
  Length = 4
  Length2 = 10
  Profile = -> Sketch
  ReferenceAxis = -> Sketch [N_Axis]
  Reversed = true
  Type = 0
  expr: Length = Spreadsheet.thickness
FEATURE [Spreadsheet::Sheet] Spreadsheet
  cells = B2='width; C2(width)==85 mm; E2='holes_radius; F2(holes_radius)==1.35 mm; H2='usb_lower_offset; I2(usb_lower_offset)==47 mm; B3='height; C3(height)==56 mm; E3='holes_distH; F3(holes_distH)==58 mm; H3='usb_middle_offset; I3(usb_middle_offset)==29 mm; B4='thickness; C4(thickness)==4 mm; E4='holes_distV; F4(holes_distV)==49 mm; H4='ethernet_offset; I4(ethernet_offset)==10.25 mm; E5='holes_offset_x; F5(holes_offset_x)==3.5 mm; H5='usbc_offset; I5(usbc_offset)==7.7 mm + 3.5 mm; B6='connector_width; C6(connector_width)==50 mm; H6='hdmi_left_offset; I6(hdmi_left_offset)==14.8 mm; B7='connector_height; C7(connector_height)==5 mm; H7='hdmi_right_offset; I7(hdmi_right_offset)=13.5; B8='connector_depth; C8(connector_depth)==8.5 mm; H8='round_power_offset; I8(round_power_offset)==14.5 mm; B9='connector_base_depth; C9(connector_base_depth)==2.5 mm; E11='usb_width; F11(usb_width)==12 mm; H11='ethernet_width; I11(ethernet_width)==16 mm; E12='usb_depth; F12(usb_depth)==17.5 mm; H12='ethernet_depth; I12(ethernet_depth)==21.1 mm; E13='usb_height; F13(usb_height)==16 mm; H13='ethernet_height; I13(ethernet_height)==13.5 mm; E15='usbc_width; F15(usbc_width)==9.2 mm; H15='hdmi_width; I15(hdmi_width)==7 mm; E16='usbc_depth; F16(usbc_depth)==10.5 mm; H16='hdmi_depth; I16(hdmi_depth)==8 mm; E17='usbc_height; F17(usbc_height)==3.2 mm; H17='hdmi_height; I17(hdmi_height)==3 mm; E19='rpower_width; F19(rpower_width)==7 mm; H19='right_protrude; I19(right_protrude)==3.5 mm; E20='rpower_depth; F20(rpower_depth)==12 mm; H20='lower_protrude; I20(lower_protrude)==1 mm; E21='rpower_height; F21(rpower_height)==6 mm
FEATURE [Sketcher::SketchObject] Sketch001
  ExternalGeometry = -> [Pad]
  FullyConstrained = true
  MapMode = 5
  Support = -> [Pad]
  expr: Constraints[10] = <<Spreadsheet>>.connector_height
  expr: Constraints[9] = <<Spreadsheet>>.connector_width
  sketch-geometry (5):
    g0: LineSegment StartX=-35 StartY=27 StartZ=0 EndX=15 EndY=27 EndZ=0
    g1: LineSegment StartX=15 StartY=27 StartZ=0 EndX=15 EndY=22 EndZ=0
    g2: LineSegment StartX=15 StartY=22 StartZ=0 EndX=-35 EndY=22 EndZ=0
    g3: LineSegment StartX=-35 StartY=22 StartZ=0 EndX=-35 EndY=27 EndZ=0
    g4: GeomPoint X=-10 Y=24.5 Z=0
  constraints (11):
    c: Coincident(g0,g1)
    c: Coincident(g1,g2)
    c: Coincident(g2,g3)
    c: Coincident(g3,g0)
    c: Horizontal(g0)
    c: Vertical(g1)
    c: Symmetric(g-7,g-8,g4)
    c: Symmetric(g0,g1,g4)
    c: Symmetric(g2,g0,g4)
    c: DistanceX(g0,g0) = 50
    c: DistanceY(g3,g3) = 5
FEATURE [PartDesign::Pad] Pad001
  BaseFeature = -> Pad
  Direction = (0,0,1)
  Length = 8.5
  Length2 = 10
  Profile = -> Sketch001
  ReferenceAxis = -> Sketch001 [N_Axis]
  Type = 0
  expr: Length = <<Spreadsheet>>.connector_depth
FEATURE [Sketcher::SketchObject] Sketch002
  ExternalGeometry = -> [Pad001]
  FullyConstrained = true
  MapMode = 5
  Placement = pos=(0,0,8.5) rot=(0,0,1;0rad)
  Support = -> [Pad001]
  sketch-geometry (8):
    g0: LineSegment StartX=-35 StartY=27 StartZ=0 EndX=15 EndY=27 EndZ=0
    g1: LineSegment StartX=15 StartY=27 StartZ=0 EndX=15 EndY=22 EndZ=0
    g2: LineSegment StartX=15 StartY=22 StartZ=0 EndX=-35 EndY=22 EndZ=0
    g3: LineSegment StartX=-35 StartY=22 StartZ=0 EndX=-35 EndY=27 EndZ=0
    g4: LineSegment StartX=-34 StartY=26 StartZ=0 EndX=14 EndY=26 EndZ=0
    g5: LineSegment StartX=14 StartY=26 StartZ=0 EndX=14 EndY=23 EndZ=0
    g6: LineSegment StartX=14 StartY=23 StartZ=0 EndX=-34 EndY=23 EndZ=0
    g7: LineSegment StartX=-34 StartY=23 StartZ=0 EndX=-34 EndY=26 EndZ=0
  constraints (22):
    c: Coincident(g0,g1)
    c: Coincident(g1,g2)
    c: Coincident(g2,g3)
    c: Coincident(g3,g0)
    c: Horizontal(g0)
    c: Horizontal(g2)
    c: Vertical(g1)
    c: Vertical(g3)
    c: Coincident(g0,g-4)
    c: Coincident(g1,g-6)
    c: Coincident(g4,g5)
    c: Coincident(g5,g6)
    c: Coincident(g6,g7)
    c: Coincident(g7,g4)
    c: Horizontal(g4)
    c: Horizontal(g6)
    c: Vertical(g5)
    c: Vertical(g7)
    c: DistanceX(g0,g4) = 1
    c: DistanceY(g4,g0) = 1
    c: DistanceY(g2,g6) = 1
    c: DistanceX(g4,g0) = 1
FEATURE [PartDesign::Pocket] Pocket  label="Connector"
  BaseFeature = -> Pad001
  Direction = (0,0,-1)
  Length = 6
  Length2 = 5
  Profile = -> Sketch002
  ReferenceAxis = -> Sketch002 [N_Axis]
  Type = 0
  expr: Length = <<Spreadsheet>>.connector_depth - <<Spreadsheet>>.connector_base_depth
FEATURE [Sketcher::SketchObject] Sketch003
  ExternalGeometry = -> [Pocket]
  FullyConstrained = true
  MapMode = 5
  Support = -> [Pocket]
  expr: Constraints[18] = <<Spreadsheet>>.usb_lower_offset
  expr: Constraints[19] = <<Spreadsheet>>.usb_middle_offset
  expr: Constraints[20] = <<Spreadsheet>>.usb_width
  expr: Constraints[21] = <<Spreadsheet>>.usb_width
  expr: Constraints[22] = <<Spreadsheet>>.usb_width / 2
  expr: Constraints[23] = <<Spreadsheet>>.usb_width / 2
  expr: Constraints[24] = <<Spreadsheet>>.usb_depth
  expr: Constraints[25] = <<Spreadsheet>>.usb_depth
  expr: Constraints[26] = <<Spreadsheet>>.right_protrude
  expr: Constraints[27] = <<Spreadsheet>>.right_protrude
  sketch-geometry (10):
    g0: LineSegment StartX=28.5 StartY=25 StartZ=0 EndX=46 EndY=25 EndZ=0
    g1: LineSegment StartX=46 StartY=25 StartZ=0 EndX=46 EndY=13 EndZ=0
    g2: LineSegment StartX=46 StartY=13 StartZ=0 EndX=28.5 EndY=13 EndZ=0
    g3: LineSegment StartX=28.5 StartY=13 StartZ=0 EndX=28.5 EndY=25 EndZ=0
    g4: LineSegment StartX=28.5 StartY=7 StartZ=0 EndX=46 EndY=7 EndZ=0
    g5: LineSegment StartX=46 StartY=7 StartZ=0 EndX=46 EndY=-5 EndZ=0
    g6: LineSegment StartX=46 StartY=-5 StartZ=0 EndX=28.5 EndY=-5 EndZ=0
    g7: LineSegment StartX=28.5 StartY=-5 StartZ=0 EndX=28.5 EndY=7 EndZ=0
    g8: GeomPoint X=42.5 Y=19 Z=0
    g9: GeomPoint X=42.5 Y=1 Z=0
  constraints (28):
    c: Coincident(g0,g1)
    c: Coincident(g1,g2)
    c: Coincident(g2,g3)
    c: Coincident(g3,g0)
    c: Horizontal(g0)
    c: Horizontal(g2)
    c: Vertical(g1)
    c: Vertical(g3)
    c: Coincident(g4,g5)
    c: Coincident(g5,g6)
    c: Coincident(g6,g7)
    c: Coincident(g7,g4)
    c: Horizontal(g4)
    c: Horizontal(g6)
    c: Vertical(g5)
    c: Vertical(g7)
    c: PointOnObject(g8,g-4)
    c: PointOnObject(g9,g-4)
    c: DistanceY(g-4,g8) = 47
    c: DistanceY(g-4,g9) = 29
    c: DistanceY(g3,g3) = 12
    c: DistanceY(g7,g7) = 12
    c: DistanceY(g8,g0) = 6
    c: DistanceY(g9,g4) = 6
    c: DistanceX(g4,g4) = 17.5
    c: DistanceX(g0,g0) = 17.5
    c: DistanceX(g-4,g1) = 3.5
    c: DistanceX(g-4,g5) = 3.5
FEATURE [PartDesign::Pad] Pad002  label="USB_A"
  BaseFeature = -> Pocket
  Direction = (0,0,1)
  Length = 16
  Length2 = 10
  Profile = -> Sketch003
  ReferenceAxis = -> Sketch003 [N_Axis]
  Type = 0
  expr: Length = <<Spreadsheet>>.usb_height
FEATURE [Sketcher::SketchObject] Sketch004
  ExternalGeometry = -> [Pad002]
  FullyConstrained = true
  MapMode = 5
  Support = -> [Pad002]
  expr: Constraints[10] = <<Spreadsheet>>.ethernet_width
  expr: Constraints[11] = <<Spreadsheet>>.ethernet_depth
  expr: Constraints[12] = <<Spreadsheet>>.ethernet_width / 2
  expr: Constraints[13] = <<Spreadsheet>>.right_protrude
  expr: Constraints[9] = <<Spreadsheet>>.ethernet_offset
  sketch-geometry (5):
    g0: LineSegment StartX=24.9 StartY=-9.75 StartZ=0 EndX=46 EndY=-9.75 EndZ=0
    g1: LineSegment StartX=46 StartY=-9.75 StartZ=0 EndX=46 EndY=-25.75 EndZ=0
    g2: LineSegment StartX=46 StartY=-25.75 StartZ=0 EndX=24.9 EndY=-25.75 EndZ=0
    g3: LineSegment StartX=24.9 StartY=-25.75 StartZ=0 EndX=24.9 EndY=-9.75 EndZ=0
    g4: GeomPoint X=42.5 Y=-17.75 Z=0
  constraints (14):
    c: Coincident(g0,g1)
    c: Coincident(g1,g2)
    c: Coincident(g2,g3)
    c: Coincident(g3,g0)
    c: Horizontal(g0)
    c: Horizontal(g2)
    c: Vertical(g1)
    c: Vertical(g3)
    c: PointOnObject(g4,g-4)
    c: DistanceY(g-3,g4) = 10.25
    c: DistanceY(g3,g3) = 16
    c: DistanceX(g0,g0) = 21.1
    c: DistanceY(g4,g0) = 8
    c: DistanceX(g4,g1) = 3.5
FEATURE [PartDesign::Pad] Pad003  label="Ethernet"
  BaseFeature = -> Pad002
  Direction = (0,0,1)
  Length = 13.5
  Length2 = 10
  Profile = -> Sketch004
  ReferenceAxis = -> Sketch004 [N_Axis]
  Type = 0
  expr: Length = <<Spreadsheet>>.ethernet_height
FEATURE [Sketcher::SketchObject] Sketch005
  ExternalGeometry = -> [Pad003]
  FullyConstrained = true
  MapMode = 5
  Support = -> [Pad003]
  expr: Constraints[10] = <<Spreadsheet>>.usbc_width
  expr: Constraints[11] = <<Spreadsheet>>.usbc_depth
  expr: Constraints[12] = <<Spreadsheet>>.usbc_width / 2
  expr: Constraints[13] = <<Spreadsheet>>.lower_protrude
  expr: Constraints[9] = <<Spreadsheet>>.usbc_offset
  sketch-geometry (5):
    g0: LineSegment StartX=-35.9 StartY=-18.5 StartZ=0 EndX=-26.7 EndY=-18.5 EndZ=0
    g1: LineSegment StartX=-26.7 StartY=-18.5 StartZ=0 EndX=-26.7 EndY=-29 EndZ=0
    g2: LineSegment StartX=-26.7 StartY=-29 StartZ=0 EndX=-35.9 EndY=-29 EndZ=0
    g3: LineSegment StartX=-35.9 StartY=-29 StartZ=0 EndX=-35.9 EndY=-18.5 EndZ=0
    g4: GeomPoint X=-31.3 Y=-28 Z=0
  constraints (14):
    c: Coincident(g0,g1)
    c: Coincident(g1,g2)
    c: Coincident(g2,g3)
    c: Coincident(g3,g0)
    c: Horizontal(g0)
    c: Horizontal(g2)
    c: Vertical(g1)
    c: Vertical(g3)
    c: PointOnObject(g4,g-4)
    c: DistanceX(g-4,g4) = 11.2
    c: DistanceX(g0,g0) = 9.2
    c: DistanceY(g1,g1) = 10.5
    c: DistanceX(g4,g0) = 4.6
    c: DistanceY(g2,g4) = 1
FEATURE [PartDesign::Pad] Pad004  label="USB_C"
  BaseFeature = -> Pad003
  Direction = (0,0,1)
  Length = 3.2
  Length2 = 10
  Profile = -> Sketch005
  ReferenceAxis = -> Sketch005 [N_Axis]
  Type = 0
  expr: Length = <<Spreadsheet>>.usbc_height
FEATURE [Sketcher::SketchObject] Sketch006
  ExternalGeometry = -> [Pad004]
  FullyConstrained = true
  MapMode = 5
  Support = -> [Pad004]
  expr: Constraints[19] = <<Spreadsheet>>.hdmi_left_offset
  expr: Constraints[20] = <<Spreadsheet>>.hdmi_right_offset
  expr: Constraints[21] = <<Spreadsheet>>.hdmi_width
  expr: Constraints[22] = <<Spreadsheet>>.hdmi_width
  expr: Constraints[23] = <<Spreadsheet>>.hdmi_depth
  expr: Constraints[24] = <<Spreadsheet>>.hdmi_depth
  expr: Constraints[25] = <<Spreadsheet>>.hdmi_width / 2
  expr: Constraints[26] = <<Spreadsheet>>.hdmi_width / 2
  expr: Constraints[27] = <<Spreadsheet>>.lower_protrude
  expr: Constraints[28] = <<Spreadsheet>>.lower_protrude
  sketch-geometry (11):
    g0: LineSegment StartX=-20 StartY=-21 StartZ=0 EndX=-13 EndY=-21 EndZ=0
    g1: LineSegment StartX=-13 StartY=-21 StartZ=0 EndX=-13 EndY=-29 EndZ=0
    g2: LineSegment StartX=-13 StartY=-29 StartZ=0 EndX=-20 EndY=-29 EndZ=0
    g3: LineSegment StartX=-20 StartY=-29 StartZ=0 EndX=-20 EndY=-21 EndZ=0
    g4: LineSegment StartX=-6.5 StartY=-21 StartZ=0 EndX=0.5 EndY=-21 EndZ=0
    g5: LineSegment StartX=0.5 StartY=-21 StartZ=0 EndX=0.5 EndY=-29 EndZ=0
    g6: LineSegment StartX=0.5 StartY=-29 StartZ=0 EndX=-6.5 EndY=-29 EndZ=0
    g7: LineSegment StartX=-6.5 StartY=-29 StartZ=0 EndX=-6.5 EndY=-21 EndZ=0
    g8: GeomPoint X=-31.3 Y=-29 Z=0
    g9: GeomPoint X=-16.5 Y=-28 Z=0
    g10: GeomPoint X=-3 Y=-28 Z=0
  constraints (29):
    c: Coincident(g0,g1)
    c: Coincident(g1,g2)
    c: Coincident(g2,g3)
    c: Coincident(g3,g0)
    c: Horizontal(g0)
    c: Horizontal(g2)
    c: Vertical(g1)
    c: Vertical(g3)
    c: Coincident(g4,g5)
    c: Coincident(g5,g6)
    c: Coincident(g6,g7)
    c: Coincident(g7,g4)
    c: Horizontal(g4)
    c: Horizontal(g6)
    c: Vertical(g5)
    c: Vertical(g7)
    c: PointOnObject(g9,g-3)
    c: PointOnObject(g10,g-3)
    c: Symmetric(g-6,g-5,g8)
    c: DistanceX(g8,g9) = 14.8
    c: DistanceX(g9,g10) = 13.5
    c: DistanceX(g0,g0) = 7
    c: DistanceX(g4,g4) = 7
    c: DistanceY(g3,g3) = 8
    c: DistanceY(g7,g7) = 8
    c: DistanceX(g2,g9) = 3.5
    c: DistanceX(g6,g10) = 3.5
    c: DistanceY(g1,g9) = 1
    c: DistanceY(g5,g10) = 1
FEATURE [PartDesign::Pad] Pad005  label="HDMI_Mini"
  BaseFeature = -> Pad004
  Direction = (0,0,1)
  Length = 3
  Length2 = 10
  Profile = -> Sketch006
  ReferenceAxis = -> Sketch006 [N_Axis]
  Type = 0
  expr: Length = <<Spreadsheet>>.hdmi_height
FEATURE [Sketcher::SketchObject] Sketch007
  ExternalGeometry = -> [Pad005]
  FullyConstrained = true
  MapMode = 5
  Support = -> [Pad005]
  expr: Constraints[10] = <<Spreadsheet>>.round_power_offset
  expr: Constraints[11] = <<Spreadsheet>>.rpower_width
  expr: Constraints[12] = <<Spreadsheet>>.rpower_depth
  expr: Constraints[13] = <<Spreadsheet>>.rpower_width / 2
  expr: Constraints[14] = <<Spreadsheet>>.lower_protrude
  sketch-geometry (6):
    g0: LineSegment StartX=8 StartY=-17 StartZ=0 EndX=15 EndY=-17 EndZ=0
    g1: LineSegment StartX=15 StartY=-17 StartZ=0 EndX=15 EndY=-29 EndZ=0
    g2: LineSegment StartX=15 StartY=-29 StartZ=0 EndX=8 EndY=-29 EndZ=0
    g3: LineSegment StartX=8 StartY=-29 StartZ=0 EndX=8 EndY=-17 EndZ=0
    g4: GeomPoint X=-3 Y=-29 Z=0
    g5: GeomPoint X=11.5 Y=-28 Z=0
  constraints (15):
    c: Coincident(g0,g1)
    c: Coincident(g1,g2)
    c: Coincident(g2,g3)
    c: Coincident(g3,g0)
    c: Horizontal(g0)
    c: Horizontal(g2)
    c: Vertical(g1)
    c: Vertical(g3)
    c: PointOnObject(g5,g-3)
    c: Symmetric(g-4,g-5,g4)
    c: DistanceX(g4,g5) = 14.5
    c: DistanceX(g0,g0) = 7
    c: DistanceY(g3,g3) = 12
    c: DistanceX(g2,g5) = 3.5
    c: DistanceY(g2,g5) = 1
FEATURE [PartDesign::Pad] Pad006  label="Round_Power"
  BaseFeature = -> Pad005
  Direction = (0,0,1)
  Length = 6
  Length2 = 10
  Profile = -> Sketch007
  ReferenceAxis = -> Sketch007 [N_Axis]
  Type = 0
  expr: Length = <<Spreadsheet>>.rpower_height
FEATURE [PartDesign::Body] Body
  Group = -> [Sketch,Pad,Sketch001,Pad001,Sketch002,Pocket,Sketch003,Pad002,Sketch004,Pad003,Sketch005,Pad004,Sketch006,Pad005,Sketch007,Pad006]
  Origin = -> Origin
  Tip = -> Pad006
FEATURE [App::DocumentObjectGroup] Parts
FEATURE [PartDesign::CoordinateSystem] LCS_Origin
  AttacherType = Attacher::AttachEngine3D
  MapMode = 2
  Support = -> [X_Axis001]
FEATURE [App::DocumentObjectGroup] Constraints
FEATURE [App::FeaturePython] Variables  # WARN: FeaturePython — macro-defined, semantics opaque (R4)
  Type = App::PropertyContainer
FEATURE [App::DocumentObjectGroup] Configurations
FEATURE [PartDesign::CoordinateSystem] LCS_Connector
  AttacherType = Attacher::AttachEngine3D
  MapMode = 1
  Placement = pos=(-35,27,2.5) rot=(0,0,1;0rad)
  Support = -> [Pad006]
FEATURE [PartDesign::CoordinateSystem] LCS_Screw
  AttacherType = Attacher::AttachEngine3D
  MapMode = 11
  Placement = pos=(-39,24.5,-4) rot=(0,0,1;1.5708rad)
  Support = -> [Pad006]
FEATURE [App::Part] Model
  AssemblyType = Part::Link
  Group = -> [LCS_Origin,Constraints,Variables,Configurations,Body,LCS_Connector,LCS_Screw]
  Origin = -> Origin001
  Type = Assembly
---- part Parts/Support_Display_new.FCStd = doc fcstd_21d0ef0dd403 ----
FCSTD DOCUMENT  (FreeCAD 0.21R33668 +26 (Git))
Label: Support_Display_new
License: All rights reserved
LicenseURL: https://en.wikipedia.org/wiki/All_rights_reserved
objects: Sketcher::SketchObject×7, PartDesign::Pocket×4, App::DocumentObjectGroup×3, PartDesign::CoordinateSystem×3, PartDesign::Pad×2, Spreadsheet::Sheet×1, PartDesign::Hole×1, App::FeaturePython×1, PartDesign::Chamfer×1, PartDesign::Body×1, App::Part×1, Mesh::Feature×1
note: 27 computed .brp shape members not serialized (recipe doc carries the construction recipe); baked Part::Feature solids carry a one-line shape summary decoded from their .brp
EXTERNAL_REF file=Display_Berrybase.FCStd obj=Spreadsheet

FEATURE [Spreadsheet::Sheet] Spreadsheet
  cells = B2='Carrier; E2='Display; B3='walls_thickness; C3(walls_thickness)==2 mm; E3='display_width; F3(display_width)==<<Display_Berrybase>>#<<Spreadsheet>>.width; H3='nut_width; I3(nut_width)==5.5 mm; B4='length; C4(length)==main_case_width - walls_thickness * 2; E4='display_height; F4(display_height)==<<Display_Berrybase>>#<<Spreadsheet>>.height; H4='nut_depth; I4(nut_depth)==3 mm; B5='height; C5(height)==10 mm; E5='display_depth; F5(display_depth)==<<Display_Berrybase>>#<<Spreadsheet>>.thickness; B6='width; C6(width)==60 mm; E6='connector_width; F6(connector_width)==<<Display_Berrybase>>#<<Spreadsheet>>.connector_width; H6='main_case_width; I6(main_case_width)==95 mm; B7='beams_width; C7(beams_width)==10 mm; E7='connector_height; F7(connector_height)==<<Display_Berrybase>>#<<Spreadsheet>>.connector_height; B8='beams_seperation; C8(beams_seperation)==15 mm; E8='connector_length; F8(connector_length)==<<Display_Berrybase>>#<<Spreadsheet>>.connector_length; B9='cross_thickness; C9(cross_thickness)==2 mm; E9='connector_offset_x; F9(connector_offset_x)==<<Display_Berrybase>>#<<Spreadsheet>>.connector_offset_x; B10='screw_radius; C10(screw_radius)==1.5 mm; E10='connector_offset_y; F10(connector_offset_y)==<<Display_Berrybase>>#<<Spreadsheet>>.connector_offset_y; B12='hole_clearance; C12(hole_clearance)==1 mm
FEATURE [Sketcher::SketchObject] Sketch
  FullyConstrained = true
  MapMode = 5
  Support = -> [XY_Plane]
  expr: Constraints[10] = Spreadsheet.width
  expr: Constraints[9] = Spreadsheet.length
  sketch-geometry (4):
    g0: LineSegment StartX=-45.5 StartY=30 StartZ=0 EndX=45.5 EndY=30 EndZ=0
    g1: LineSegment StartX=45.5 StartY=30 StartZ=0 EndX=45.5 EndY=-30 EndZ=0
    g2: LineSegment StartX=45.5 StartY=-30 StartZ=0 EndX=-45.5 EndY=-30 EndZ=0
    g3: LineSegment StartX=-45.5 StartY=-30 StartZ=0 EndX=-45.5 EndY=30 EndZ=0
  constraints (11):
    c: Coincident(g0,g1)
    c: Coincident(g1,g2)
    c: Coincident(g2,g3)
    c: Coincident(g3,g0)
    c: Horizontal(g0)
    c: Horizontal(g2)
    c: Vertical(g1)
    c: Vertical(g3)
    c: Symmetric(g0,g1,g-1)
    c: DistanceX(g0,g0) = 91
    c: DistanceY(g3,g3) = 60
FEATURE [PartDesign::Pad] Pad
  Direction = (0,0,1)
  Length = 2
  Length2 = 10
  Profile = -> Sketch
  ReferenceAxis = -> Sketch [N_Axis]
  Type = 0
  expr: Length = Spreadsheet.walls_thickness
FEATURE [Sketcher::SketchObject] Sketch001
  ExternalGeometry = -> [Pad]
  FullyConstrained = true
  MapMode = 5
  Placement = pos=(0,0,2) rot=(0,0,1;0rad)
  Support = -> [Pad]
  expr: Constraints[10] = Spreadsheet.beams_seperation + Spreadsheet.beams_width * 2
  sketch-geometry (4):
    g0: LineSegment StartX=-45.5 StartY=17.5 StartZ=0 EndX=45.5 EndY=17.5 EndZ=0
    g1: LineSegment StartX=45.5 StartY=17.5 StartZ=0 EndX=45.5 EndY=-17.5 EndZ=0
    g2: LineSegment StartX=45.5 StartY=-17.5 StartZ=0 EndX=-45.5 EndY=-17.5 EndZ=0
    g3: LineSegment StartX=-45.5 StartY=-17.5 StartZ=0 EndX=-45.5 EndY=17.5 EndZ=0
  constraints (11):
    c: Coincident(g0,g1)
    c: Coincident(g1,g2)
    c: Coincident(g2,g3)
    c: Coincident(g3,g0)
    c: Horizontal(g0)
    c: Horizontal(g2)
    c: Vertical(g1)
    c: PointOnObject(g0,g-4)
    c: PointOnObject(g1,g-6)
    c: Symmetric(g0,g2,g-1)
    c: DistanceY(g3,g3) = 35
FEATURE [PartDesign::Pad] Pad001
  BaseFeature = -> Pad
  Direction = (0,0,1)
  Length = 8
  Length2 = 10
  Profile = -> Sketch001
  ReferenceAxis = -> Sketch001 [N_Axis]
  Type = 0
  expr: Length = Spreadsheet.height - Spreadsheet.walls_thickness
FEATURE [Sketcher::SketchObject] Sketch002
  ExternalGeometry = -> [Pad001]
  FullyConstrained = true
  MapMode = 5
  Placement = pos=(0,0,10) rot=(0,0,1;0rad)
  Support = -> [Pad001]
  expr: Constraints[33] = Spreadsheet.beams_width
  expr: Constraints[34] = Spreadsheet.walls_thickness
  expr: Constraints[52] = Spreadsheet.cross_thickness
  sketch-geometry (21):
    g0: LineSegment StartX=-43.5 StartY=7.5 StartZ=0 EndX=43.5 EndY=7.5 EndZ=0
    g1: LineSegment StartX=43.5 StartY=7.5 StartZ=0 EndX=0 EndY=1.01106 EndZ=0
    g2: LineSegment StartX=0 StartY=1.01106 StartZ=0 EndX=-43.5 EndY=7.5 EndZ=0
    g3: LineSegment StartX=-43.5 StartY=5.47787 StartZ=0 EndX=-6.77789 EndY=0 EndZ=0
    g4: LineSegment StartX=-6.77789 StartY=0 StartZ=0 EndX=-43.5 EndY=-5.47787 EndZ=0
    g5: LineSegment StartX=-43.5 StartY=-5.47787 StartZ=0 EndX=-43.5 EndY=5.47787 EndZ=0
    g6: LineSegment StartX=-43.5 StartY=-7.5 StartZ=0 EndX=0 EndY=-1.01106 EndZ=0
    g7: LineSegment StartX=0 StartY=-1.01106 StartZ=0 EndX=43.5 EndY=-7.5 EndZ=0
    g8: LineSegment StartX=43.5 StartY=-7.5 StartZ=0 EndX=-43.5 EndY=-7.5 EndZ=0
    g9: LineSegment StartX=43.5 StartY=-5.47787 StartZ=0 EndX=6.77789 EndY=0 EndZ=0
    g10: LineSegment StartX=6.77789 StartY=0 StartZ=0 EndX=43.5 EndY=5.47787 EndZ=0
    g11: LineSegment StartX=43.5 StartY=5.47787 StartZ=0 EndX=43.5 EndY=-5.47787 EndZ=0
    g12: LineSegment StartX=-43.5 StartY=7.5 StartZ=0 EndX=43.5 EndY=7.5 EndZ=0
    g13: LineSegment StartX=43.5 StartY=7.5 StartZ=0 EndX=43.5 EndY=-7.5 EndZ=0
    g14: LineSegment StartX=43.5 StartY=-7.5 StartZ=0 EndX=-43.5 EndY=-7.5 EndZ=0
    g15: LineSegment StartX=-43.5 StartY=-7.5 StartZ=0 EndX=-43.5 EndY=7.5 EndZ=0
    g16: LineSegment StartX=0 StartY=1.01106 StartZ=0 EndX=6.77789 EndY=0 EndZ=0
    g17: LineSegment StartX=6.77789 StartY=0 StartZ=0 EndX=0 EndY=-1.01106 EndZ=0
    g18: LineSegment StartX=0 StartY=-1.01106 StartZ=0 EndX=-6.77789 EndY=0 EndZ=0
    g19: LineSegment StartX=-6.77789 StartY=0 StartZ=0 EndX=0 EndY=1.01106 EndZ=0
    g20: LineSegment StartX=-43.2049 StartY=7.45598 StartZ=0 EndX=-43.5 EndY=5.47787 EndZ=0
  constraints (54):
    c: Horizontal(g0)
    c: Coincident(g0,g1)
    c: PointOnObject(g1,g-2)
    c: Coincident(g1,g2)
    c: Coincident(g2,g0)
    c: PointOnObject(g3,g-1)
    c: Coincident(g3,g4)
    c: Coincident(g4,g5)
    c: Coincident(g5,g3)
    c: PointOnObject(g6,g-2)
    c: Coincident(g6,g7)
    c: Coincident(g7,g8)
    c: Coincident(g8,g6)
    c: Horizontal(g8)
    c: PointOnObject(g9,g-1)
    c: Coincident(g9,g10)
    c: Coincident(g10,g11)
    c: Coincident(g11,g9)
    c: Coincident(g12,g13)
    c: Coincident(g13,g14)
    c: Coincident(g14,g15)
    c: Coincident(g15,g12)
    c: Horizontal(g12)
    c: Horizontal(g14)
    c: Vertical(g15)
    c: PointOnObject(g3,g15)
    c: Coincident(g0,g12)
    c: Coincident(g6,g14)
    c: PointOnObject(g0,g13)
    c: PointOnObject(g10,g13)
    c: PointOnObject(g9,g13)
    c: PointOnObject(g7,g13)
    c: Symmetric(g0,g7,g-1)
    c: DistanceY(g0,g-4) = 10
    c: DistanceX(g-4,g0) = 2
    c: Symmetric(g3,g4,g-1)
    c: Symmetric(g10,g9,g-1)
    c: Coincident(g1,g16)
    c: Coincident(g16,g9)
    c: Coincident(g16,g17)
    c: Coincident(g17,g6)
    c: Coincident(g17,g18)
    c: Coincident(g18,g3)
    c: Coincident(g18,g19)
    c: Coincident(g19,g16)
    c: Parallel(g2,g16)
    c: Parallel(g16,g9)
    c: Parallel(g1,g19)
    c: Parallel(g19,g4)
    c: Parallel(g17,g10)
    c: PointOnObject(g20,g2)
    c: Perpendicular(g2,g20)
    c: Distance(g20) = 2
    c: Coincident(g20,g3)
FEATURE [PartDesign::Pocket] Pocket
  BaseFeature = -> Pad001
  Direction = (0,0,-1)
  Length = 8
  Length2 = 5
  Profile = -> Sketch002
  ReferenceAxis = -> Sketch002 [N_Axis]
  Type = 0
  expr: Length = Spreadsheet.height - Spreadsheet.walls_thickness
FEATURE [Sketcher::SketchObject] Sketch003
  ExternalGeometry = -> [Pocket]
  FullyConstrained = true
  MapMode = 5
  Placement = pos=(0,0,0) rot=(1,0,0;3.14159rad)
  Support = -> [Pocket]
  expr: Constraints[17] = <<Spreadsheet>>.display_width
  expr: Constraints[18] = <<Spreadsheet>>.display_height
  expr: Constraints[19] = (<<Spreadsheet>>.width - <<Spreadsheet>>.display_height) / 2 + <<Spreadsheet>>.connector_offset_y - <<Spreadsheet>>.hole_clearance
  expr: Constraints[20] = <<Spreadsheet>>.connector_height + <<Spreadsheet>>.hole_clearance
  expr: Constraints[21] = <<Spreadsheet>>.connector_width + <<Spreadsheet>>.hole_clearance
  expr: Constraints[22] = <<Spreadsheet>>.connector_offset_x - <<Spreadsheet>>.hole_clearance
  sketch-geometry (8):
    g0: LineSegment StartX=-42.26 StartY=27.63 StartZ=0 EndX=42.26 EndY=27.63 EndZ=0
    g1: LineSegment StartX=42.26 StartY=27.63 StartZ=0 EndX=42.26 EndY=-27.63 EndZ=0
    g2: LineSegment StartX=42.26 StartY=-27.63 StartZ=0 EndX=-42.26 EndY=-27.63 EndZ=0
    g3: LineSegment StartX=-42.26 StartY=-27.63 StartZ=0 EndX=-42.26 EndY=27.63 EndZ=0
    g4: LineSegment StartX=-36.26 StartY=27.63 StartZ=0 EndX=-1.26 EndY=27.63 EndZ=0
    g5: LineSegment StartX=-1.26 StartY=27.63 StartZ=0 EndX=-1.26 EndY=22.63 EndZ=0
    g6: LineSegment StartX=-1.26 StartY=22.63 StartZ=0 EndX=-36.26 EndY=22.63 EndZ=0
    g7: LineSegment StartX=-36.26 StartY=22.63 StartZ=0 EndX=-36.26 EndY=27.63 EndZ=0
  constraints (23):
    c: Coincident(g0,g1)
    c: Coincident(g1,g2)
    c: Coincident(g2,g3)
    c: Coincident(g3,g0)
    c: Horizontal(g0)
    c: Horizontal(g2)
    c: Vertical(g1)
    c: Vertical(g3)
    c: Coincident(g4,g5)
    c: Coincident(g5,g6)
    c: Coincident(g6,g7)
    c: Coincident(g7,g4)
    c: Horizontal(g4)
    c: Horizontal(g6)
    c: Vertical(g5)
    c: Vertical(g7)
    c: Symmetric(g0,g1,g-1)
    c: DistanceX(g0,g0) = 84.52
    c: DistanceY(g3,g3) = 55.26
    c: DistanceY(g4,g-4) = 2.37
    c: DistanceY(g7,g7) = 5
    c: DistanceX(g4,g4) = 35
    c: DistanceX(g0,g4) = 6
FEATURE [PartDesign::Pocket] Pocket001
  BaseFeature = -> Pocket
  Direction = (0,0,1)
  Length = 5
  Length2 = 5
  Profile = -> Sketch003
  ReferenceAxis = -> Sketch003 [N_Axis]
  Type = 1
FEATURE [Sketcher::SketchObject] Sketch004
  ExternalGeometry = -> [Pocket001]
  FullyConstrained = true
  MapMode = 5
  Placement = pos=(-45.5,0,0) rot=(0.57735,-0.57735,-0.57735;2.0944rad)
  Support = -> [Pocket001]
  expr: Constraints[10] = Spreadsheet.screw_radius
  expr: Constraints[11] = Spreadsheet.screw_radius
  expr: Constraints[6] = Spreadsheet.beams_width
  expr: Constraints[7] = Spreadsheet.beams_width
  sketch-geometry (4):
    g0: Circle CenterX=-12.5 CenterY=5 CenterZ=0 NormalX=0 NormalY=0 NormalZ=1 AngleXU=0 Radius=1.5
    g1: Circle CenterX=12.5 CenterY=5 CenterZ=0 NormalX=0 NormalY=0 NormalZ=1 AngleXU=0 Radius=1.5
    g2: LineSegment StartX=-7.5 StartY=10 StartZ=0 EndX=-7.5 EndY=0 EndZ=0
    g3: LineSegment StartX=7.5 StartY=10 StartZ=0 EndX=7.5 EndY=0 EndZ=0
  constraints (12):
    c: PointOnObject(g2,g-4)
    c: PointOnObject(g2,g-6)
    c: Vertical(g2)
    c: PointOnObject(g3,g-4)
    c: PointOnObject(g3,g-6)
    c: Vertical(g3)
    c: DistanceX(g-4,g2) = 10
    c: DistanceX(g3,g-5) = 10
    c: Symmetric(g-4,g2,g0)
    c: Symmetric(g-5,g3,g1)
    c: Radius(g0) = 1.5
    c: Radius(g1) = 1.5
FEATURE [PartDesign::Hole] Hole
  BaseFeature = -> Pocket001
  CustomThreadClearance = 0
  Depth = 221.105
  DepthType = 1
  Diameter = 3.4
  DrillForDepth = false
  DrillPoint = 1
  DrillPointAngle = 118
  HoleCutCountersinkAngle = 90
  HoleCutCustomValues = false
  HoleCutDepth = 0
  HoleCutDiameter = 6.1
  HoleCutType = 0
  ModelThread = false
  Profile = -> Sketch004
  Tapered = false
  TaperedAngle = 90
  ThreadClass = 0
  ThreadDepth = 221.105
  ThreadDepthType = 0
  ThreadDirection = 0
  ThreadFit = 0
  ThreadSize = 9
  ThreadType = 1
  Threaded = false
  UseCustomThreadClearance = false
FEATURE [Sketcher::SketchObject] Sketch005
  ExternalGeometry = -> [Hole]
  FullyConstrained = true
  MapMode = 5
  Placement = pos=(-45.5,0,0) rot=(0.57735,-0.57735,-0.57735;2.0944rad)
  Support = -> [Hole]
  expr: Constraints[36] = Spreadsheet.nut_width
  expr: Constraints[39] = Spreadsheet.nut_width
  sketch-geometry (14):
    g0: LineSegment StartX=-9.75 StartY=6.58771 StartZ=0 EndX=-12.5 EndY=8.17543 EndZ=0
    g1: LineSegment StartX=-12.5 StartY=8.17543 StartZ=0 EndX=-15.25 EndY=6.58771 EndZ=0
    g2: LineSegment StartX=-15.25 StartY=6.58771 StartZ=0 EndX=-15.25 EndY=3.41229 EndZ=0
    g3: LineSegment StartX=-15.25 StartY=3.41229 StartZ=0 EndX=-12.5 EndY=1.82457 EndZ=0
    g4: LineSegment StartX=-12.5 StartY=1.82457 StartZ=0 EndX=-9.75 EndY=3.41229 EndZ=0
    g5: LineSegment StartX=-9.75 StartY=3.41229 StartZ=0 EndX=-9.75 EndY=6.58771 EndZ=0
    g6: Circle CenterX=-12.5 CenterY=5 CenterZ=0 NormalX=0 NormalY=0 NormalZ=1 AngleXU=0 Radius=3.17543
    g7: LineSegment StartX=15.25 StartY=6.58771 StartZ=0 EndX=12.5 EndY=8.17543 EndZ=0
    g8: LineSegment StartX=12.5 StartY=8.17543 StartZ=0 EndX=9.75 EndY=6.58771 EndZ=0
    g9: LineSegment StartX=9.75 StartY=6.58771 StartZ=0 EndX=9.75 EndY=3.41229 EndZ=0
    g10: LineSegment StartX=9.75 StartY=3.41229 StartZ=0 EndX=12.5 EndY=1.82457 EndZ=0
    g11: LineSegment StartX=12.5 StartY=1.82457 StartZ=0 EndX=15.25 EndY=3.41229 EndZ=0
    g12: LineSegment StartX=15.25 StartY=3.41229 StartZ=0 EndX=15.25 EndY=6.58771 EndZ=0
    g13: Circle CenterX=12.5 CenterY=5 CenterZ=0 NormalX=0 NormalY=0 NormalZ=1 AngleXU=0 Radius=3.17543
  constraints (32):
    c: Coincident(g0,g1)
    c: Coincident(g1,g2)
    c: Coincident(g2,g3)
    c: Coincident(g3,g4)
    c: Coincident(g4,g5)
    c: Coincident(g5,g0)
    c: Equal(g0, g1-g5) x5
    c: PointOnObject(g0,g6)
    c: PointOnObject(g1,g6)
    c: PointOnObject(g2,g6)
    c: PointOnObject(g3,g6)
    c: PointOnObject(g4,g6)
    c: PointOnObject(g5,g6)
    c: Coincident(g6,g-3)
    c: Coincident(g7,g8)
    c: Coincident(g8,g9)
    c: Coincident(g9,g10)
    c: Coincident(g10,g11)
    c: Coincident(g11,g12)
    c: Coincident(g12,g7)
    c: Equal(g7, g8-g12) x5
    c: PointOnObject(g7,g13)
    c: PointOnObject(g8,g13)
    c: PointOnObject(g9,g13)
    c: PointOnObject(g10,g13)
    c: PointOnObject(g11,g13)
    c: PointOnObject(g12,g13)
    c: Coincident(g13,g-4)
    c: DistanceX(g1,g0) = 5.5
    c: Vertical(g5)
    c: Vertical(g9)
    c: DistanceX(g8,g7) = 5.5
FEATURE [PartDesign::Pocket] Pocket002
  BaseFeature = -> Hole
  Direction = (1,0,0)
  Length = 3
  Length2 = 5
  Profile = -> Sketch005
  ReferenceAxis = -> Sketch005 [N_Axis]
  Type = 0
  expr: Length = Spreadsheet.nut_depth
FEATURE [Sketcher::SketchObject] Sketch006
  ExternalGeometry = -> [Pocket002]
  FullyConstrained = true
  MapMode = 5
  Placement = pos=(45.5,0,0) rot=(0.57735,0.57735,0.57735;2.0944rad)
  Support = -> [Pocket002]
  expr: Constraints[38] = Spreadsheet.nut_width
  expr: Constraints[39] = Spreadsheet.nut_width
  sketch-geometry (14):
    g0: LineSegment StartX=-9.75 StartY=6.58771 StartZ=0 EndX=-12.5 EndY=8.17543 EndZ=0
    g1: LineSegment StartX=-12.5 StartY=8.17543 StartZ=0 EndX=-15.25 EndY=6.58771 EndZ=0
    g2: LineSegment StartX=-15.25 StartY=6.58771 StartZ=0 EndX=-15.25 EndY=3.41229 EndZ=0
    g3: LineSegment StartX=-15.25 StartY=3.41229 StartZ=0 EndX=-12.5 EndY=1.82457 EndZ=0
    g4: LineSegment StartX=-12.5 StartY=1.82457 StartZ=0 EndX=-9.75 EndY=3.41229 EndZ=0
    g5: LineSegment StartX=-9.75 StartY=3.41229 StartZ=0 EndX=-9.75 EndY=6.58771 EndZ=0
    g6: Circle CenterX=-12.5 CenterY=5 CenterZ=0 NormalX=0 NormalY=0 NormalZ=1 AngleXU=0 Radius=3.17543
    g7: LineSegment StartX=15.25 StartY=6.58771 StartZ=0 EndX=12.5 EndY=8.17543 EndZ=0
    g8: LineSegment StartX=12.5 StartY=8.17543 StartZ=0 EndX=9.75 EndY=6.58771 EndZ=0
    g9: LineSegment StartX=9.75 StartY=6.58771 StartZ=0 EndX=9.75 EndY=3.41229 EndZ=0
    g10: LineSegment StartX=9.75 StartY=3.41229 StartZ=0 EndX=12.5 EndY=1.82457 EndZ=0
    g11: LineSegment StartX=12.5 StartY=1.82457 StartZ=0 EndX=15.25 EndY=3.41229 EndZ=0
    g12: LineSegment StartX=15.25 StartY=3.41229 StartZ=0 EndX=15.25 EndY=6.58771 EndZ=0
    g13: Circle CenterX=12.5 CenterY=5 CenterZ=0 NormalX=0 NormalY=0 NormalZ=1 AngleXU=0 Radius=3.17543
  constraints (32):
    c: Coincident(g0,g1)
    c: Coincident(g1,g2)
    c: Coincident(g2,g3)
    c: Coincident(g3,g4)
    c: Coincident(g4,g5)
    c: Coincident(g5,g0)
    c: Equal(g0, g1-g5) x5
    c: PointOnObject(g0,g6)
    c: PointOnObject(g1,g6)
    c: PointOnObject(g2,g6)
    c: PointOnObject(g3,g6)
    c: PointOnObject(g4,g6)
    c: PointOnObject(g5,g6)
    c: Coincident(g6,g-3)
    c: Coincident(g7,g8)
    c: Coincident(g8,g9)
    c: Coincident(g9,g10)
    c: Coincident(g10,g11)
    c: Coincident(g11,g12)
    c: Coincident(g12,g7)
    c: Equal(g7, g8-g12) x5
    c: PointOnObject(g7,g13)
    c: PointOnObject(g8,g13)
    c: PointOnObject(g9,g13)
    c: PointOnObject(g10,g13)
    c: PointOnObject(g11,g13)
    c: PointOnObject(g12,g13)
    c: Coincident(g13,g-4)
    c: Vertical(g5)
    c: Vertical(g9)
    c: DistanceX(g1,g0) = 5.5
    c: DistanceX(g8,g7) = 5.5
FEATURE [PartDesign::Pocket] Pocket003
  BaseFeature = -> Pocket002
  Direction = (-1,0,0)
  Length = 3
  Length2 = 5
  Profile = -> Sketch006
  ReferenceAxis = -> Sketch006 [N_Axis]
  Type = 0
  expr: Length = Spreadsheet.nut_depth
FEATURE [App::DocumentObjectGroup] Parts
FEATURE [PartDesign::CoordinateSystem] LCS_Origin
  AttacherType = Attacher::AttachEngine3D
  MapMode = 2
  Support = -> [X_Axis001]
FEATURE [App::DocumentObjectGroup] Constraints
FEATURE [App::FeaturePython] Variables  # WARN: FeaturePython — macro-defined, semantics opaque (R4)
  Type = App::PropertyContainer
FEATURE [App::DocumentObjectGroup] Configurations
FEATURE [PartDesign::CoordinateSystem] LCS_side
  AttacherType = Attacher::AttachEngine3D
  MapMode = 11
  Placement = pos=(45.5,-12.5,5) rot=(0.57735,-0.57735,0.57735;4.18879rad)
  Support = -> [Pocket002]
FEATURE [PartDesign::CoordinateSystem] LCS_display
  AttacherType = Attacher::AttachEngine3D
  MapMode = 1
  Placement = pos=(-36.26,-27.63,0) rot=(0,0,1;0rad)
  Support = -> [Pocket002]
FEATURE [PartDesign::Chamfer] Chamfer
  Angle = 45
  Base = -> Pocket003 [Edge15,Edge1,Edge2,Edge17]
  BaseFeature = -> Pocket003
  ChamferType = 0
  FlipDirection = false
  Size = 8
  Size2 = 1
  SupportTransform = false
  UseAllEdges = false
FEATURE [PartDesign::Body] Body  label="Körper"
  Group = -> [Sketch,Pad,Sketch001,Pad001,Sketch002,Pocket,Sketch003,Pocket001,Sketch004,Hole,Sketch005,Pocket002,Sketch006,Pocket003,Chamfer]
  Origin = -> Origin
  Tip = -> Chamfer
FEATURE [App::Part] Model
  AssemblyType = Part::Link
  Group = -> [LCS_Origin,Constraints,Variables,Configurations,Body,LCS_side,LCS_display]
  Origin = -> Origin001
  Type = Assembly
FEATURE [Mesh::Feature] Mesh  label="Körper (Meshed)"
---- part Parts/Support_MLX.FCStd = doc fcstd_dba9274f7874 ----
FCSTD DOCUMENT  (FreeCAD 0.21R33668 +26 (Git))
Label: Support_MLX
License: All rights reserved
LicenseURL: http://en.wikipedia.org/wiki/All_rights_reserved
objects: Sketcher::SketchObject×7, PartDesign::Pocket×4, App::DocumentObjectGroup×3, PartDesign::CoordinateSystem×3, PartDesign::Hole×2, Spreadsheet::Sheet×1, App::FeaturePython×1, PartDesign::Pad×1, PartDesign::Body×1, App::Part×1, Mesh::Feature×1
note: 25 computed .brp shape members not serialized (recipe doc carries the construction recipe); baked Part::Feature solids carry a one-line shape summary decoded from their .brp
EXTERNAL_REF file=MLX90640.FCStd obj=Spreadsheet

FEATURE [Spreadsheet::Sheet] Spreadsheet
  cells = B2='MLX; B3='mlx_Hdist; C3(mlx_Hdist)==<<MLX90640>>#<<Spreadsheet>>.holes_Hdist; E3='walls_thickness; F3(walls_thickness)==2 mm; H3='nut_wall_thickness; I3(nut_wall_thickness)==5 mm; B4='mlx_Vdist; C4(mlx_Vdist)==<<MLX90640>>#<<Spreadsheet>>.holes_Vdist; E4='extra_space; F4(extra_space)==5 mm; H4='nut_depth; I4(nut_depth)==3 mm; B5='mlx_screw_radius; C5(mlx_screw_radius)==<<MLX90640>>#<<Spreadsheet>>.holes_rad; E5='carrier_width; F5(carrier_width)==10 mm; H5='nut_edge; I5(nut_edge)==5.5 mm; E6='carrier_height; F6(carrier_height)==mlx_Hdist + extra_space; B7='main_case_width; C7(main_case_width)==95 mm; E7='carrier_length; F7(carrier_length)==main_case_width - walls_thickness * 2; E8='screw_radius; F8(screw_radius)==1.5 mm
FEATURE [App::DocumentObjectGroup] Parts
FEATURE [PartDesign::CoordinateSystem] LCS_Origin
  AttacherType = Attacher::AttachEngine3D
  MapMode = 2
  Support = -> [X_Axis]
FEATURE [App::DocumentObjectGroup] Constraints
FEATURE [App::FeaturePython] Variables  # WARN: FeaturePython — macro-defined, semantics opaque (R4)
  Type = App::PropertyContainer
FEATURE [App::DocumentObjectGroup] Configurations
FEATURE [Sketcher::SketchObject] Sketch
  FullyConstrained = true
  MapMode = 5
  Support = -> [XY_Plane001]
  expr: Constraints[7] = <<Spreadsheet>>.carrier_length
  expr: Constraints[8] = <<Spreadsheet>>.carrier_height
  sketch-geometry (4):
    g0: LineSegment StartX=-45.5 StartY=12.66 StartZ=0 EndX=45.5 EndY=12.66 EndZ=0
    g1: LineSegment StartX=45.5 StartY=12.66 StartZ=0 EndX=45.5 EndY=-12.66 EndZ=0
    g2: LineSegment StartX=45.5 StartY=-12.66 StartZ=0 EndX=-45.5 EndY=-12.66 EndZ=0
    g3: LineSegment StartX=-45.5 StartY=-12.66 StartZ=0 EndX=-45.5 EndY=12.66 EndZ=0
  constraints (9):
    c: Coincident(g0,g1)
    c: Coincident(g1,g2)
    c: Coincident(g2,g3)
    c: Coincident(g3,g0)
    c: Symmetric(g0,g0,g-2)
    c: Symmetric(g0,g2,g-1)
    c: Symmetric(g0,g1,g-1)
    c: DistanceX(g0,g0) = 91
    c: DistanceY(g3,g3) = 25.32
FEATURE [PartDesign::Pad] Pad
  Direction = (0,0,1)
  Length = 10
  Length2 = 10
  Profile = -> Sketch
  ReferenceAxis = -> Sketch [N_Axis]
  Type = 0
  expr: Length = <<Spreadsheet>>.carrier_width
FEATURE [Sketcher::SketchObject] Sketch001
  ExternalGeometry = -> [Pad]
  FullyConstrained = true
  MapMode = 5
  Placement = pos=(0,0,10) rot=(0,0,1;0rad)
  Support = -> [Pad]
  expr: Constraints[19] = <<Spreadsheet>>.nut_wall_thickness
  expr: Constraints[20] = <<Spreadsheet>>.nut_wall_thickness
  expr: Constraints[21] = <<Spreadsheet>>.walls_thickness
  sketch-geometry (8):
    g0: LineSegment StartX=-40.5 StartY=12.66 StartZ=0 EndX=40.5 EndY=12.66 EndZ=0
    g1: LineSegment StartX=40.5 StartY=12.66 StartZ=0 EndX=40.5 EndY=1 EndZ=0
    g2: LineSegment StartX=40.5 StartY=1 StartZ=0 EndX=-40.5 EndY=1 EndZ=0
    g3: LineSegment StartX=-40.5 StartY=1 StartZ=0 EndX=-40.5 EndY=12.66 EndZ=0
    g4: LineSegment StartX=-40.5 StartY=-12.66 StartZ=0 EndX=40.5 EndY=-12.66 EndZ=0
    g5: LineSegment StartX=40.5 StartY=-12.66 StartZ=0 EndX=40.5 EndY=-1 EndZ=0
    g6: LineSegment StartX=40.5 StartY=-1 StartZ=0 EndX=-40.5 EndY=-1 EndZ=0
    g7: LineSegment StartX=-40.5 StartY=-1 StartZ=0 EndX=-40.5 EndY=-12.66 EndZ=0
  constraints (22):
    c: Coincident(g0,g1)
    c: Coincident(g1,g2)
    c: Coincident(g2,g3)
    c: Coincident(g3,g0)
    c: Horizontal(g0)
    c: Horizontal(g2)
    c: Vertical(g1)
    c: Vertical(g3)
    c: PointOnObject(g0,g-3)
    c: Coincident(g4,g5)
    c: Coincident(g5,g6)
    c: Coincident(g6,g7)
    c: Coincident(g7,g4)
    c: Horizontal(g4)
    c: Vertical(g5)
    c: Vertical(g7)
    c: PointOnObject(g4,g-5)
    c: Symmetric(g2,g6,g-1)
    c: Symmetric(g1,g5,g-1)
    c: DistanceX(g-4,g0) = 5
    c: DistanceX(g0,g-6) = 5
    c: DistanceY(g6,g2) = 2
FEATURE [PartDesign::Pocket] Pocket
  BaseFeature = -> Pad
  Direction = (0,0,-1)
  Length = 8
  Length2 = 5
  Profile = -> Sketch001
  ReferenceAxis = -> Sketch001 [N_Axis]
  Type = 0
  expr: Length = <<Spreadsheet>>.carrier_width - <<Spreadsheet>>.walls_thickness
FEATURE [Sketcher::SketchObject] Sketch004
  FullyConstrained = true
  MapMode = 5
  Placement = pos=(0,0,2) rot=(0,0,1;0rad)
  expr: Constraints[3] = <<Spreadsheet>>.mlx_Hdist
  expr: Constraints[4] = <<Spreadsheet>>.mlx_Vdist
  expr: Constraints[5] = <<Spreadsheet>>.mlx_screw_radius
  expr: Constraints[6] = <<Spreadsheet>>.mlx_screw_radius
  expr: Constraints[7] = <<Spreadsheet>>.mlx_screw_radius
  expr: Constraints[8] = <<Spreadsheet>>.mlx_screw_radius
  sketch-geometry (4):
    g0: Circle CenterX=10.16 CenterY=6.35 CenterZ=0 NormalX=0 NormalY=0 NormalZ=1 AngleXU=0 Radius=1.27
    g1: Circle CenterX=-10.16 CenterY=6.35 CenterZ=0 NormalX=0 NormalY=0 NormalZ=1 AngleXU=0 Radius=1.27
    g2: Circle CenterX=-10.16 CenterY=-6.35 CenterZ=0 NormalX=0 NormalY=0 NormalZ=1 AngleXU=0 Radius=1.27
    g3: Circle CenterX=10.16 CenterY=-6.35 CenterZ=0 NormalX=0 NormalY=0 NormalZ=1 AngleXU=0 Radius=1.27
  constraints (9):
    c: Symmetric(g1,g0,g-2)
    c: Symmetric(g2,g3,g-2)
    c: Symmetric(g1,g3,g-1)
    c: DistanceX(g1,g0) = 20.32
    c: DistanceY(g2,g1) = 12.7
    c: Radius(g1) = 1.27
    c: Radius(g0) = 1.27
    c: Radius(g2) = 1.27
    c: Radius(g3) = 1.27
FEATURE [PartDesign::Hole] Hole002
  BaseFeature = -> Pocket
  CustomThreadClearance = 0
  Depth = 2
  DepthType = 0
  Diameter = 2.5
  DrillForDepth = false
  DrillPoint = 1
  DrillPointAngle = 118
  HoleCutCountersinkAngle = 90
  HoleCutCustomValues = false
  HoleCutDepth = 0
  HoleCutDiameter = 6.1
  HoleCutType = 0
  ModelThread = false
  Profile = -> Sketch004
  Tapered = false
  TaperedAngle = 90
  ThreadClass = 0
  ThreadDepth = 2
  ThreadDepthType = 0
  ThreadDirection = 0
  ThreadFit = 0
  ThreadSize = 9
  ThreadType = 1
  Threaded = true
  UseCustomThreadClearance = false
  expr: Depth = <<Spreadsheet>>.walls_thickness
FEATURE [Sketcher::SketchObject] Sketch005
  ExternalGeometry = -> [Hole002]
  FullyConstrained = true
  MapMode = 5
  Placement = pos=(-45.5,0,0) rot=(0.57735,-0.57735,-0.57735;2.0944rad)
  Support = -> [Hole002]
  expr: Constraints[0] = <<Spreadsheet>>.carrier_width / 2
  expr: Constraints[1] = <<Spreadsheet>>.carrier_width / 2
  expr: Constraints[2] = <<Spreadsheet>>.carrier_width / 2
  expr: Constraints[3] = <<Spreadsheet>>.carrier_width / 2
  expr: Constraints[4] = <<Spreadsheet>>.screw_radius
  expr: Constraints[5] = <<Spreadsheet>>.screw_radius
  sketch-geometry (2):
    g0: Circle CenterX=-7.66 CenterY=5 CenterZ=0 NormalX=0 NormalY=0 NormalZ=1 AngleXU=0 Radius=1.5
    g1: Circle CenterX=7.66 CenterY=5 CenterZ=0 NormalX=0 NormalY=0 NormalZ=1 AngleXU=0 Radius=1.5
  constraints (6):
    c: DistanceX(g-4,g0) = 5
    c: DistanceX(g1,g-6) = 5
    c: DistanceY(g0,g-4) = 5
    c: DistanceY(g1,g-6) = 5
    c: Radius(g0) = 1.5
    c: Radius(g1) = 1.5
FEATURE [PartDesign::Hole] Hole
  BaseFeature = -> Hole002
  CustomThreadClearance = 0
  Depth = 191.869
  DepthType = 1
  Diameter = 3.4
  DrillForDepth = false
  DrillPoint = 1
  DrillPointAngle = 118
  HoleCutCountersinkAngle = 90
  HoleCutCustomValues = false
  HoleCutDepth = 0
  HoleCutDiameter = 6.1
  HoleCutType = 0
  ModelThread = false
  Profile = -> Sketch005
  Tapered = false
  TaperedAngle = 90
  ThreadClass = 0
  ThreadDepth = 191.869
  ThreadDepthType = 0
  ThreadDirection = 0
  ThreadFit = 0
  ThreadSize = 9
  ThreadType = 1
  Threaded = false
  UseCustomThreadClearance = false
FEATURE [PartDesign::CoordinateSystem] LCS_MLX
  AttacherType = Attacher::AttachEngine3D
  MapMode = 11
  Placement = pos=(-10.16,-6.35,2.2e-15) rot=(0,0,1;1.5708rad)
  Support = -> [Hole]
FEATURE [Sketcher::SketchObject] Sketch006
  ExternalGeometry = -> [Hole]
  FullyConstrained = true
  MapMode = 5
  Placement = pos=(0,0,0) rot=(1,0,0;3.14159rad)
  Support = -> [Hole]
  sketch-geometry (5):
    g0: LineSegment StartX=-8.16 StartY=8.35 StartZ=0 EndX=8.16 EndY=8.35 EndZ=0
    g1: LineSegment StartX=8.16 StartY=8.35 StartZ=0 EndX=8.16 EndY=4.35 EndZ=0
    g2: LineSegment StartX=8.16 StartY=4.35 StartZ=0 EndX=-8.16 EndY=4.35 EndZ=0
    g3: LineSegment StartX=-8.16 StartY=4.35 StartZ=0 EndX=-8.16 EndY=8.35 EndZ=0
    g4: GeomPoint X=3e-16 Y=6.35 Z=0
  constraints (11):
    c: Coincident(g0,g1)
    c: Coincident(g1,g2)
    c: Coincident(g2,g3)
    c: Coincident(g3,g0)
    c: Horizontal(g2)
    c: Vertical(g3)
    c: Symmetric(g0,g0,g-2)
    c: DistanceX(g-3,g0) = 2
    c: Symmetric(g-3,g-4,g4)
    c: Symmetric(g0,g1,g4)
    c: DistanceY(g3,g3) = 4
FEATURE [PartDesign::Pocket] Pocket001
  BaseFeature = -> Hole
  Direction = (0,0,1)
  Length = 2
  Length2 = 5
  Profile = -> Sketch006
  ReferenceAxis = -> Sketch006 [N_Axis]
  Type = 0
  expr: Length = <<Spreadsheet>>.walls_thickness
FEATURE [PartDesign::CoordinateSystem] LCS_carrier
  AttacherType = Attacher::AttachEngine3D
  MapMode = 11
  Placement = pos=(-45.5,-7.66,5) rot=(0.57735,0.57735,-0.57735;4.18879rad)
  Support = -> [Pocket001]
FEATURE [Sketcher::SketchObject] Sketch007
  ExternalGeometry = -> [Pocket001]
  FullyConstrained = true
  MapMode = 5
  Placement = pos=(45.5,-1.27e-14,0) rot=(0.57735,0.57735,0.57735;2.0944rad)
  Support = -> [Pocket001]
  expr: Constraints[38] = Spreadsheet.nut_edge
  expr: Constraints[39] = Spreadsheet.nut_edge
  sketch-geometry (14):
    g0: LineSegment StartX=-4.91 StartY=6.58771 StartZ=0 EndX=-7.66 EndY=8.17543 EndZ=0
    g1: LineSegment StartX=-7.66 StartY=8.17543 StartZ=0 EndX=-10.41 EndY=6.58771 EndZ=0
    g2: LineSegment StartX=-10.41 StartY=6.58771 StartZ=0 EndX=-10.41 EndY=3.41229 EndZ=0
    g3: LineSegment StartX=-10.41 StartY=3.41229 StartZ=0 EndX=-7.66 EndY=1.82457 EndZ=0
    g4: LineSegment StartX=-7.66 StartY=1.82457 StartZ=0 EndX=-4.91 EndY=3.41229 EndZ=0
    g5: LineSegment StartX=-4.91 StartY=3.41229 StartZ=0 EndX=-4.91 EndY=6.58771 EndZ=0
    g6: Circle CenterX=-7.66 CenterY=5 CenterZ=0 NormalX=0 NormalY=0 NormalZ=1 AngleXU=0 Radius=3.17543
    g7: LineSegment StartX=10.41 StartY=6.58771 StartZ=0 EndX=7.66 EndY=8.17543 EndZ=0
    g8: LineSegment StartX=7.66 StartY=8.17543 StartZ=0 EndX=4.91 EndY=6.58771 EndZ=0
    g9: LineSegment StartX=4.91 StartY=6.58771 StartZ=0 EndX=4.91 EndY=3.41229 EndZ=0
    g10: LineSegment StartX=4.91 StartY=3.41229 StartZ=0 EndX=7.66 EndY=1.82457 EndZ=0
    g11: LineSegment StartX=7.66 StartY=1.82457 StartZ=0 EndX=10.41 EndY=3.41229 EndZ=0
    g12: LineSegment StartX=10.41 StartY=3.41229 StartZ=0 EndX=10.41 EndY=6.58771 EndZ=0
    g13: Circle CenterX=7.66 CenterY=5 CenterZ=0 NormalX=0 NormalY=0 NormalZ=1 AngleXU=0 Radius=3.17543
  constraints (32):
    c: Coincident(g1,g2)
    c: Coincident(g2,g3)
    c: Coincident(g3,g4)
    c: Coincident(g4,g5)
    c: Coincident(g5,g0)
    c: Equal(g0, g1-g5) x5
    c: PointOnObject(g0,g6)
    c: PointOnObject(g1,g6)
    c: PointOnObject(g2,g6)
    c: PointOnObject(g3,g6)
    c: PointOnObject(g4,g6)
    c: PointOnObject(g5,g6)
    c: Coincident(g6,g-3)
    c: Coincident(g7,g8)
    c: Coincident(g8,g9)
    c: Coincident(g9,g10)
    c: Coincident(g10,g11)
    c: Coincident(g11,g12)
    c: Coincident(g12,g7)
    c: Equal(g7, g8-g12) x5
    c: PointOnObject(g7,g13)
    c: PointOnObject(g8,g13)
    c: PointOnObject(g9,g13)
    c: PointOnObject(g10,g13)
    c: PointOnObject(g11,g13)
    c: PointOnObject(g12,g13)
    c: Coincident(g13,g-4)
    c: Vertical(g5)
    c: Vertical(g12)
    c: Coincident(g1,g0)
    c: DistanceX(g2,g4) = 5.5
    c: DistanceX(g9,g11) = 5.5
FEATURE [PartDesign::Pocket] Pocket002
  BaseFeature = -> Pocket001
  Direction = (-1,1e-16,1e-16)
  Length = 3
  Length2 = 5
  Profile = -> Sketch007
  ReferenceAxis = -> Sketch007 [N_Axis]
  Type = 0
  expr: Length = Spreadsheet.nut_depth
FEATURE [Sketcher::SketchObject] Sketch008
  ExternalGeometry = -> [Pocket002]
  FullyConstrained = true
  MapMode = 5
  Placement = pos=(-45.5,0,0) rot=(0.57735,-0.57735,-0.57735;2.0944rad)
  Support = -> [Pocket002]
  expr: Constraints[38] = Spreadsheet.nut_edge
  expr: Constraints[39] = Spreadsheet.nut_edge
  sketch-geometry (14):
    g0: LineSegment StartX=-4.91 StartY=6.58771 StartZ=0 EndX=-7.66 EndY=8.17543 EndZ=0
    g1: LineSegment StartX=-7.66 StartY=8.17543 StartZ=0 EndX=-10.41 EndY=6.58771 EndZ=0
    g2: LineSegment StartX=-10.41 StartY=6.58771 StartZ=0 EndX=-10.41 EndY=3.41229 EndZ=0
    g3: LineSegment StartX=-10.41 StartY=3.41229 StartZ=0 EndX=-7.66 EndY=1.82457 EndZ=0
    g4: LineSegment StartX=-7.66 StartY=1.82457 StartZ=0 EndX=-4.91 EndY=3.41229 EndZ=0
    g5: LineSegment StartX=-4.91 StartY=3.41229 StartZ=0 EndX=-4.91 EndY=6.58771 EndZ=0
    g6: Circle CenterX=-7.66 CenterY=5 CenterZ=0 NormalX=0 NormalY=0 NormalZ=1 AngleXU=0 Radius=3.17543
    g7: LineSegment StartX=10.41 StartY=6.58771 StartZ=0 EndX=7.66 EndY=8.17543 EndZ=0
    g8: LineSegment StartX=7.66 StartY=8.17543 StartZ=0 EndX=4.91 EndY=6.58771 EndZ=0
    g9: LineSegment StartX=4.91 StartY=6.58771 StartZ=0 EndX=4.91 EndY=3.41229 EndZ=0
    g10: LineSegment StartX=4.91 StartY=3.41229 StartZ=0 EndX=7.66 EndY=1.82457 EndZ=0
    g11: LineSegment StartX=7.66 StartY=1.82457 StartZ=0 EndX=10.41 EndY=3.41229 EndZ=0
    g12: LineSegment StartX=10.41 StartY=3.41229 StartZ=0 EndX=10.41 EndY=6.58771 EndZ=0
    g13: Circle CenterX=7.66 CenterY=5 CenterZ=0 NormalX=0 NormalY=0 NormalZ=1 AngleXU=0 Radius=3.17543
  constraints (32):
    c: Coincident(g0,g1)
    c: Coincident(g1,g2)
    c: Coincident(g2,g3)
    c: Coincident(g3,g4)
    c: Coincident(g4,g5)
    c: Coincident(g5,g0)
    c: Equal(g0, g1-g5) x5
    c: PointOnObject(g0,g6)
    c: PointOnObject(g1,g6)
    c: PointOnObject(g2,g6)
    c: PointOnObject(g3,g6)
    c: PointOnObject(g4,g6)
    c: PointOnObject(g5,g6)
    c: Coincident(g6,g-3)
    c: Coincident(g7,g8)
    c: Coincident(g8,g9)
    c: Coincident(g9,g10)
    c: Coincident(g10,g11)
    c: Coincident(g11,g12)
    c: Coincident(g12,g7)
    c: Equal(g7, g8-g12) x5
    c: PointOnObject(g7,g13)
    c: PointOnObject(g8,g13)
    c: PointOnObject(g9,g13)
    c: PointOnObject(g10,g13)
    c: PointOnObject(g11,g13)
    c: PointOnObject(g12,g13)
    c: Coincident(g13,g-4)
    c: Vertical(g5)
    c: Vertical(g12)
    c: DistanceX(g2,g4) = 5.5
    c: DistanceX(g9,g11) = 5.5
FEATURE [PartDesign::Pocket] Pocket003
  BaseFeature = -> Pocket002
  Direction = (1,0,0)
  Length = 3
  Length2 = 5
  Profile = -> Sketch008
  ReferenceAxis = -> Sketch008 [N_Axis]
  Type = 0
  expr: Length = Spreadsheet.nut_depth
FEATURE [PartDesign::Body] Body
  Group = -> [Sketch,Pad,Sketch001,Pocket,Sketch004,Hole002,Sketch005,Hole,Sketch006,Pocket001,Sketch007,Pocket002,Sketch008,Pocket003]
  Origin = -> Origin001
  Tip = -> Pocket003
FEATURE [App::Part] Model
  AssemblyType = Part::Link
  Group = -> [LCS_Origin,Constraints,Variables,Configurations,Body,LCS_carrier,LCS_MLX]
  Origin = -> Origin
  Type = Assembly
FEATURE [Mesh::Feature] Mesh  label="Body (Meshed)"
---- part Parts/Support_Raspi_new.FCStd = doc fcstd_46f41ad778ed ----
FCSTD DOCUMENT  (FreeCAD 0.21R33668 +26 (Git))
Label: Support_Raspi_new
License: All rights reserved
LicenseURL: https://en.wikipedia.org/wiki/All_rights_reserved
objects: Sketcher::SketchObject×7, PartDesign::Pocket×4, App::DocumentObjectGroup×3, PartDesign::CoordinateSystem×3, PartDesign::Hole×2, Spreadsheet::Sheet×1, PartDesign::Pad×1, App::FeaturePython×1, PartDesign::Chamfer×1, PartDesign::Body×1, App::Part×1, Mesh::Feature×1
note: 27 computed .brp shape members not serialized (recipe doc carries the construction recipe); baked Part::Feature solids carry a one-line shape summary decoded from their .brp
EXTERNAL_REF file=Raspberrypi4B.FCStd obj=Spreadsheet

FEATURE [Spreadsheet::Sheet] Spreadsheet
  cells = B2='walls_thickness; C2(walls_thickness)==2 mm; E2='width; F2(width)==main_case_width - walls_thickness * 2; H2='nut_depth; I2(nut_depth)==3 mm; B3='screw_radius; C3(screw_radius)==1.5 mm; E3='height; F3(height)==raspi_height + 5 mm; H3='nut_edge; I3(nut_edge)==5.5 mm; E4='depth; F4(depth)==10 mm; H4='raspi_nut_edge; I4(raspi_nut_edge)==4.5 mm; B5='raspi_width; C5(raspi_width)==<<Raspberrypi4B>>#<<Spreadsheet>>.width; E5='beam_width; F5(beam_width)==10 mm; B6='raspi_height; C6(raspi_height)==<<Raspberrypi4B>>#<<Spreadsheet>>.height; E6='carrier_holes_space; F6(carrier_holes_space)==25 mm; H6='main_case_width; I6(main_case_width)==95 mm; B7='raspi_holesH; C7(raspi_holesH)==<<Raspberrypi4B>>#<<Spreadsheet>>.holes_distH; E7='cross_thickness; F7(cross_thickness)==2 mm; B8='raspi_holesV; C8(raspi_holesV)==<<Raspberrypi4B>>#<<Spreadsheet>>.holes_distV; E8='pocket_sd_length; F8(pocket_sd_length)==5 mm; B9='raspi_holes_off_x; C9(raspi_holes_off_x)==<<Raspberrypi4B>>#<<Spreadsheet>>.holes_offset_x; E10='offset_to_right; F10(offset_to_right)==2 mm; E11='screw_left_dist; F11(screw_left_dist)==raspi_width / 2 - raspi_holes_off_x - offset_to_right
FEATURE [Sketcher::SketchObject] Sketch
  FullyConstrained = true
  MapMode = 5
  Support = -> [XY_Plane]
  expr: Constraints[10] = Spreadsheet.height
  expr: Constraints[9] = Spreadsheet.width
  sketch-geometry (4):
    g0: LineSegment StartX=-45.5 StartY=30.5 StartZ=0 EndX=45.5 EndY=30.5 EndZ=0
    g1: LineSegment StartX=45.5 StartY=30.5 StartZ=0 EndX=45.5 EndY=-30.5 EndZ=0
    g2: LineSegment StartX=45.5 StartY=-30.5 StartZ=0 EndX=-45.5 EndY=-30.5 EndZ=0
    g3: LineSegment StartX=-45.5 StartY=-30.5 StartZ=0 EndX=-45.5 EndY=30.5 EndZ=0
  constraints (11):
    c: Coincident(g0,g1)
    c: Coincident(g1,g2)
    c: Coincident(g2,g3)
    c: Coincident(g3,g0)
    c: Horizontal(g0)
    c: Horizontal(g2)
    c: Vertical(g1)
    c: Vertical(g3)
    c: Symmetric(g0,g1,g-1)
    c: DistanceX(g0,g0) = 91
    c: DistanceY(g3,g3) = 61
FEATURE [PartDesign::Pad] Pad
  Direction = (0,0,1)
  Length = 10
  Length2 = 10
  Profile = -> Sketch
  ReferenceAxis = -> Sketch [N_Axis]
  Type = 0
  expr: Length = Spreadsheet.depth
FEATURE [Sketcher::SketchObject] Sketch001
  ExternalGeometry = -> [Pad]
  FullyConstrained = true
  MapMode = 5
  Placement = pos=(0,0,10) rot=(0,0,1;0rad)
  Support = -> [Pad]
  expr: Constraints[47] = Spreadsheet.walls_thickness
  expr: Constraints[48] = Spreadsheet.beam_width
  expr: Constraints[50] = Spreadsheet.carrier_holes_space - Spreadsheet.beam_width
  expr: Constraints[70] = Spreadsheet.cross_thickness
  sketch-geometry (29):
    g0: LineSegment StartX=-45.5 StartY=30.5 StartZ=0 EndX=45.5 EndY=30.5 EndZ=0
    g1: LineSegment StartX=45.5 StartY=30.5 StartZ=0 EndX=45.5 EndY=17.5 EndZ=0
    g2: LineSegment StartX=45.5 StartY=17.5 StartZ=0 EndX=-45.5 EndY=17.5 EndZ=0
    g3: LineSegment StartX=-45.5 StartY=17.5 StartZ=0 EndX=-45.5 EndY=30.5 EndZ=0
    g4: LineSegment StartX=-45.5 StartY=-30.5 StartZ=0 EndX=45.5 EndY=-30.5 EndZ=0
    g5: LineSegment StartX=45.5 StartY=-30.5 StartZ=0 EndX=45.5 EndY=-17.5 EndZ=0
    g6: LineSegment StartX=45.5 StartY=-17.5 StartZ=0 EndX=-45.5 EndY=-17.5 EndZ=0
    g7: LineSegment StartX=-45.5 StartY=-17.5 StartZ=0 EndX=-45.5 EndY=-30.5 EndZ=0
    g8: LineSegment StartX=-33.0935 StartY=7.5 StartZ=0 EndX=0 EndY=1.019 EndZ=0
    g9: LineSegment StartX=0 StartY=1.019 StartZ=0 EndX=33.0935 EndY=7.5 EndZ=0
    g10: LineSegment StartX=33.0935 StartY=7.5 StartZ=0 EndX=-33.0935 EndY=7.5 EndZ=0
    g11: LineSegment StartX=-43.5 StartY=7.5 StartZ=0 EndX=-5.20323 EndY=0 EndZ=0
    g12: LineSegment StartX=-5.20323 StartY=0 StartZ=0 EndX=-43.5 EndY=-7.5 EndZ=0
    g13: LineSegment StartX=-43.5 StartY=-7.5 StartZ=0 EndX=-43.5 EndY=7.5 EndZ=0
    g14: LineSegment StartX=-33.0935 StartY=-7.5 StartZ=0 EndX=0 EndY=-1.019 EndZ=0
    g15: LineSegment StartX=0 StartY=-1.019 StartZ=0 EndX=33.0935 EndY=-7.5 EndZ=0
    g16: LineSegment StartX=33.0935 StartY=-7.5 StartZ=0 EndX=-33.0935 EndY=-7.5 EndZ=0
    g17: LineSegment StartX=43.5 StartY=-7.5 StartZ=0 EndX=5.20323 EndY=0 EndZ=0
    g18: LineSegment StartX=5.20323 StartY=0 StartZ=0 EndX=43.5 EndY=7.5 EndZ=0
    g19: LineSegment StartX=43.5 StartY=7.5 StartZ=0 EndX=43.5 EndY=-7.5 EndZ=0
    g20: LineSegment StartX=-43.5 StartY=7.5 StartZ=0 EndX=43.5 EndY=7.5 EndZ=0
    g21: LineSegment StartX=43.5 StartY=7.5 StartZ=0 EndX=43.5 EndY=-7.5 EndZ=0
    g22: LineSegment StartX=43.5 StartY=-7.5 StartZ=0 EndX=-43.5 EndY=-7.5 EndZ=0
    g23: LineSegment StartX=-43.5 StartY=-7.5 StartZ=0 EndX=-43.5 EndY=7.5 EndZ=0
    g24: LineSegment StartX=0 StartY=1.019 StartZ=0 EndX=5.20323 EndY=0 EndZ=0
    g25: LineSegment StartX=5.20323 StartY=0 StartZ=0 EndX=0 EndY=-1.019 EndZ=0
    g26: LineSegment StartX=0 StartY=-1.019 StartZ=0 EndX=-5.20323 EndY=0 EndZ=0
    g27: LineSegment StartX=-5.20323 StartY=0 StartZ=0 EndX=0 EndY=1.019 EndZ=0
    g28: LineSegment StartX=-33.0935 StartY=7.5 StartZ=0 EndX=-33.4779 EndY=5.53728 EndZ=0
  constraints (72):
    c: Coincident(g0,g1)
    c: Coincident(g1,g2)
    c: Coincident(g2,g3)
    c: Coincident(g3,g0)
    c: Coincident(g0,g-4)
    c: PointOnObject(g1,g-6)
    c: Coincident(g4,g5)
    c: Coincident(g5,g6)
    c: Coincident(g6,g7)
    c: Coincident(g7,g4)
    c: Coincident(g4,g-5)
    c: Symmetric(g2,g6,g-1)
    c: PointOnObject(g2,g-4)
    c: Symmetric(g1,g5,g-1)
    c: PointOnObject(g8,g-2)
    c: Coincident(g8,g9)
    c: Coincident(g9,g10)
    c: Coincident(g10,g8)
    c: PointOnObject(g11,g-1)
    c: Coincident(g11,g12)
    c: Coincident(g12,g13)
    c: Coincident(g13,g11)
    c: PointOnObject(g14,g-2)
    c: Coincident(g14,g15)
    c: Coincident(g15,g16)
    c: Coincident(g16,g14)
    c: PointOnObject(g17,g-1)
    c: Coincident(g17,g18)
    c: Coincident(g18,g19)
    c: Coincident(g19,g17)
    c: Coincident(g20,g21)
    c: Coincident(g21,g22)
    c: Coincident(g22,g23)
    c: Coincident(g23,g20)
    c: Vertical(g21)
    c: Coincident(g11,g20)
    c: Coincident(g21,g17)
    c: Coincident(g18,g20)
    c: Coincident(g12,g22)
    c: Vertical(g13)
    c: Horizontal(g20)
    c: Horizontal(g22)
    c: PointOnObject(g8,g20)
    c: PointOnObject(g9,g20)
    c: PointOnObject(g14,g22)
    c: PointOnObject(g15,g22)
    c: Symmetric(g11,g17,g-1)
    c: DistanceX(g2,g11) = 2
    c: DistanceY(g11,g2) = 10
    c: Horizontal(g2)
    c: DistanceY(g13,g13) = 15
    c: Coincident(g4,g-6)
    c: Coincident(g0,g-6)
    c: Coincident(g8,g24)
    c: Coincident(g24,g17)
    c: Coincident(g24,g25)
    c: Coincident(g25,g14)
    c: Coincident(g25,g26)
    c: Coincident(g26,g11)
    c: Coincident(g26,g27)
    c: Coincident(g27,g24)
    c: Parallel(g24,g8)
    c: Parallel(g24,g17)
    c: Parallel(g25,g18)
    c: Parallel(g25,g14)
    c: Parallel(g26,g11)
    c: Parallel(g26,g15)
    c: Coincident(g28,g8)
    c: PointOnObject(g28,g11)
    c: Perpendicular(g11,g28)
    c: Distance(g28) = 2
    c: Parallel(g27,g9)
FEATURE [PartDesign::Pocket] Pocket
  BaseFeature = -> Pad
  Direction = (0,0,-1)
  Length = 8
  Length2 = 5
  Profile = -> Sketch001
  ReferenceAxis = -> Sketch001 [N_Axis]
  Type = 0
  expr: Length = Spreadsheet.depth - Spreadsheet.walls_thickness
FEATURE [Sketcher::SketchObject] Sketch002
  ExternalGeometry = -> [Pocket]
  FullyConstrained = true
  MapMode = 5
  Placement = pos=(0,0,0) rot=(1,0,0;3.14159rad)
  Support = -> [Pocket]
  expr: Constraints[11] = <<Spreadsheet>>.raspi_holesH
  expr: Constraints[12] = <<Spreadsheet>>.raspi_holesV
  expr: Constraints[14] = <<Spreadsheet>>.screw_left_dist
  expr: Constraints[15] = Spreadsheet.screw_radius
  expr: Constraints[16] = Spreadsheet.screw_radius
  expr: Constraints[17] = Spreadsheet.screw_radius
  expr: Constraints[18] = Spreadsheet.screw_radius
  sketch-geometry (8):
    g0: LineSegment StartX=-37 StartY=24.5 StartZ=0 EndX=21 EndY=24.5 EndZ=0
    g1: LineSegment StartX=21 StartY=24.5 StartZ=0 EndX=21 EndY=-24.5 EndZ=0
    g2: LineSegment StartX=21 StartY=-24.5 StartZ=0 EndX=-37 EndY=-24.5 EndZ=0
    g3: LineSegment StartX=-37 StartY=-24.5 StartZ=0 EndX=-37 EndY=24.5 EndZ=0
    g4: Circle CenterX=-37 CenterY=24.5 CenterZ=0 NormalX=0 NormalY=0 NormalZ=1 AngleXU=0 Radius=1.5
    g5: Circle CenterX=21 CenterY=24.5 CenterZ=0 NormalX=0 NormalY=0 NormalZ=1 AngleXU=0 Radius=1.5
    g6: Circle CenterX=21 CenterY=-24.5 CenterZ=0 NormalX=0 NormalY=0 NormalZ=1 AngleXU=0 Radius=1.5
    g7: Circle CenterX=-37 CenterY=-24.5 CenterZ=0 NormalX=0 NormalY=0 NormalZ=1 AngleXU=0 Radius=1.5
  constraints (19):
    c: Coincident(g0,g1)
    c: Coincident(g1,g2)
    c: Coincident(g2,g3)
    c: Coincident(g3,g0)
    c: Horizontal(g0)
    c: Horizontal(g2)
    c: Vertical(g1)
    c: Coincident(g4,g0)
    c: Coincident(g5,g0)
    c: Coincident(g6,g1)
    c: Coincident(g7,g2)
    c: DistanceX(g0,g0) = 58
    c: DistanceY(g3,g3) = 49
    c: Symmetric(g4,g7,g-1)
    c: DistanceX(g4,g-1) = 37
    c: Radius(g4) = 1.5
    c: Radius(g5) = 1.5
    c: Radius(g7) = 1.5
    c: Radius(g6) = 1.5
FEATURE [PartDesign::Hole] Hole
  BaseFeature = -> Pocket
  CustomThreadClearance = 0
  Depth = 222.218
  DepthType = 1
  Diameter = 2.9
  DrillForDepth = false
  DrillPoint = 1
  DrillPointAngle = 118
  HoleCutCountersinkAngle = 90
  HoleCutCustomValues = false
  HoleCutDepth = 0
  HoleCutDiameter = 6.1
  HoleCutType = 0
  ModelThread = false
  Profile = -> Sketch002
  Tapered = false
  TaperedAngle = 90
  ThreadClass = 0
  ThreadDepth = 222.218
  ThreadDepthType = 0
  ThreadDirection = 0
  ThreadFit = 0
  ThreadSize = 8
  ThreadType = 1
  Threaded = false
  UseCustomThreadClearance = false
FEATURE [Sketcher::SketchObject] Sketch003
  ExternalGeometry = -> [Hole]
  FullyConstrained = true
  MapMode = 5
  Placement = pos=(-45.5,0,0) rot=(0.57735,-0.57735,-0.57735;2.0944rad)
  Support = -> [Hole]
  expr: Constraints[10] = Spreadsheet.screw_radius
  expr: Constraints[11] = Spreadsheet.screw_radius
  expr: Constraints[6] = Spreadsheet.beam_width
  expr: Constraints[7] = Spreadsheet.beam_width
  sketch-geometry (4):
    g0: LineSegment StartX=-7.5 StartY=10 StartZ=0 EndX=-7.5 EndY=0 EndZ=0
    g1: LineSegment StartX=7.5 StartY=10 StartZ=0 EndX=7.5 EndY=0 EndZ=0
    g2: Circle CenterX=-12.5 CenterY=5 CenterZ=0 NormalX=0 NormalY=0 NormalZ=1 AngleXU=0 Radius=1.5
    g3: Circle CenterX=12.5 CenterY=5 CenterZ=0 NormalX=0 NormalY=0 NormalZ=1 AngleXU=0 Radius=1.5
  constraints (12):
    c: PointOnObject(g0,g-4)
    c: PointOnObject(g0,g-6)
    c: Vertical(g0)
    c: PointOnObject(g1,g-4)
    c: PointOnObject(g1,g-6)
    c: Vertical(g1)
    c: DistanceX(g-4,g0) = 10
    c: DistanceX(g1,g-5) = 10
    c: Symmetric(g-4,g0,g2)
    c: Symmetric(g-5,g1,g3)
    c: Radius(g2) = 1.5
    c: Radius(g3) = 1.5
FEATURE [PartDesign::Hole] Hole001
  BaseFeature = -> Hole
  CustomThreadClearance = 0
  Depth = 222.218
  DepthType = 1
  Diameter = 3.4
  DrillForDepth = false
  DrillPoint = 1
  DrillPointAngle = 118
  HoleCutCountersinkAngle = 90
  HoleCutCustomValues = false
  HoleCutDepth = 0
  HoleCutDiameter = 6.1
  HoleCutType = 0
  ModelThread = false
  Profile = -> Sketch003
  Tapered = false
  TaperedAngle = 90
  ThreadClass = 0
  ThreadDepth = 222.218
  ThreadDepthType = 0
  ThreadDirection = 0
  ThreadFit = 0
  ThreadSize = 9
  ThreadType = 1
  Threaded = false
  UseCustomThreadClearance = false
FEATURE [Sketcher::SketchObject] Sketch004
  ExternalGeometry = -> [Hole001]
  FullyConstrained = true
  MapMode = 5
  Placement = pos=(-45.5,0,0) rot=(0.57735,-0.57735,-0.57735;2.0944rad)
  Support = -> [Hole001]
  expr: Constraints[38] = Spreadsheet.nut_edge
  expr: Constraints[39] = Spreadsheet.nut_edge
  sketch-geometry (14):
    g0: LineSegment StartX=-9.75 StartY=6.58771 StartZ=0 EndX=-12.5 EndY=8.17543 EndZ=0
    g1: LineSegment StartX=-12.5 StartY=8.17543 StartZ=0 EndX=-15.25 EndY=6.58771 EndZ=0
    g2: LineSegment StartX=-15.25 StartY=6.58771 StartZ=0 EndX=-15.25 EndY=3.41229 EndZ=0
    g3: LineSegment StartX=-15.25 StartY=3.41229 StartZ=0 EndX=-12.5 EndY=1.82457 EndZ=0
    g4: LineSegment StartX=-12.5 StartY=1.82457 StartZ=0 EndX=-9.75 EndY=3.41229 EndZ=0
    g5: LineSegment StartX=-9.75 StartY=3.41229 StartZ=0 EndX=-9.75 EndY=6.58771 EndZ=0
    g6: Circle CenterX=-12.5 CenterY=5 CenterZ=0 NormalX=0 NormalY=0 NormalZ=1 AngleXU=0 Radius=3.17543
    g7: LineSegment StartX=15.25 StartY=6.58771 StartZ=0 EndX=12.5 EndY=8.17543 EndZ=0
    g8: LineSegment StartX=12.5 StartY=8.17543 StartZ=0 EndX=9.75 EndY=6.58771 EndZ=0
    g9: LineSegment StartX=9.75 StartY=6.58771 StartZ=0 EndX=9.75 EndY=3.41229 EndZ=0
    g10: LineSegment StartX=9.75 StartY=3.41229 StartZ=0 EndX=12.5 EndY=1.82457 EndZ=0
    g11: LineSegment StartX=12.5 StartY=1.82457 StartZ=0 EndX=15.25 EndY=3.41229 EndZ=0
    g12: LineSegment StartX=15.25 StartY=3.41229 StartZ=0 EndX=15.25 EndY=6.58771 EndZ=0
    g13: Circle CenterX=12.5 CenterY=5 CenterZ=0 NormalX=0 NormalY=0 NormalZ=1 AngleXU=0 Radius=3.17543
  constraints (32):
    c: Coincident(g0,g1)
    c: Coincident(g1,g2)
    c: Coincident(g2,g3)
    c: Coincident(g3,g4)
    c: Coincident(g4,g5)
    c: Coincident(g5,g0)
    c: Equal(g0, g1-g5) x5
    c: PointOnObject(g0,g6)
    c: PointOnObject(g1,g6)
    c: PointOnObject(g2,g6)
    c: PointOnObject(g3,g6)
    c: PointOnObject(g4,g6)
    c: PointOnObject(g5,g6)
    c: Coincident(g6,g-3)
    c: Coincident(g7,g8)
    c: Coincident(g8,g9)
    c: Coincident(g9,g10)
    c: Coincident(g10,g11)
    c: Coincident(g11,g12)
    c: Coincident(g12,g7)
    c: Equal(g7, g8-g12) x5
    c: PointOnObject(g7,g13)
    c: PointOnObject(g8,g13)
    c: PointOnObject(g9,g13)
    c: PointOnObject(g10,g13)
    c: PointOnObject(g11,g13)
    c: PointOnObject(g12,g13)
    c: Coincident(g13,g-4)
    c: Vertical(g5)
    c: Vertical(g9)
    c: DistanceX(g1,g0) = 5.5
    c: DistanceX(g8,g7) = 5.5
FEATURE [PartDesign::Pocket] Pocket001
  BaseFeature = -> Hole001
  Direction = (1,0,0)
  Length = 3
  Length2 = 5
  Profile = -> Sketch004
  ReferenceAxis = -> Sketch004 [N_Axis]
  Type = 0
  expr: Length = Spreadsheet.nut_depth
FEATURE [Sketcher::SketchObject] Sketch005
  ExternalGeometry = -> [Pocket001]
  FullyConstrained = true
  MapMode = 5
  Placement = pos=(45.5,0,0) rot=(0.57735,0.57735,0.57735;2.0944rad)
  Support = -> [Pocket001]
  expr: Constraints[38] = Spreadsheet.nut_edge
  expr: Constraints[39] = Spreadsheet.nut_edge
  sketch-geometry (14):
    g0: LineSegment StartX=-9.75 StartY=6.58771 StartZ=0 EndX=-12.5 EndY=8.17543 EndZ=0
    g1: LineSegment StartX=-12.5 StartY=8.17543 StartZ=0 EndX=-15.25 EndY=6.58771 EndZ=0
    g2: LineSegment StartX=-15.25 StartY=6.58771 StartZ=0 EndX=-15.25 EndY=3.41229 EndZ=0
    g3: LineSegment StartX=-15.25 StartY=3.41229 StartZ=0 EndX=-12.5 EndY=1.82457 EndZ=0
    g4: LineSegment StartX=-12.5 StartY=1.82457 StartZ=0 EndX=-9.75 EndY=3.41229 EndZ=0
    g5: LineSegment StartX=-9.75 StartY=3.41229 StartZ=0 EndX=-9.75 EndY=6.58771 EndZ=0
    g6: Circle CenterX=-12.5 CenterY=5 CenterZ=0 NormalX=0 NormalY=0 NormalZ=1 AngleXU=0 Radius=3.17543
    g7: LineSegment StartX=15.25 StartY=6.58771 StartZ=0 EndX=12.5 EndY=8.17543 EndZ=0
    g8: LineSegment StartX=12.5 StartY=8.17543 StartZ=0 EndX=9.75 EndY=6.58771 EndZ=0
    g9: LineSegment StartX=9.75 StartY=6.58771 StartZ=0 EndX=9.75 EndY=3.41229 EndZ=0
    g10: LineSegment StartX=9.75 StartY=3.41229 StartZ=0 EndX=12.5 EndY=1.82457 EndZ=0
    g11: LineSegment StartX=12.5 StartY=1.82457 StartZ=0 EndX=15.25 EndY=3.41229 EndZ=0
    g12: LineSegment StartX=15.25 StartY=3.41229 StartZ=0 EndX=15.25 EndY=6.58771 EndZ=0
    g13: Circle CenterX=12.5 CenterY=5 CenterZ=0 NormalX=0 NormalY=0 NormalZ=1 AngleXU=0 Radius=3.17543
  constraints (32):
    c: Coincident(g0,g1)
    c: Coincident(g1,g2)
    c: Coincident(g2,g3)
    c: Coincident(g3,g4)
    c: Coincident(g4,g5)
    c: Coincident(g5,g0)
    c: Equal(g0, g1-g5) x5
    c: PointOnObject(g0,g6)
    c: PointOnObject(g1,g6)
    c: PointOnObject(g2,g6)
    c: PointOnObject(g3,g6)
    c: PointOnObject(g4,g6)
    c: PointOnObject(g5,g6)
    c: Coincident(g6,g-3)
    c: Coincident(g7,g8)
    c: Coincident(g8,g9)
    c: Coincident(g9,g10)
    c: Coincident(g10,g11)
    c: Coincident(g11,g12)
    c: Coincident(g12,g7)
    c: Equal(g7, g8-g12) x5
    c: PointOnObject(g7,g13)
    c: PointOnObject(g8,g13)
    c: PointOnObject(g9,g13)
    c: PointOnObject(g10,g13)
    c: PointOnObject(g11,g13)
    c: PointOnObject(g12,g13)
    c: Coincident(g13,g-4)
    c: Vertical(g5)
    c: Vertical(g9)
    c: DistanceX(g1,g0) = 5.5
    c: DistanceX(g8,g7) = 5.5
FEATURE [PartDesign::Pocket] Pocket002
  BaseFeature = -> Pocket001
  Direction = (-1,0,0)
  Length = 3
  Length2 = 5
  Profile = -> Sketch005
  ReferenceAxis = -> Sketch005 [N_Axis]
  Type = 0
  expr: Length = Spreadsheet.nut_depth
FEATURE [App::DocumentObjectGroup] Parts
FEATURE [PartDesign::CoordinateSystem] LCS_Origin
  AttacherType = Attacher::AttachEngine3D
  MapMode = 2
  Support = -> [X_Axis001]
FEATURE [App::DocumentObjectGroup] Constraints
FEATURE [App::FeaturePython] Variables  # WARN: FeaturePython — macro-defined, semantics opaque (R4)
  Type = App::PropertyContainer
FEATURE [App::DocumentObjectGroup] Configurations
FEATURE [PartDesign::CoordinateSystem] LCS_side
  AttacherType = Attacher::AttachEngine3D
  MapMode = 11
  Placement = pos=(45.5,-12.5,5) rot=(0.57735,-0.57735,0.57735;4.18879rad)
  Support = -> [Pocket001]
FEATURE [PartDesign::CoordinateSystem] LCS_raspi
  AttacherType = Attacher::AttachEngine3D
  MapMode = 11
  Placement = pos=(-37,-24.5,0) rot=(0.707107,0.707107,0;3.14159rad)
  Support = -> [Pocket001]
FEATURE [Sketcher::SketchObject] Sketch006
  ExternalGeometry = -> [Pocket001]
  FullyConstrained = true
  MapMode = 5
  Placement = pos=(0,0,0) rot=(1,0,0;3.14159rad)
  Support = -> [Pocket001]
  expr: Constraints[9] = Spreadsheet.pocket_sd_length + Spreadsheet.offset_to_right
  sketch-geometry (5):
    g0: LineSegment StartX=-45.5 StartY=7.89168 StartZ=0 EndX=-38.5 EndY=6.52081 EndZ=0
    g1: LineSegment StartX=-38.5 StartY=6.52081 StartZ=0 EndX=-38.5 EndY=-6.52081 EndZ=0
    g2: LineSegment StartX=-38.5 StartY=-6.52081 StartZ=0 EndX=-45.5 EndY=-7.89168 EndZ=0
    g3: LineSegment StartX=-45.5 StartY=-7.89168 StartZ=0 EndX=-45.5 EndY=7.89168 EndZ=0
    g4: GeomPoint X=-45.5 Y=0 Z=0
  constraints (13):
    c: Coincident(g0,g1)
    c: Coincident(g1,g2)
    c: Coincident(g2,g3)
    c: Coincident(g3,g0)
    c: Vertical(g1)
    c: Vertical(g3)
    c: PointOnObject(g4,g-3)
    c: PointOnObject(g4,g-1)
    c: Symmetric(g0,g2,g4)
    c: DistanceX(g0,g0) = 7
    c: PointOnObject(g1,g-5)
    c: PointOnObject(g0,g-4)
    c: PointOnObject(g-4,g0)
FEATURE [PartDesign::Pocket] Pocket003
  BaseFeature = -> Pocket002
  Direction = (0,0,1)
  Length = 5
  Length2 = 5
  Profile = -> Sketch006
  ReferenceAxis = -> Sketch006 [N_Axis]
  Type = 1
FEATURE [PartDesign::Chamfer] Chamfer
  Angle = 45
  Base = -> Pocket003 [Edge47,Edge4,Edge2,Edge16]
  BaseFeature = -> Pocket003
  ChamferType = 0
  FlipDirection = false
  Size = 5
  Size2 = 1
  SupportTransform = false
  UseAllEdges = false
FEATURE [PartDesign::Body] Body  label="Körper"
  Group = -> [Sketch,Pad,Sketch001,Pocket,Sketch002,Hole,Sketch003,Hole001,Sketch004,Pocket001,Sketch005,Pocket002,Sketch006,Pocket003,Chamfer]
  Origin = -> Origin
  Tip = -> Chamfer
FEATURE [App::Part] Model
  AssemblyType = Part::Link
  Group = -> [LCS_Origin,Constraints,Variables,Configurations,Body,LCS_side,LCS_raspi]
  Origin = -> Origin001
  Type = Assembly
FEATURE [Mesh::Feature] Mesh  label="Körper (Meshed)"
